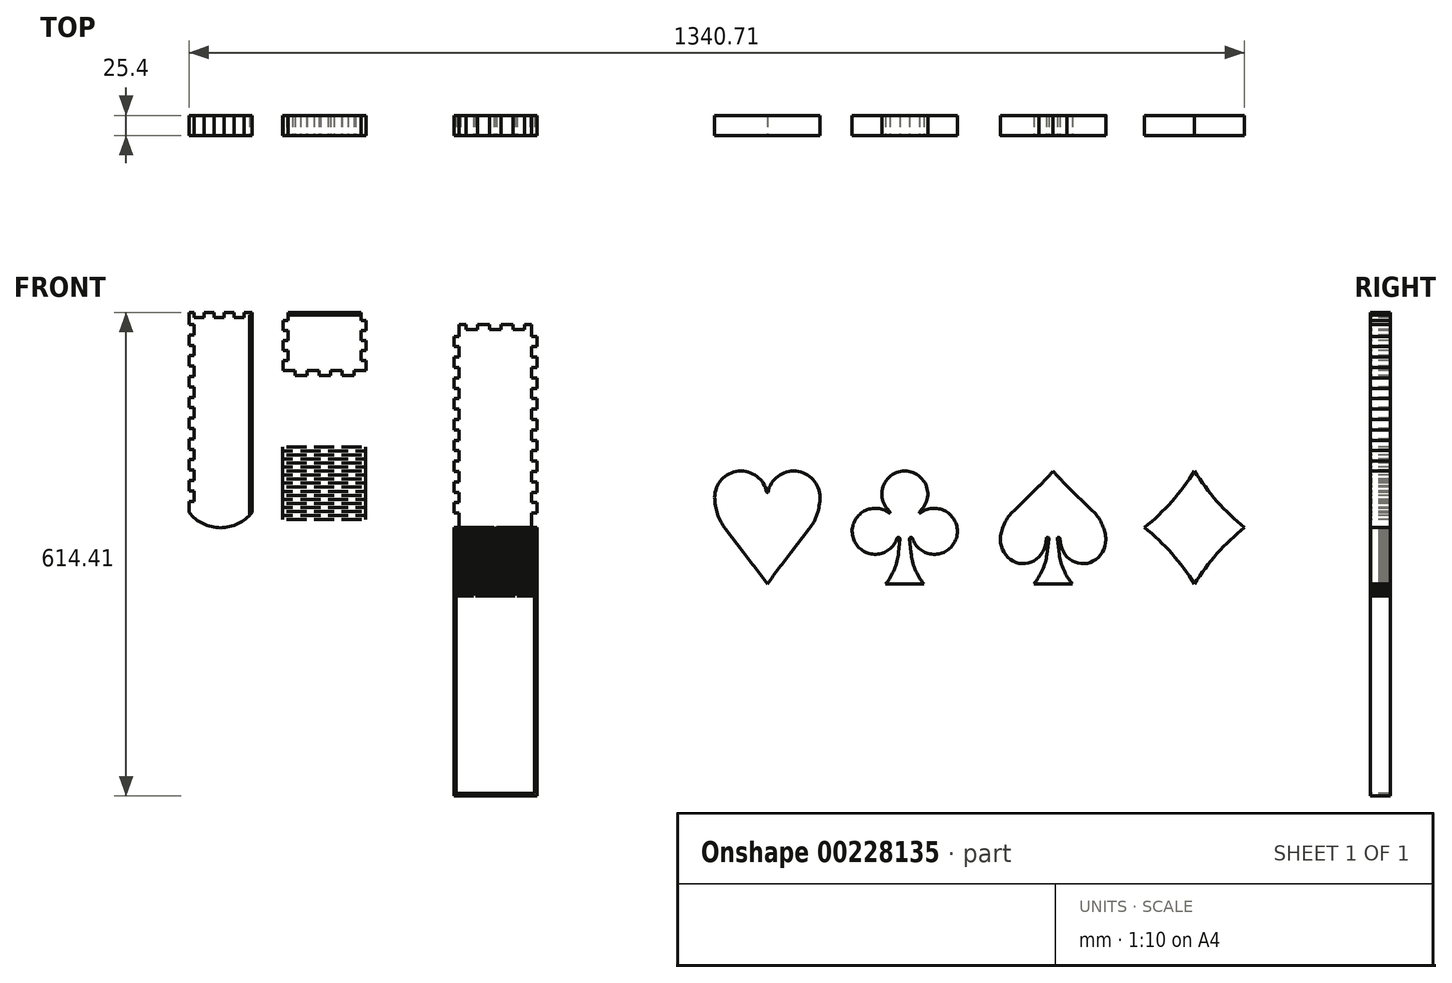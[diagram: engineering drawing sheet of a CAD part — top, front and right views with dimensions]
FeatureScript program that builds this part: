
annotation { "Feature Type Name" : "Feature", "Feature Type Description" : "" }
export const myFeature = defineFeature(function(context is Context, id is Id, definition is map)
    precondition{}
    {
        {
            var Q0;
            Q0=qCreatedBy(makeId("Front.planeOp"),FACE);
            var sketch = newSketch(context, id + "F0", { "sketchPlane" : qUnion([Q0])});
            skLineSegment(sketch, "E0.bottom", {"start": v(-104.23, 196.53) * mm, "end": v(-97.88, 196.53) * mm});
            skLineSegment(sketch, "E0.top", {"start": v(-104.23, -57.47) * mm, "end": v(-24.22, -57.47) * mm, "construction": true});
            skLineSegment(sketch, "E0.left", {"start": v(-104.23, 196.53) * mm, "end": v(-104.23, 181.29) * mm});
            skLineSegment(sketch, "E0.right", {"start": v(-24.22, 196.53) * mm, "end": v(-24.22, -57.47) * mm});
            skArc(sketch, "E1", {"start": v(-104.23, -57.47) * mm, "mid": v(-64.23, -76.96) * mm, "end": v(-24.22, -57.47) * mm});
            skLineSegment(sketch, "E2.0", {"start": v(-97.88, 181.29) * mm, "end": v(-97.88, 168.08) * mm});
            skLineSegment(sketch, "E2.1", {"start": v(-97.88, 190.18) * mm, "end": v(-85.18, 190.18) * mm});
            skLineSegment(sketch, "E3.0", {"start": v(-27.4, 193.35) * mm, "end": v(-27.4, -61.15) * mm});
            skLineSegment(sketch, "E4.bottom", {"start": v(21.69, 196.53) * mm, "end": v(114.4, 196.53) * mm});
            skLineSegment(sketch, "E4.top", {"start": v(30.76, 116.52) * mm, "end": v(45.74, 116.52) * mm});
            skLineSegment(sketch, "E4.left", {"start": v(15.34, 186.37) * mm, "end": v(15.34, 173.67) * mm});
            skLineSegment(sketch, "E5.0", {"start": v(21.69, 196.53) * mm, "end": v(21.69, 186.37) * mm});
            skLineSegment(sketch, "E5.3", {"start": v(15.34, 122.87) * mm, "end": v(30.76, 122.87) * mm});
            skLineSegment(sketch, "E6.left", {"start": v(14.8, 25.75) * mm, "end": v(14.8, -66.32) * mm});
            skLineSegment(sketch, "E6.right", {"start": v(120.2, 25.8) * mm, "end": v(120.2, -66.32) * mm});
            skLineSegment(sketch, "E7", {"start": v(21.69, 193.35) * mm, "end": v(114.4, 193.35) * mm});
            skLineSegment(sketch, "E8", {"start": v(19.75, 25.75) * mm, "end": v(45.15, 25.75) * mm});
            skLineSegment(sketch, "E9", {"start": v(-97.88, 190.18) * mm, "end": v(-97.88, 190.18) * mm});
            skLineSegment(sketch, "E10", {"start": v(-97.88, 190.18) * mm, "end": v(-97.88, 196.53) * mm});
            skLineSegment(sketch, "E11", {"start": v(-85.18, 190.18) * mm, "end": v(-85.18, 196.53) * mm});
            skLineSegment(sketch, "E12", {"start": v(-59.78, 190.18) * mm, "end": v(-59.78, 196.53) * mm});
            skLineSegment(sketch, "E13", {"start": v(-47.08, 190.18) * mm, "end": v(-47.08, 196.53) * mm});
            skLineSegment(sketch, "E14", {"start": v(-34.38, 190.18) * mm, "end": v(-34.38, 196.53) * mm});
            skLineSegment(sketch, "E15", {"start": v(-72.48, 190.18) * mm, "end": v(-72.48, 196.53) * mm});
            skLineSegment(sketch, "E16.trimOffspring", {"start": v(-34.38, 196.53) * mm, "end": v(-24.22, 196.53) * mm});
            skLineSegment(sketch, "E17.trimOffspring", {"start": v(-47.08, 190.18) * mm, "end": v(-34.38, 190.18) * mm});
            skLineSegment(sketch, "E18.trimOffspring", {"start": v(-59.78, 196.53) * mm, "end": v(-47.08, 196.53) * mm});
            skLineSegment(sketch, "E19.trimOffspring", {"start": v(-85.18, 196.53) * mm, "end": v(-72.48, 196.53) * mm});
            skLineSegment(sketch, "E20.trimOffspring", {"start": v(-72.48, 190.18) * mm, "end": v(-59.78, 190.18) * mm});
            skLineSegment(sketch, "E21", {"start": v(-27.4, 193.35) * mm, "end": v(-24.22, 193.35) * mm});
            skLineSegment(sketch, "E22", {"start": v(15.34, 186.37) * mm, "end": v(21.69, 186.37) * mm});
            skLineSegment(sketch, "E23", {"start": v(21.69, 173.67) * mm, "end": v(15.34, 173.67) * mm});
            skLineSegment(sketch, "E24", {"start": v(15.34, 160.97) * mm, "end": v(21.69, 160.97) * mm});
            skLineSegment(sketch, "E25", {"start": v(21.69, 148.27) * mm, "end": v(15.34, 148.27) * mm});
            skLineSegment(sketch, "E26", {"start": v(15.34, 135.57) * mm, "end": v(21.69, 135.57) * mm});
            skPoint(sketch, "E27.orphan", {"position": v(15.34, 196.53) * mm});
            skLineSegment(sketch, "E28.trimOffspring", {"start": v(21.69, 173.67) * mm, "end": v(21.69, 160.97) * mm});
            skLineSegment(sketch, "E29.trimOffspring", {"start": v(15.34, 160.97) * mm, "end": v(15.34, 148.27) * mm});
            skLineSegment(sketch, "E30.trimOffspring", {"start": v(21.69, 148.27) * mm, "end": v(21.69, 135.57) * mm});
            skLineSegment(sketch, "E31.trimOffspring", {"start": v(15.34, 135.57) * mm, "end": v(15.34, 122.87) * mm});
            skLineSegment(sketch, "E32", {"start": v(68.04, 193.35) * mm, "end": v(68.04, 116.52) * mm, "construction": true});
            skPoint(sketch, "E32.endSnap0", {"position": v(64.87, 122.87) * mm});
            skLineSegment(sketch, "E33", {"start": v(30.76, 122.87) * mm, "end": v(30.76, 116.52) * mm});
            skLineSegment(sketch, "E34", {"start": v(45.74, 116.52) * mm, "end": v(45.74, 122.87) * mm});
            skLineSegment(sketch, "E35", {"start": v(60.73, 122.87) * mm, "end": v(60.73, 116.52) * mm});
            skLineSegment(sketch, "E36.trimOffspring", {"start": v(45.74, 122.87) * mm, "end": v(60.73, 122.87) * mm});
            skLineSegment(sketch, "E37.trimOffspring", {"start": v(60.73, 116.52) * mm, "end": v(68.04, 116.52) * mm});
            skPoint(sketch, "E38.orphan", {"position": v(68.04, 122.87) * mm});
            skPoint(sketch, "E39.orphan", {"position": v(114.4, 122.87) * mm});
            skLineSegment(sketch, "E40.MirrorCS", {"start": v(120.75, 186.37) * mm, "end": v(114.4, 186.37) * mm});
            skLineSegment(sketch, "E41.MirrorCS", {"start": v(105.32, 122.87) * mm, "end": v(105.32, 116.52) * mm});
            skLineSegment(sketch, "E42.MirrorCS", {"start": v(120.75, 135.57) * mm, "end": v(114.4, 135.57) * mm});
            skLineSegment(sketch, "E43.MirrorCS", {"start": v(120.75, 160.97) * mm, "end": v(114.4, 160.97) * mm});
            skLineSegment(sketch, "E44.MirrorCS", {"start": v(114.4, 148.27) * mm, "end": v(114.4, 135.57) * mm});
            skLineSegment(sketch, "E45.MirrorCS", {"start": v(120.75, 135.57) * mm, "end": v(120.75, 122.87) * mm});
            skLineSegment(sketch, "E46.MirrorCS", {"start": v(114.4, 196.53) * mm, "end": v(114.4, 186.37) * mm});
            skLineSegment(sketch, "E47.MirrorCS", {"start": v(114.4, 173.67) * mm, "end": v(114.4, 160.97) * mm});
            skLineSegment(sketch, "E48.MirrorCS", {"start": v(114.4, 173.67) * mm, "end": v(120.75, 173.67) * mm});
            skLineSegment(sketch, "E49.MirrorCS", {"start": v(114.4, 148.27) * mm, "end": v(120.75, 148.27) * mm});
            skPoint(sketch, "E50.MirrorP", {"position": v(120.75, 196.53) * mm});
            skLineSegment(sketch, "E51.MirrorCS", {"start": v(120.75, 122.87) * mm, "end": v(105.32, 122.87) * mm});
            skLineSegment(sketch, "E52.MirrorCS", {"start": v(120.75, 186.37) * mm, "end": v(120.75, 173.67) * mm});
            skLineSegment(sketch, "E53.MirrorCS", {"start": v(120.75, 160.97) * mm, "end": v(120.75, 148.27) * mm});
            skLineSegment(sketch, "E54.MirrorCS", {"start": v(90.34, 122.87) * mm, "end": v(75.35, 122.87) * mm});
            skPoint(sketch, "E55.MirrorP", {"position": v(71.22, 122.87) * mm});
            skLineSegment(sketch, "E56.MirrorCS", {"start": v(90.34, 116.52) * mm, "end": v(90.34, 122.87) * mm});
            skLineSegment(sketch, "E57.MirrorCS", {"start": v(75.35, 122.87) * mm, "end": v(75.35, 116.52) * mm});
            skLineSegment(sketch, "E58.MirrorCS", {"start": v(75.35, 116.52) * mm, "end": v(68.04, 116.52) * mm});
            skLineSegment(sketch, "E59.MirrorCS", {"start": v(105.32, 116.52) * mm, "end": v(90.34, 116.52) * mm});
            skLineSegment(sketch, "E60", {"start": v(-104.23, 181.29) * mm, "end": v(-97.88, 181.29) * mm});
            skLineSegment(sketch, "E61.0.1.0", {"start": v(-104.23, 168.08) * mm, "end": v(-97.88, 168.08) * mm});
            skLineSegment(sketch, "E61.0.2.0", {"start": v(-104.23, 154.87) * mm, "end": v(-97.88, 154.87) * mm});
            skLineSegment(sketch, "E61.0.3.0", {"start": v(-104.23, 141.66) * mm, "end": v(-97.88, 141.66) * mm});
            skLineSegment(sketch, "E61.0.4.0", {"start": v(-104.23, 128.46) * mm, "end": v(-97.88, 128.46) * mm});
            skLineSegment(sketch, "E61.0.5.0", {"start": v(-104.23, 115.25) * mm, "end": v(-97.88, 115.25) * mm});
            skLineSegment(sketch, "E61.0.6.0", {"start": v(-104.23, 102.04) * mm, "end": v(-97.88, 102.04) * mm});
            skLineSegment(sketch, "E61.0.7.0", {"start": v(-104.23, 88.83) * mm, "end": v(-97.88, 88.83) * mm});
            skLineSegment(sketch, "E61.0.8.0", {"start": v(-104.23, 75.62) * mm, "end": v(-97.88, 75.62) * mm});
            skLineSegment(sketch, "E61.0.9.0", {"start": v(-104.23, 62.42) * mm, "end": v(-97.88, 62.42) * mm});
            skLineSegment(sketch, "E61.0.10.0", {"start": v(-104.23, 49.2) * mm, "end": v(-97.88, 49.2) * mm});
            skLineSegment(sketch, "E61.0.11.0", {"start": v(-104.23, 36) * mm, "end": v(-97.88, 36) * mm});
            skLineSegment(sketch, "E61.0.12.0", {"start": v(-104.23, 22.8) * mm, "end": v(-97.88, 22.8) * mm});
            skLineSegment(sketch, "E61.0.13.0", {"start": v(-104.23, 9.58) * mm, "end": v(-97.88, 9.58) * mm});
            skLineSegment(sketch, "E61.0.14.0", {"start": v(-104.23, -3.62) * mm, "end": v(-97.88, -3.62) * mm});
            skLineSegment(sketch, "E61.0.15.0", {"start": v(-104.23, -16.83) * mm, "end": v(-97.88, -16.83) * mm});
            skLineSegment(sketch, "E61.0.16.0", {"start": v(-104.23, -30.04) * mm, "end": v(-97.88, -30.04) * mm});
            skLineSegment(sketch, "E61.0.17.0", {"start": v(-104.23, -43.25) * mm, "end": v(-97.88, -43.25) * mm});
            skLineSegment(sketch, "E61.direction1", {"start": v(-104.23, 181.29) * mm, "end": v(-78.83, 181.29) * mm, "construction": true});
            skLineSegment(sketch, "E62.trimOffspring", {"start": v(-104.23, 168.08) * mm, "end": v(-104.23, 154.87) * mm});
            skLineSegment(sketch, "E63.trimOffspring", {"start": v(-97.88, 154.87) * mm, "end": v(-97.88, 141.66) * mm});
            skLineSegment(sketch, "E64.trimOffspring", {"start": v(-104.23, 141.66) * mm, "end": v(-104.23, 128.46) * mm});
            skLineSegment(sketch, "E65.trimOffspring", {"start": v(-97.88, 128.46) * mm, "end": v(-97.88, 115.25) * mm});
            skLineSegment(sketch, "E66.trimOffspring", {"start": v(-104.23, 115.25) * mm, "end": v(-104.23, 102.04) * mm});
            skLineSegment(sketch, "E67.trimOffspring", {"start": v(-97.88, 102.04) * mm, "end": v(-97.88, 88.83) * mm});
            skLineSegment(sketch, "E68.trimOffspring", {"start": v(-104.23, 88.83) * mm, "end": v(-104.23, 75.62) * mm});
            skLineSegment(sketch, "E69.trimOffspring", {"start": v(-97.88, 75.62) * mm, "end": v(-97.88, 62.42) * mm});
            skLineSegment(sketch, "E70.trimOffspring", {"start": v(-104.23, 62.42) * mm, "end": v(-104.23, 49.2) * mm});
            skLineSegment(sketch, "E71.trimOffspring", {"start": v(-97.88, 49.2) * mm, "end": v(-97.88, 36) * mm});
            skLineSegment(sketch, "E72.trimOffspring", {"start": v(-104.23, 36) * mm, "end": v(-104.23, 22.8) * mm});
            skLineSegment(sketch, "E73.trimOffspring", {"start": v(-97.88, 22.8) * mm, "end": v(-97.88, 9.58) * mm});
            skLineSegment(sketch, "E74.trimOffspring", {"start": v(-104.23, 9.58) * mm, "end": v(-104.23, -3.62) * mm});
            skLineSegment(sketch, "E75.trimOffspring", {"start": v(-97.88, -3.62) * mm, "end": v(-97.88, -16.83) * mm});
            skLineSegment(sketch, "E76.trimOffspring", {"start": v(-104.23, -16.83) * mm, "end": v(-104.23, -30.04) * mm});
            skLineSegment(sketch, "E77.trimOffspring", {"start": v(-97.88, -30.04) * mm, "end": v(-97.88, -43.25) * mm});
            skLineSegment(sketch, "E78.trimOffspring", {"start": v(-104.23, -43.25) * mm, "end": v(-104.23, -57.47) * mm});
            skLineSegment(sketch, "E79", {"start": v(54.8, 25.75) * mm, "end": v(67.5, 25.75) * mm});
            skPoint(sketch, "E79.startSnap0", {"position": v(32.45, 25.75) * mm});
            skLineSegment(sketch, "E80", {"start": v(67.5, -66.32) * mm, "end": v(67.5, 48.28) * mm, "construction": true});
            skLineSegment(sketch, "E81", {"start": v(37.27, 20.63) * mm, "end": v(62.67, 20.63) * mm});
            skLineSegment(sketch, "E82", {"start": v(27.62, 20.63) * mm, "end": v(14.8, 20.63) * mm});
            skLineSegment(sketch, "E83.0.1.0", {"start": v(27.62, 10.4) * mm, "end": v(14.8, 10.4) * mm});
            skLineSegment(sketch, "E83.0.1.1", {"start": v(19.75, 15.51) * mm, "end": v(45.15, 15.51) * mm});
            skLineSegment(sketch, "E83.0.1.2", {"start": v(37.27, 10.4) * mm, "end": v(62.67, 10.4) * mm});
            skLineSegment(sketch, "E83.0.1.3", {"start": v(54.8, 15.51) * mm, "end": v(67.5, 15.51) * mm});
            skLineSegment(sketch, "E83.0.2.0", {"start": v(27.62, 0.16) * mm, "end": v(14.8, 0.16) * mm});
            skLineSegment(sketch, "E83.0.2.1", {"start": v(19.75, 5.28) * mm, "end": v(45.15, 5.28) * mm});
            skLineSegment(sketch, "E83.0.2.2", {"start": v(37.27, 0.16) * mm, "end": v(62.67, 0.16) * mm});
            skLineSegment(sketch, "E83.0.2.3", {"start": v(54.8, 5.28) * mm, "end": v(67.5, 5.28) * mm});
            skLineSegment(sketch, "E83.0.3.0", {"start": v(27.62, -10.08) * mm, "end": v(14.8, -10.08) * mm});
            skLineSegment(sketch, "E83.0.3.1", {"start": v(19.75, -4.96) * mm, "end": v(45.15, -4.96) * mm});
            skLineSegment(sketch, "E83.0.3.2", {"start": v(37.27, -10.08) * mm, "end": v(62.67, -10.08) * mm});
            skLineSegment(sketch, "E83.0.3.3", {"start": v(54.8, -4.96) * mm, "end": v(67.5, -4.96) * mm});
            skLineSegment(sketch, "E83.0.4.0", {"start": v(27.62, -20.31) * mm, "end": v(14.8, -20.31) * mm});
            skLineSegment(sketch, "E83.0.4.1", {"start": v(19.75, -15.2) * mm, "end": v(45.15, -15.2) * mm});
            skLineSegment(sketch, "E83.0.4.2", {"start": v(37.27, -20.31) * mm, "end": v(62.67, -20.31) * mm});
            skLineSegment(sketch, "E83.0.4.3", {"start": v(54.8, -15.2) * mm, "end": v(67.5, -15.2) * mm});
            skLineSegment(sketch, "E83.0.5.0", {"start": v(27.62, -30.55) * mm, "end": v(14.8, -30.55) * mm});
            skLineSegment(sketch, "E83.0.5.1", {"start": v(19.75, -25.43) * mm, "end": v(45.15, -25.43) * mm});
            skLineSegment(sketch, "E83.0.5.2", {"start": v(37.27, -30.55) * mm, "end": v(62.67, -30.55) * mm});
            skLineSegment(sketch, "E83.0.5.3", {"start": v(54.8, -25.43) * mm, "end": v(67.5, -25.43) * mm});
            skLineSegment(sketch, "E83.0.6.0", {"start": v(27.62, -40.78) * mm, "end": v(14.8, -40.78) * mm});
            skLineSegment(sketch, "E83.0.6.1", {"start": v(19.75, -35.67) * mm, "end": v(45.15, -35.67) * mm});
            skLineSegment(sketch, "E83.0.6.2", {"start": v(37.27, -40.78) * mm, "end": v(62.67, -40.78) * mm});
            skLineSegment(sketch, "E83.0.6.3", {"start": v(54.8, -35.67) * mm, "end": v(67.5, -35.67) * mm});
            skLineSegment(sketch, "E83.0.7.0", {"start": v(27.62, -51.02) * mm, "end": v(14.8, -51.02) * mm});
            skLineSegment(sketch, "E83.0.7.1", {"start": v(19.75, -45.9) * mm, "end": v(45.15, -45.9) * mm});
            skLineSegment(sketch, "E83.0.7.2", {"start": v(37.27, -51.02) * mm, "end": v(62.67, -51.02) * mm});
            skLineSegment(sketch, "E83.0.7.3", {"start": v(54.8, -45.9) * mm, "end": v(67.5, -45.9) * mm});
            skLineSegment(sketch, "E83.0.8.0", {"start": v(27.62, -61.26) * mm, "end": v(14.8, -61.26) * mm});
            skLineSegment(sketch, "E83.0.8.1", {"start": v(19.75, -56.14) * mm, "end": v(45.15, -56.14) * mm});
            skLineSegment(sketch, "E83.0.8.2", {"start": v(37.27, -61.26) * mm, "end": v(62.67, -61.26) * mm});
            skLineSegment(sketch, "E83.0.8.3", {"start": v(54.8, -56.14) * mm, "end": v(67.5, -56.14) * mm});
            skLineSegment(sketch, "E83.direction1", {"start": v(14.8, 20.63) * mm, "end": v(40.2, 20.63) * mm, "construction": true});
            skLineSegment(sketch, "E83.direction2", {"start": v(14.8, 20.63) * mm, "end": v(14.8, 10.4) * mm, "construction": true});
            skLineSegment(sketch, "E84.0.1.0", {"start": v(19.75, -66.37) * mm, "end": v(45.15, -66.37) * mm});
            skLineSegment(sketch, "E84.0.1.1", {"start": v(54.8, -66.37) * mm, "end": v(67.5, -66.37) * mm});
            skLineSegment(sketch, "E84.direction1", {"start": v(19.75, -56.14) * mm, "end": v(45.15, -56.14) * mm, "construction": true});
            skLineSegment(sketch, "E84.direction2", {"start": v(19.75, -56.14) * mm, "end": v(19.75, -66.37) * mm, "construction": true});
            skLineSegment(sketch, "E85.MirrorCS", {"start": v(107.38, 20.63) * mm, "end": v(120.2, 20.63) * mm});
            skLineSegment(sketch, "E86.MirrorCS", {"start": v(115.25, -56.14) * mm, "end": v(89.85, -56.14) * mm});
            skLineSegment(sketch, "E87.MirrorCS", {"start": v(97.72, -61.26) * mm, "end": v(72.32, -61.26) * mm});
            skLineSegment(sketch, "E88.MirrorCS", {"start": v(97.72, 20.63) * mm, "end": v(72.32, 20.63) * mm});
            skLineSegment(sketch, "E89.MirrorCS", {"start": v(115.25, 25.75) * mm, "end": v(89.85, 25.75) * mm});
            skLineSegment(sketch, "E90.MirrorCS", {"start": v(107.38, -30.55) * mm, "end": v(120.2, -30.55) * mm});
            skLineSegment(sketch, "E91.MirrorCS", {"start": v(107.38, 10.4) * mm, "end": v(120.2, 10.4) * mm});
            skLineSegment(sketch, "E92.MirrorCS", {"start": v(80.2, 25.75) * mm, "end": v(67.5, 25.75) * mm});
            skLineSegment(sketch, "E93.MirrorCS", {"start": v(115.25, 15.51) * mm, "end": v(89.85, 15.51) * mm});
            skLineSegment(sketch, "E94.MirrorCS", {"start": v(120.2, 20.63) * mm, "end": v(120.2, 10.4) * mm, "construction": true});
            skLineSegment(sketch, "E95.MirrorCS", {"start": v(97.72, -10.08) * mm, "end": v(72.32, -10.08) * mm});
            skLineSegment(sketch, "E96.MirrorCS", {"start": v(115.25, -45.9) * mm, "end": v(89.85, -45.9) * mm});
            skLineSegment(sketch, "E97.MirrorCS", {"start": v(115.25, -4.96) * mm, "end": v(89.85, -4.96) * mm});
            skLineSegment(sketch, "E98.MirrorCS", {"start": v(97.72, 10.4) * mm, "end": v(72.32, 10.4) * mm});
            skLineSegment(sketch, "E99.MirrorCS", {"start": v(120.2, 25.75) * mm, "end": v(120.2, -66.32) * mm});
            skLineSegment(sketch, "E100.MirrorCS", {"start": v(80.2, -45.9) * mm, "end": v(67.5, -45.9) * mm});
            skLineSegment(sketch, "E101.MirrorCS", {"start": v(97.72, -40.78) * mm, "end": v(72.32, -40.78) * mm});
            skLineSegment(sketch, "E102.MirrorCS", {"start": v(115.25, -66.37) * mm, "end": v(89.85, -66.37) * mm});
            skLineSegment(sketch, "E103.MirrorCS", {"start": v(115.25, -35.67) * mm, "end": v(89.85, -35.67) * mm});
            skLineSegment(sketch, "E104.MirrorCS", {"start": v(107.38, -20.31) * mm, "end": v(120.2, -20.31) * mm});
            skLineSegment(sketch, "E105.MirrorCS", {"start": v(107.38, -61.26) * mm, "end": v(120.2, -61.26) * mm});
            skLineSegment(sketch, "E106.MirrorCS", {"start": v(115.25, -56.14) * mm, "end": v(115.25, -66.37) * mm, "construction": true});
            skLineSegment(sketch, "E107.MirrorCS", {"start": v(80.2, -15.2) * mm, "end": v(67.5, -15.2) * mm});
            skLineSegment(sketch, "E108.MirrorCS", {"start": v(107.38, -10.08) * mm, "end": v(120.2, -10.08) * mm});
            skLineSegment(sketch, "E109.MirrorCS", {"start": v(97.72, -20.31) * mm, "end": v(72.32, -20.31) * mm});
            skLineSegment(sketch, "E110.MirrorCS", {"start": v(115.25, -56.14) * mm, "end": v(89.85, -56.14) * mm, "construction": true});
            skLineSegment(sketch, "E111.MirrorCS", {"start": v(80.2, -35.67) * mm, "end": v(67.5, -35.67) * mm});
            skLineSegment(sketch, "E112.MirrorCS", {"start": v(80.2, 5.28) * mm, "end": v(67.5, 5.28) * mm});
            skLineSegment(sketch, "E113.MirrorCS", {"start": v(97.72, -51.02) * mm, "end": v(72.32, -51.02) * mm});
            skLineSegment(sketch, "E114.MirrorCS", {"start": v(97.72, -30.55) * mm, "end": v(72.32, -30.55) * mm});
            skLineSegment(sketch, "E115.MirrorCS", {"start": v(107.38, -51.02) * mm, "end": v(120.2, -51.02) * mm});
            skLineSegment(sketch, "E116.MirrorCS", {"start": v(115.25, -15.2) * mm, "end": v(89.85, -15.2) * mm});
            skLineSegment(sketch, "E117.MirrorCS", {"start": v(80.2, -56.14) * mm, "end": v(67.5, -56.14) * mm});
            skLineSegment(sketch, "E118.MirrorCS", {"start": v(97.72, 0.16) * mm, "end": v(72.32, 0.16) * mm});
            skLineSegment(sketch, "E119.MirrorCS", {"start": v(115.25, 5.28) * mm, "end": v(89.85, 5.28) * mm});
            skLineSegment(sketch, "E120.MirrorCS", {"start": v(107.38, -40.78) * mm, "end": v(120.2, -40.78) * mm});
            skLineSegment(sketch, "E121.MirrorCS", {"start": v(80.2, -4.96) * mm, "end": v(67.5, -4.96) * mm});
            skLineSegment(sketch, "E122.MirrorCS", {"start": v(107.38, 0.16) * mm, "end": v(120.2, 0.16) * mm});
            skLineSegment(sketch, "E123.MirrorCS", {"start": v(115.25, -25.43) * mm, "end": v(89.85, -25.43) * mm});
            skPoint(sketch, "E124.MirrorP", {"position": v(102.55, 25.75) * mm});
            skLineSegment(sketch, "E125.MirrorCS", {"start": v(80.2, -25.43) * mm, "end": v(67.5, -25.43) * mm});
            skLineSegment(sketch, "E126.MirrorCS", {"start": v(80.2, 15.51) * mm, "end": v(67.5, 15.51) * mm});
            skLineSegment(sketch, "E127.MirrorCS", {"start": v(80.2, -66.37) * mm, "end": v(67.5, -66.37) * mm});
            skLineSegment(sketch, "E128.bottom", {"start": v(238.49, 181.5) * mm, "end": v(247.56, 181.5) * mm});
            skLineSegment(sketch, "E128.left", {"start": v(232.14, 166.25) * mm, "end": v(232.14, 153.04) * mm});
            skLineSegment(sketch, "E129.left", {"start": v(232.14, -76.56) * mm, "end": v(232.14, -163.88) * mm});
            skLineSegment(sketch, "E130", {"start": v(284.84, -164.58) * mm, "end": v(284.84, -49.98) * mm, "construction": true});
            skLineSegment(sketch, "E131.0", {"start": v(238.49, 175.14) * mm, "end": v(238.49, 166.25) * mm});
            skLineSegment(sketch, "E131.1", {"start": v(247.56, 175.14) * mm, "end": v(262.54, 175.14) * mm});
            skLineSegment(sketch, "E132", {"start": v(232.14, -163.88) * mm, "end": v(232.14, -417.88) * mm});
            skLineSegment(sketch, "E133", {"start": v(232.14, -417.88) * mm, "end": v(337.55, -417.88) * mm});
            skLineSegment(sketch, "E134", {"start": v(337.55, -417.88) * mm, "end": v(337.55, -163.88) * mm});
            skLineSegment(sketch, "E135", {"start": v(238.49, 175.14) * mm, "end": v(238.49, 181.5) * mm});
            skLineSegment(sketch, "E136", {"start": v(247.56, 181.5) * mm, "end": v(247.56, 175.14) * mm});
            skLineSegment(sketch, "E137", {"start": v(262.54, 175.14) * mm, "end": v(262.54, 181.5) * mm});
            skLineSegment(sketch, "E138", {"start": v(277.53, 181.5) * mm, "end": v(277.53, 175.14) * mm});
            skLineSegment(sketch, "E139", {"start": v(292.15, 181.5) * mm, "end": v(292.15, 175.14) * mm});
            skLineSegment(sketch, "E140", {"start": v(307.14, 175.14) * mm, "end": v(307.14, 181.5) * mm});
            skLineSegment(sketch, "E141", {"start": v(322.12, 175.14) * mm, "end": v(322.12, 181.5) * mm});
            skLineSegment(sketch, "E142.trimOffspring", {"start": v(262.54, 181.5) * mm, "end": v(277.53, 181.5) * mm});
            skLineSegment(sketch, "E143.trimOffspring", {"start": v(277.53, 175.14) * mm, "end": v(292.15, 175.14) * mm});
            skLineSegment(sketch, "E144.trimOffspring", {"start": v(292.15, 181.5) * mm, "end": v(307.14, 181.5) * mm});
            skLineSegment(sketch, "E145.trimOffspring", {"start": v(307.14, 175.14) * mm, "end": v(322.12, 175.14) * mm});
            skLineSegment(sketch, "E146.trimOffspring", {"start": v(322.12, 181.5) * mm, "end": v(331.2, 181.5) * mm});
            skLineSegment(sketch, "E147", {"start": v(232.14, 166.25) * mm, "end": v(238.49, 166.25) * mm});
            skLineSegment(sketch, "E148", {"start": v(232.14, 153.04) * mm, "end": v(238.49, 153.04) * mm});
            skLineSegment(sketch, "E149", {"start": v(238.49, 139.83) * mm, "end": v(232.14, 139.83) * mm});
            skLineSegment(sketch, "E150.trimOffspring", {"start": v(238.49, 153.04) * mm, "end": v(238.49, 139.83) * mm});
            skLineSegment(sketch, "E151.0.1.1", {"start": v(232.14, 139.83) * mm, "end": v(232.14, 126.63) * mm});
            skLineSegment(sketch, "E151.0.1.2", {"start": v(232.14, 126.63) * mm, "end": v(238.49, 126.63) * mm});
            skLineSegment(sketch, "E151.0.1.3", {"start": v(238.49, 126.63) * mm, "end": v(238.49, 113.42) * mm});
            skLineSegment(sketch, "E151.0.1.4", {"start": v(238.49, 113.42) * mm, "end": v(232.14, 113.42) * mm});
            skLineSegment(sketch, "E151.0.2.1", {"start": v(232.14, 113.42) * mm, "end": v(232.14, 100.21) * mm});
            skLineSegment(sketch, "E151.0.2.2", {"start": v(232.14, 100.21) * mm, "end": v(238.49, 100.21) * mm});
            skLineSegment(sketch, "E151.0.2.3", {"start": v(238.49, 100.21) * mm, "end": v(238.49, 87) * mm});
            skLineSegment(sketch, "E151.0.3.1", {"start": v(232.14, 87) * mm, "end": v(232.14, 73.8) * mm});
            skLineSegment(sketch, "E151.0.3.2", {"start": v(232.14, 73.8) * mm, "end": v(238.49, 73.8) * mm});
            skLineSegment(sketch, "E151.0.3.3", {"start": v(238.49, 73.8) * mm, "end": v(238.49, 60.59) * mm});
            skLineSegment(sketch, "E151.0.3.4", {"start": v(238.49, 60.59) * mm, "end": v(232.14, 60.59) * mm});
            skLineSegment(sketch, "E151.0.4.1", {"start": v(232.14, 60.59) * mm, "end": v(232.14, 47.38) * mm});
            skLineSegment(sketch, "E151.0.4.2", {"start": v(232.14, 47.38) * mm, "end": v(238.49, 47.38) * mm});
            skLineSegment(sketch, "E151.0.4.3", {"start": v(238.49, 47.38) * mm, "end": v(238.49, 34.17) * mm});
            skLineSegment(sketch, "E151.0.4.4", {"start": v(238.49, 34.17) * mm, "end": v(232.14, 34.17) * mm});
            skLineSegment(sketch, "E151.0.5.1", {"start": v(232.14, 34.17) * mm, "end": v(232.14, 20.96) * mm});
            skLineSegment(sketch, "E151.0.5.2", {"start": v(232.14, 20.96) * mm, "end": v(238.49, 20.96) * mm});
            skLineSegment(sketch, "E151.0.5.3", {"start": v(238.49, 20.96) * mm, "end": v(238.49, 7.75) * mm});
            skLineSegment(sketch, "E151.0.5.4", {"start": v(238.49, 7.75) * mm, "end": v(232.14, 7.75) * mm});
            skLineSegment(sketch, "E151.0.6.1", {"start": v(232.14, 7.75) * mm, "end": v(232.14, -5.45) * mm});
            skLineSegment(sketch, "E151.0.6.2", {"start": v(232.14, -5.45) * mm, "end": v(238.49, -5.45) * mm});
            skLineSegment(sketch, "E151.0.6.3", {"start": v(238.49, -5.45) * mm, "end": v(238.49, -18.66) * mm});
            skLineSegment(sketch, "E151.0.7.1", {"start": v(232.14, -18.66) * mm, "end": v(232.14, -31.87) * mm});
            skLineSegment(sketch, "E151.0.7.3", {"start": v(238.49, -31.87) * mm, "end": v(238.49, -45.08) * mm});
            skLineSegment(sketch, "E151.0.7.4", {"start": v(238.49, -45.08) * mm, "end": v(232.14, -45.08) * mm});
            skLineSegment(sketch, "E151.0.8.1", {"start": v(232.14, -45.08) * mm, "end": v(232.14, -58.29) * mm});
            skLineSegment(sketch, "E151.0.8.2", {"start": v(232.14, -58.29) * mm, "end": v(238.49, -58.29) * mm});
            skLineSegment(sketch, "E151.0.8.3", {"start": v(238.49, -58.29) * mm, "end": v(238.49, -76.56) * mm});
            skLineSegment(sketch, "E151.direction1", {"start": v(232.14, 166.25) * mm, "end": v(255.01, 166.25) * mm, "construction": true});
            skLineSegment(sketch, "E151.direction2", {"start": v(232.14, 166.25) * mm, "end": v(232.14, 139.83) * mm, "construction": true});
            skLineSegment(sketch, "E152.MirrorCS", {"start": v(331.2, 7.75) * mm, "end": v(337.55, 7.75) * mm});
            skLineSegment(sketch, "E153.MirrorCS", {"start": v(331.2, -45.08) * mm, "end": v(337.55, -45.08) * mm});
            skLineSegment(sketch, "E154.MirrorCS", {"start": v(337.55, -45.08) * mm, "end": v(337.55, -58.29) * mm});
            skLineSegment(sketch, "E155.MirrorCS", {"start": v(337.55, -18.66) * mm, "end": v(337.55, -31.87) * mm});
            skLineSegment(sketch, "E156.MirrorCS", {"start": v(337.55, 7.75) * mm, "end": v(337.55, -5.45) * mm});
            skLineSegment(sketch, "E157.MirrorCS", {"start": v(337.55, -58.29) * mm, "end": v(331.2, -58.29) * mm});
            skLineSegment(sketch, "E158.MirrorCS", {"start": v(331.2, -31.87) * mm, "end": v(331.2, -45.08) * mm});
            skLineSegment(sketch, "E159.MirrorCS", {"start": v(331.2, -5.45) * mm, "end": v(331.2, -18.66) * mm});
            skLineSegment(sketch, "E160.MirrorCS", {"start": v(331.2, 113.42) * mm, "end": v(337.55, 113.42) * mm});
            skLineSegment(sketch, "E161.MirrorCS", {"start": v(331.2, 60.59) * mm, "end": v(337.55, 60.59) * mm});
            skLineSegment(sketch, "E162.MirrorCS", {"start": v(337.55, 126.63) * mm, "end": v(331.2, 126.63) * mm});
            skLineSegment(sketch, "E163.MirrorCS", {"start": v(337.55, 166.25) * mm, "end": v(331.2, 166.25) * mm});
            skLineSegment(sketch, "E164.MirrorCS", {"start": v(337.55, 153.04) * mm, "end": v(331.2, 153.04) * mm});
            skLineSegment(sketch, "E165.MirrorCS", {"start": v(337.55, 166.25) * mm, "end": v(337.55, 153.04) * mm});
            skLineSegment(sketch, "E166.MirrorCS", {"start": v(337.55, 60.59) * mm, "end": v(337.55, 47.38) * mm});
            skLineSegment(sketch, "E167.MirrorCS", {"start": v(337.55, 166.25) * mm, "end": v(314.67, 166.25) * mm, "construction": true});
            skLineSegment(sketch, "E168.MirrorCS", {"start": v(331.2, 100.21) * mm, "end": v(331.2, 87) * mm});
            skLineSegment(sketch, "E169.MirrorCS", {"start": v(337.55, 166.25) * mm, "end": v(337.55, 139.83) * mm, "construction": true});
            skLineSegment(sketch, "E170.MirrorCS", {"start": v(337.55, 87) * mm, "end": v(337.55, 73.8) * mm});
            skLineSegment(sketch, "E171.MirrorCS", {"start": v(331.2, 126.63) * mm, "end": v(331.2, 113.42) * mm});
            skLineSegment(sketch, "E172.MirrorCS", {"start": v(331.2, 47.38) * mm, "end": v(331.2, 34.17) * mm});
            skLineSegment(sketch, "E173.MirrorCS", {"start": v(331.2, 153.04) * mm, "end": v(331.2, 139.83) * mm});
            skLineSegment(sketch, "E174.MirrorCS", {"start": v(337.55, 139.83) * mm, "end": v(337.55, 126.63) * mm});
            skLineSegment(sketch, "E175.MirrorCS", {"start": v(331.2, 73.8) * mm, "end": v(331.2, 60.59) * mm});
            skLineSegment(sketch, "E176.MirrorCS", {"start": v(337.55, 113.42) * mm, "end": v(337.55, 100.21) * mm});
            skLineSegment(sketch, "E177.MirrorCS", {"start": v(337.55, 34.17) * mm, "end": v(337.55, 20.96) * mm});
            skLineSegment(sketch, "E178.MirrorCS", {"start": v(331.2, 20.96) * mm, "end": v(331.2, 7.75) * mm});
            skLineSegment(sketch, "E179", {"start": v(232.14, -76.56) * mm, "end": v(238.49, -76.56) * mm});
            skLineSegment(sketch, "E180.0", {"start": v(334.37, -414.7) * mm, "end": v(334.37, -163.88) * mm});
            skLineSegment(sketch, "E180.1", {"start": v(235.31, -414.7) * mm, "end": v(334.37, -414.7) * mm});
            skLineSegment(sketch, "E180.2", {"start": v(235.31, -163.88) * mm, "end": v(235.31, -414.7) * mm});
            skArc(sketch, "E181", {"start": v(629.76, -31.89) * mm, "mid": v(593.75, -5.06) * mm, "end": v(563.57, -38.3) * mm});
            skArc(sketch, "E182", {"start": v(563.57, -38.3) * mm, "mid": v(567.07, -59.49) * mm, "end": v(577.2, -78.42) * mm});
            skLineSegment(sketch, "E183", {"start": v(630.38, -38.3) * mm, "end": v(563.57, -38.3) * mm, "construction": true});
            skLineSegment(sketch, "E184", {"start": v(630.38, -38.3) * mm, "end": v(630.38, -148.44) * mm, "construction": true});
            skLineSegment(sketch, "E185", {"start": v(577.2, -78.42) * mm, "end": v(600.15, -108.33) * mm});
            skArc(sketch, "E186", {"start": v(600.15, -108.33) * mm, "mid": v(615.36, -128.32) * mm, "end": v(630.38, -148.44) * mm});
            skArc(sketch, "E187.MirrorCS", {"start": v(631, -31.89) * mm, "mid": v(667.02, -5.06) * mm, "end": v(697.2, -38.3) * mm});
            skArc(sketch, "E188.MirrorCS", {"start": v(697.2, -38.3) * mm, "mid": v(693.7, -59.49) * mm, "end": v(683.58, -78.42) * mm});
            skLineSegment(sketch, "E189.MirrorCS", {"start": v(683.58, -78.42) * mm, "end": v(660.61, -108.33) * mm});
            skArc(sketch, "E190.MirrorCS", {"start": v(660.61, -108.33) * mm, "mid": v(645.41, -128.32) * mm, "end": v(630.38, -148.44) * mm});
            skArc(sketch, "E191", {"start": v(804.94, -4.9) * mm, "mid": v(778.34, -22.04) * mm, "end": v(782.95, -53.34) * mm});
            skLineSegment(sketch, "E192", {"start": v(663.79, -4.9) * mm, "end": v(697.2, -4.9) * mm, "construction": true});
            skLineSegment(sketch, "E193", {"start": v(563.57, -38.3) * mm, "end": v(563.57, 52.05) * mm});
            skLineSegment(sketch, "E194", {"start": v(697.2, -38.3) * mm, "end": v(697.2, 56.02) * mm});
            skLineSegment(sketch, "E195", {"start": v(738.14, -41.6) * mm, "end": v(738.14, 59.37) * mm});
            skLineSegment(sketch, "E196", {"start": v(871.74, -41.6) * mm, "end": v(871.74, 94.7) * mm});
            skLineSegment(sketch, "E197", {"start": v(926.31, -35.91) * mm, "end": v(926.31, 69.37) * mm});
            skLineSegment(sketch, "E198", {"start": v(1059.92, 72.98) * mm, "end": v(1059.92, -47.45) * mm});
            skLineSegment(sketch, "E199", {"start": v(1109.48, 67.2) * mm, "end": v(1109.48, -46.73) * mm});
            skLineSegment(sketch, "E200", {"start": v(1236.48, -4.9) * mm, "end": v(1236.48, -148.44) * mm, "construction": true});
            skLineSegment(sketch, "E201.trimOffspring", {"start": v(926.31, -4.9) * mm, "end": v(1059.92, -4.9) * mm, "construction": true});
            skLineSegment(sketch, "E202.trimOffspring", {"start": v(738.14, -4.9) * mm, "end": v(871.74, -4.9) * mm, "construction": true});
            skPoint(sketch, "E203", {"position": v(804.94, -4.9) * mm});
            skLineSegment(sketch, "E204", {"start": v(630.38, -148.44) * mm, "end": v(968.78, -148.44) * mm, "construction": true});
            skLineSegment(sketch, "E205", {"start": v(804.94, -4.9) * mm, "end": v(804.94, -187.35) * mm, "construction": true});
            skLineSegment(sketch, "E206", {"start": v(1109.48, -4.9) * mm, "end": v(1236.48, -4.9) * mm, "construction": true});
            skLineSegment(sketch, "E207", {"start": v(1172.98, -4.9) * mm, "end": v(1172.98, -181.5) * mm, "construction": true});
            skLineSegment(sketch, "E208", {"start": v(804.94, -148.44) * mm, "end": v(780.65, -148.44) * mm});
            skArc(sketch, "E209", {"start": v(780.65, -148.44) * mm, "mid": v(791.73, -129.72) * mm, "end": v(796.95, -108.6) * mm});
            skArc(sketch, "E210", {"start": v(781.09, -55.68) * mm, "mid": v(740.3, -92.48) * mm, "end": v(795.19, -90.3) * mm});
            skLineSegment(sketch, "E211", {"start": v(796.95, -108.6) * mm, "end": v(798.65, -91) * mm});
            skArc(sketch, "E212", {"start": v(798.65, -91) * mm, "mid": v(797.24, -89.09) * mm, "end": v(795.19, -90.3) * mm});
            skArc(sketch, "E213", {"start": v(785.35, -57.95) * mm, "mid": v(786.14, -57.78) * mm, "end": v(786.12, -56.97) * mm});
            skPoint(sketch, "E214", {"position": v(786.14, -57.78) * mm});
            skLineSegment(sketch, "E215", {"start": v(785.35, -57.95) * mm, "end": v(781.09, -55.68) * mm});
            skLineSegment(sketch, "E216", {"start": v(782.95, -53.34) * mm, "end": v(786.12, -56.97) * mm});
            skArc(sketch, "E217.MirrorCS", {"start": v(824.53, -57.95) * mm, "mid": v(823.74, -57.78) * mm, "end": v(823.76, -56.97) * mm});
            skArc(sketch, "E218.MirrorCS", {"start": v(811.23, -91) * mm, "mid": v(812.64, -89.09) * mm, "end": v(814.7, -90.3) * mm});
            skLineSegment(sketch, "E219.MirrorCS", {"start": v(826.93, -53.34) * mm, "end": v(823.76, -56.97) * mm});
            skLineSegment(sketch, "E220.MirrorCS", {"start": v(824.53, -57.95) * mm, "end": v(828.8, -55.68) * mm});
            skLineSegment(sketch, "E221.MirrorCS", {"start": v(804.94, -148.44) * mm, "end": v(829.23, -148.44) * mm});
            skArc(sketch, "E222.MirrorCS", {"start": v(804.94, -4.9) * mm, "mid": v(831.54, -22.04) * mm, "end": v(826.93, -53.34) * mm});
            skLineSegment(sketch, "E223.MirrorCS", {"start": v(812.93, -108.6) * mm, "end": v(811.23, -91) * mm});
            skPoint(sketch, "E224.MirrorP", {"position": v(823.74, -57.78) * mm});
            skArc(sketch, "E225.MirrorCS", {"start": v(828.8, -55.68) * mm, "mid": v(869.58, -92.48) * mm, "end": v(814.7, -90.3) * mm});
            skArc(sketch, "E226.MirrorCS", {"start": v(829.23, -148.44) * mm, "mid": v(818.15, -129.72) * mm, "end": v(812.93, -108.6) * mm});
            skLineSegment(sketch, "E227", {"start": v(993.42, -125.25) * mm, "end": v(993.42, -4.9) * mm, "construction": true});
            skLineSegment(sketch, "E228", {"start": v(1018.06, -148.44) * mm, "end": v(968.78, -148.44) * mm});
            skArc(sketch, "E229", {"start": v(968.78, -148.44) * mm, "mid": v(979.82, -130.69) * mm, "end": v(985.52, -110.58) * mm});
            skPoint(sketch, "E230", {"position": v(956.65, -103.53) * mm});
            skLineSegment(sketch, "E231", {"start": v(985.52, -110.58) * mm, "end": v(988.2, -91.07) * mm});
            skArc(sketch, "E232", {"start": v(988.2, -91.07) * mm, "mid": v(986.55, -89.06) * mm, "end": v(984.66, -90.83) * mm});
            skLineSegment(sketch, "E233", {"start": v(984.66, -90.83) * mm, "end": v(926.31, -90.83) * mm, "construction": true});
            skEllipticalArc(sketch, "E234", {});
            skArc(sketch, "E235", {"start": v(943.39, -55.37) * mm, "mid": v(931.88, -71.2) * mm, "end": v(926.4, -90) * mm});
            skLineSegment(sketch, "E236", {"start": v(943.39, -55.37) * mm, "end": v(975.57, -24.15) * mm});
            skPoint(sketch, "E237.visualSharp", {"position": v(926.31, -90.83) * mm});
            skArc(sketch, "E237.filletArc", {"start": v(926.4, -90) * mm, "mid": v(926.33, -90.88) * mm, "end": v(926.32, -91.75) * mm});
            skArc(sketch, "E238", {"start": v(975.57, -24.15) * mm, "mid": v(984.66, -14.69) * mm, "end": v(993.42, -4.9) * mm});
            skArc(sketch, "E239.MirrorCS", {"start": v(1011.26, -24.15) * mm, "mid": v(1002.17, -14.69) * mm, "end": v(993.42, -4.9) * mm});
            skLineSegment(sketch, "E240.MirrorCS", {"start": v(1043.44, -55.37) * mm, "end": v(1011.26, -24.15) * mm});
            skArc(sketch, "E241.MirrorCS", {"start": v(1043.44, -55.37) * mm, "mid": v(1054.95, -71.2) * mm, "end": v(1060.43, -90) * mm});
            skEllipticalArc(sketch, "E242.MirrorCS", {});
            skArc(sketch, "E243.MirrorCS", {"start": v(998.64, -91.07) * mm, "mid": v(1000.28, -89.06) * mm, "end": v(1002.18, -90.83) * mm});
            skLineSegment(sketch, "E244.MirrorCS", {"start": v(1001.3, -110.58) * mm, "end": v(998.64, -91.07) * mm});
            skArc(sketch, "E245.MirrorCS", {"start": v(1018.06, -148.44) * mm, "mid": v(1007.01, -130.69) * mm, "end": v(1001.3, -110.58) * mm});
            skLineSegment(sketch, "E246.trimOffspring", {"start": v(1018.06, -148.44) * mm, "end": v(1330.15, -148.44) * mm, "construction": true});
            skPoint(sketch, "E247.MirrorCS.start.orphan", {"position": v(993.42, -148.44) * mm});
            skPoint(sketch, "E248.orphan", {"position": v(979.5, -148.44) * mm});
            skPoint(sketch, "E249.orphan", {"position": v(988.23, -90.83) * mm});
            skPoint(sketch, "E250.orphan", {"position": v(998.6, -90.83) * mm});
            skArc(sketch, "E251.MirrorCS", {"start": v(1060.43, -90) * mm, "mid": v(1060.5, -90.88) * mm, "end": v(1060.5, -91.75) * mm});
            skPoint(sketch, "E252", {"position": v(1236.48, -76.67) * mm});
            skArc(sketch, "E253", {"start": v(1172.98, -4.9) * mm, "mid": v(1201.71, -43.46) * mm, "end": v(1236.48, -76.67) * mm});
            skLineSegment(sketch, "E254", {"start": v(1236.48, -76.67) * mm, "end": v(1197.48, -76.67) * mm, "construction": true});
            skArc(sketch, "E255.MirrorCS", {"start": v(1172.98, -148.44) * mm, "mid": v(1201.71, -109.88) * mm, "end": v(1236.48, -76.67) * mm});
            skArc(sketch, "E256.MirrorCS", {"start": v(1172.98, -4.9) * mm, "mid": v(1144.25, -43.46) * mm, "end": v(1109.48, -76.67) * mm});
            skArc(sketch, "E257.MirrorCS", {"start": v(1172.98, -148.44) * mm, "mid": v(1144.25, -109.88) * mm, "end": v(1109.48, -76.67) * mm});
            skLineSegment(sketch, "E258", {"start": v(238.49, -18.66) * mm, "end": v(232.14, -18.66) * mm});
            skLineSegment(sketch, "E259", {"start": v(232.14, -31.87) * mm, "end": v(238.49, -31.87) * mm});
            skLineSegment(sketch, "E260", {"start": v(337.55, 47.38) * mm, "end": v(331.2, 47.38) * mm});
            skLineSegment(sketch, "E261", {"start": v(331.2, 73.8) * mm, "end": v(337.55, 73.8) * mm});
            skLineSegment(sketch, "E262", {"start": v(337.55, 100.21) * mm, "end": v(331.2, 100.21) * mm});
            skLineSegment(sketch, "E263", {"start": v(331.2, 34.17) * mm, "end": v(337.55, 34.17) * mm});
            skLineSegment(sketch, "E264", {"start": v(337.55, 20.96) * mm, "end": v(331.2, 20.96) * mm});
            skLineSegment(sketch, "E265", {"start": v(337.55, -5.45) * mm, "end": v(331.2, -5.45) * mm});
            skLineSegment(sketch, "E266", {"start": v(337.55, -31.87) * mm, "end": v(331.2, -31.87) * mm});
            skArc(sketch, "E267", {"start": v(629.76, -31.89) * mm, "mid": v(630.38, -32.4) * mm, "end": v(631, -31.89) * mm});
            skPoint(sketch, "E268.orphan", {"position": v(630.38, -38.3) * mm});
            skLineSegment(sketch, "E269", {"start": v(337.55, -18.66) * mm, "end": v(331.2, -18.66) * mm});
            skLineSegment(sketch, "E270", {"start": v(232.14, 87) * mm, "end": v(238.49, 87) * mm});
            skLineSegment(sketch, "E271", {"start": v(331.2, 87) * mm, "end": v(337.55, 87) * mm});
            skLineSegment(sketch, "E272", {"start": v(331.2, 181.5) * mm, "end": v(331.2, 166.25) * mm});
            skLineSegment(sketch, "E273", {"start": v(331.2, 139.83) * mm, "end": v(337.55, 139.83) * mm});
            skLineSegment(sketch, "E274", {"start": v(241.03, -76.56) * mm, "end": v(283.57, -76.56) * mm});
            skLineSegment(sketch, "E275.direction1", {"start": v(241.03, -76.56) * mm, "end": v(279.74, -76.56) * mm, "construction": true});
            skLineSegment(sketch, "E276", {"start": v(334.37, -163.88) * mm, "end": v(337.55, -163.88) * mm});
            skLineSegment(sketch, "E277", {"start": v(235.31, -163.88) * mm, "end": v(232.14, -163.88) * mm});
            skPoint(sketch, "E278.orphan", {"position": v(234.71, -163.88) * mm});
            skLineSegment(sketch, "E279.MirrorCS", {"start": v(337.55, -76.56) * mm, "end": v(331.2, -76.56) * mm});
            skPoint(sketch, "E280.MirrorP", {"position": v(334.97, -163.88) * mm});
            skLineSegment(sketch, "E281.MirrorCS", {"start": v(337.55, -76.56) * mm, "end": v(337.55, -163.88) * mm});
            skLineSegment(sketch, "E282.MirrorCS", {"start": v(331.2, -58.29) * mm, "end": v(331.2, -76.56) * mm});
            skLineSegment(sketch, "E283", {"start": v(232.14, -77.52) * mm, "end": v(257.22, -78.4) * mm});
            skPoint(sketch, "E283.endSnap0", {"position": v(260.4, -76.56) * mm});
            skLineSegment(sketch, "E284", {"start": v(257.22, -79.15) * mm, "end": v(232.14, -80.03) * mm});
            skLineSegment(sketch, "E285", {"start": v(259.76, -78.4) * mm, "end": v(284.84, -77.52) * mm});
            skLineSegment(sketch, "E286", {"start": v(284.84, -80.03) * mm, "end": v(259.76, -79.15) * mm});
            skLineSegment(sketch, "E287", {"start": v(262.3, -77.3) * mm, "end": v(283.57, -76.56) * mm});
            skLineSegment(sketch, "E288", {"start": v(241.03, -76.56) * mm, "end": v(262.3, -77.3) * mm});
            skPoint(sketch, "E289.orphan", {"position": v(241.04, -76.56) * mm});
            skLineSegment(sketch, "E290", {"start": v(257.22, -78.4) * mm, "end": v(257.22, -79.15) * mm});
            skLineSegment(sketch, "E291", {"start": v(259.76, -78.4) * mm, "end": v(259.76, -79.15) * mm});
            skLineSegment(sketch, "E292", {"start": v(232.14, -77.52) * mm, "end": v(284.84, -77.52) * mm, "construction": true});
            skLineSegment(sketch, "E293", {"start": v(234.68, -81.21) * mm, "end": v(258.49, -80.38) * mm});
            skLineSegment(sketch, "E294", {"start": v(258.49, -80.38) * mm, "end": v(283.57, -81.26) * mm});
            skLineSegment(sketch, "E295", {"start": v(283.57, -81.26) * mm, "end": v(283.57, -81.93) * mm});
            skLineSegment(sketch, "E296", {"start": v(283.57, -81.93) * mm, "end": v(258.49, -82.8) * mm});
            skLineSegment(sketch, "E297", {"start": v(258.49, -82.8) * mm, "end": v(234.68, -81.97) * mm});
            skLineSegment(sketch, "E298", {"start": v(234.68, -81.97) * mm, "end": v(234.68, -81.21) * mm});
            skPoint(sketch, "E299", {"position": v(259.76, -78.77) * mm});
            skPoint(sketch, "E300", {"position": v(283.57, -81.6) * mm});
            skPoint(sketch, "E301.0.1.0", {"position": v(241.04, -88.5) * mm});
            skPoint(sketch, "E301.0.1.6", {"position": v(261.03, -90.66) * mm});
            skPoint(sketch, "E301.0.1.8", {"position": v(260.4, -88.5) * mm});
            skPoint(sketch, "E301.0.2.0", {"position": v(241.04, -100.43) * mm});
            skPoint(sketch, "E301.0.2.8", {"position": v(260.4, -100.43) * mm});
            skLineSegment(sketch, "E301.direction2", {"start": v(232.14, -80.03) * mm, "end": v(232.14, -91.97) * mm, "construction": true});
            skPoint(sketch, "E302.orphan", {"position": v(237.85, -163.88) * mm});
            skLineSegment(sketch, "E303", {"start": v(259.76, -78.4) * mm, "end": v(257.22, -78.4) * mm, "construction": true});
            skLineSegment(sketch, "E304.0.1.0", {"start": v(232.14, -83.15) * mm, "end": v(257.22, -84.03) * mm});
            skLineSegment(sketch, "E304.0.1.1", {"start": v(257.22, -84.8) * mm, "end": v(232.14, -85.67) * mm});
            skLineSegment(sketch, "E304.0.1.2", {"start": v(257.22, -84.03) * mm, "end": v(257.22, -84.8) * mm});
            skLineSegment(sketch, "E304.0.1.3", {"start": v(259.76, -84.03) * mm, "end": v(259.76, -84.8) * mm});
            skLineSegment(sketch, "E304.0.1.4", {"start": v(259.76, -84.03) * mm, "end": v(284.84, -83.15) * mm});
            skLineSegment(sketch, "E304.0.1.5", {"start": v(284.84, -85.67) * mm, "end": v(259.76, -84.8) * mm});
            skLineSegment(sketch, "E304.0.1.6", {"start": v(258.49, -86.02) * mm, "end": v(283.57, -86.9) * mm});
            skLineSegment(sketch, "E304.0.1.7", {"start": v(234.68, -86.85) * mm, "end": v(258.49, -86.02) * mm});
            skLineSegment(sketch, "E304.0.1.8", {"start": v(258.49, -88.44) * mm, "end": v(234.68, -87.61) * mm});
            skLineSegment(sketch, "E304.0.1.9", {"start": v(283.57, -87.57) * mm, "end": v(258.49, -88.44) * mm});
            skLineSegment(sketch, "E304.0.1.10", {"start": v(234.68, -87.61) * mm, "end": v(234.68, -86.85) * mm});
            skLineSegment(sketch, "E304.0.1.11", {"start": v(283.57, -86.9) * mm, "end": v(283.57, -87.57) * mm});
            skLineSegment(sketch, "E304.0.2.0", {"start": v(232.14, -88.8) * mm, "end": v(257.22, -89.67) * mm});
            skLineSegment(sketch, "E304.0.2.1", {"start": v(257.22, -90.43) * mm, "end": v(232.14, -91.3) * mm});
            skLineSegment(sketch, "E304.0.2.2", {"start": v(257.22, -89.67) * mm, "end": v(257.22, -90.43) * mm});
            skLineSegment(sketch, "E304.0.2.3", {"start": v(259.76, -89.67) * mm, "end": v(259.76, -90.43) * mm});
            skLineSegment(sketch, "E304.0.2.4", {"start": v(259.76, -89.67) * mm, "end": v(284.84, -88.8) * mm});
            skLineSegment(sketch, "E304.0.2.5", {"start": v(284.84, -91.3) * mm, "end": v(259.76, -90.43) * mm});
            skLineSegment(sketch, "E304.0.2.6", {"start": v(258.49, -91.66) * mm, "end": v(283.57, -92.53) * mm});
            skLineSegment(sketch, "E304.0.2.7", {"start": v(234.68, -92.49) * mm, "end": v(258.49, -91.66) * mm});
            skLineSegment(sketch, "E304.0.2.8", {"start": v(258.49, -94.08) * mm, "end": v(234.68, -93.25) * mm});
            skLineSegment(sketch, "E304.0.2.9", {"start": v(283.57, -93.2) * mm, "end": v(258.49, -94.08) * mm});
            skLineSegment(sketch, "E304.0.2.10", {"start": v(234.68, -93.25) * mm, "end": v(234.68, -92.49) * mm});
            skLineSegment(sketch, "E304.0.2.11", {"start": v(283.57, -92.53) * mm, "end": v(283.57, -93.2) * mm});
            skLineSegment(sketch, "E304.0.3.0", {"start": v(232.14, -94.43) * mm, "end": v(257.22, -95.3) * mm});
            skLineSegment(sketch, "E304.0.3.1", {"start": v(257.22, -96.07) * mm, "end": v(232.14, -96.95) * mm});
            skLineSegment(sketch, "E304.0.3.2", {"start": v(257.22, -95.3) * mm, "end": v(257.22, -96.07) * mm});
            skLineSegment(sketch, "E304.0.3.3", {"start": v(259.76, -95.3) * mm, "end": v(259.76, -96.07) * mm});
            skLineSegment(sketch, "E304.0.3.4", {"start": v(259.76, -95.3) * mm, "end": v(284.84, -94.43) * mm});
            skLineSegment(sketch, "E304.0.3.5", {"start": v(284.84, -96.95) * mm, "end": v(259.76, -96.07) * mm});
            skLineSegment(sketch, "E304.0.3.6", {"start": v(258.49, -97.3) * mm, "end": v(283.57, -98.17) * mm});
            skLineSegment(sketch, "E304.0.3.7", {"start": v(234.68, -98.13) * mm, "end": v(258.49, -97.3) * mm});
            skLineSegment(sketch, "E304.0.3.8", {"start": v(258.49, -99.72) * mm, "end": v(234.68, -98.89) * mm});
            skLineSegment(sketch, "E304.0.3.9", {"start": v(283.57, -98.85) * mm, "end": v(258.49, -99.72) * mm});
            skLineSegment(sketch, "E304.0.3.10", {"start": v(234.68, -98.89) * mm, "end": v(234.68, -98.13) * mm});
            skLineSegment(sketch, "E304.0.3.11", {"start": v(283.57, -98.17) * mm, "end": v(283.57, -98.85) * mm});
            skLineSegment(sketch, "E304.0.4.0", {"start": v(232.14, -100.07) * mm, "end": v(257.22, -100.95) * mm});
            skLineSegment(sketch, "E304.0.4.1", {"start": v(257.22, -101.7) * mm, "end": v(232.14, -102.58) * mm});
            skLineSegment(sketch, "E304.0.4.2", {"start": v(257.22, -100.95) * mm, "end": v(257.22, -101.7) * mm});
            skLineSegment(sketch, "E304.0.4.3", {"start": v(259.76, -100.95) * mm, "end": v(259.76, -101.7) * mm});
            skLineSegment(sketch, "E304.0.4.4", {"start": v(259.76, -100.95) * mm, "end": v(284.84, -100.07) * mm});
            skLineSegment(sketch, "E304.0.4.5", {"start": v(284.84, -102.58) * mm, "end": v(259.76, -101.7) * mm});
            skLineSegment(sketch, "E304.0.4.6", {"start": v(258.49, -102.93) * mm, "end": v(283.57, -103.81) * mm});
            skLineSegment(sketch, "E304.0.4.7", {"start": v(234.68, -103.77) * mm, "end": v(258.49, -102.93) * mm});
            skLineSegment(sketch, "E304.0.4.8", {"start": v(258.49, -105.36) * mm, "end": v(234.68, -104.53) * mm});
            skLineSegment(sketch, "E304.0.4.9", {"start": v(283.57, -104.48) * mm, "end": v(258.49, -105.36) * mm});
            skLineSegment(sketch, "E304.0.4.10", {"start": v(234.68, -104.53) * mm, "end": v(234.68, -103.77) * mm});
            skLineSegment(sketch, "E304.0.4.11", {"start": v(283.57, -103.81) * mm, "end": v(283.57, -104.48) * mm});
            skLineSegment(sketch, "E304.0.5.0", {"start": v(232.14, -105.7) * mm, "end": v(257.22, -106.59) * mm});
            skLineSegment(sketch, "E304.0.5.1", {"start": v(257.22, -107.35) * mm, "end": v(232.14, -108.22) * mm});
            skLineSegment(sketch, "E304.0.5.2", {"start": v(257.22, -106.59) * mm, "end": v(257.22, -107.35) * mm});
            skLineSegment(sketch, "E304.0.5.3", {"start": v(259.76, -106.59) * mm, "end": v(259.76, -107.35) * mm});
            skLineSegment(sketch, "E304.0.5.4", {"start": v(259.76, -106.59) * mm, "end": v(284.84, -105.7) * mm});
            skLineSegment(sketch, "E304.0.5.5", {"start": v(284.84, -108.22) * mm, "end": v(259.76, -107.35) * mm});
            skLineSegment(sketch, "E304.0.5.6", {"start": v(258.49, -108.57) * mm, "end": v(283.57, -109.45) * mm});
            skLineSegment(sketch, "E304.0.5.7", {"start": v(234.68, -109.4) * mm, "end": v(258.49, -108.57) * mm});
            skLineSegment(sketch, "E304.0.5.8", {"start": v(258.49, -111) * mm, "end": v(234.68, -110.17) * mm});
            skLineSegment(sketch, "E304.0.5.9", {"start": v(283.57, -110.12) * mm, "end": v(258.49, -111) * mm});
            skLineSegment(sketch, "E304.0.5.10", {"start": v(234.68, -110.17) * mm, "end": v(234.68, -109.4) * mm});
            skLineSegment(sketch, "E304.0.5.11", {"start": v(283.57, -109.45) * mm, "end": v(283.57, -110.12) * mm});
            skLineSegment(sketch, "E304.0.6.0", {"start": v(232.14, -111.35) * mm, "end": v(257.22, -112.22) * mm});
            skLineSegment(sketch, "E304.0.6.1", {"start": v(257.22, -112.99) * mm, "end": v(232.14, -113.86) * mm});
            skLineSegment(sketch, "E304.0.6.2", {"start": v(257.22, -112.22) * mm, "end": v(257.22, -112.99) * mm});
            skLineSegment(sketch, "E304.0.6.3", {"start": v(259.76, -112.22) * mm, "end": v(259.76, -112.99) * mm});
            skLineSegment(sketch, "E304.0.6.4", {"start": v(259.76, -112.22) * mm, "end": v(284.84, -111.35) * mm});
            skLineSegment(sketch, "E304.0.6.5", {"start": v(284.84, -113.86) * mm, "end": v(259.76, -112.99) * mm});
            skLineSegment(sketch, "E304.0.6.6", {"start": v(258.49, -114.21) * mm, "end": v(283.57, -115.09) * mm});
            skLineSegment(sketch, "E304.0.6.7", {"start": v(234.68, -115.04) * mm, "end": v(258.49, -114.21) * mm});
            skLineSegment(sketch, "E304.0.6.8", {"start": v(258.49, -116.64) * mm, "end": v(234.68, -115.8) * mm});
            skLineSegment(sketch, "E304.0.6.9", {"start": v(283.57, -115.76) * mm, "end": v(258.49, -116.64) * mm});
            skLineSegment(sketch, "E304.0.6.10", {"start": v(234.68, -115.8) * mm, "end": v(234.68, -115.04) * mm});
            skLineSegment(sketch, "E304.0.6.11", {"start": v(283.57, -115.09) * mm, "end": v(283.57, -115.76) * mm});
            skLineSegment(sketch, "E304.0.7.0", {"start": v(232.14, -116.99) * mm, "end": v(257.22, -117.86) * mm});
            skLineSegment(sketch, "E304.0.7.1", {"start": v(257.22, -118.62) * mm, "end": v(232.14, -119.5) * mm});
            skLineSegment(sketch, "E304.0.7.2", {"start": v(257.22, -117.86) * mm, "end": v(257.22, -118.62) * mm});
            skLineSegment(sketch, "E304.0.7.3", {"start": v(259.76, -117.86) * mm, "end": v(259.76, -118.62) * mm});
            skLineSegment(sketch, "E304.0.7.4", {"start": v(259.76, -117.86) * mm, "end": v(284.84, -116.99) * mm});
            skLineSegment(sketch, "E304.0.7.5", {"start": v(284.84, -119.5) * mm, "end": v(259.76, -118.62) * mm});
            skLineSegment(sketch, "E304.0.7.6", {"start": v(258.49, -119.85) * mm, "end": v(283.57, -120.73) * mm});
            skLineSegment(sketch, "E304.0.7.7", {"start": v(234.68, -120.68) * mm, "end": v(258.49, -119.85) * mm});
            skLineSegment(sketch, "E304.0.7.8", {"start": v(258.49, -122.28) * mm, "end": v(234.68, -121.44) * mm});
            skLineSegment(sketch, "E304.0.7.9", {"start": v(283.57, -121.4) * mm, "end": v(258.49, -122.28) * mm});
            skLineSegment(sketch, "E304.0.7.10", {"start": v(234.68, -121.44) * mm, "end": v(234.68, -120.68) * mm});
            skLineSegment(sketch, "E304.0.7.11", {"start": v(283.57, -120.73) * mm, "end": v(283.57, -121.4) * mm});
            skLineSegment(sketch, "E304.0.8.0", {"start": v(232.14, -122.63) * mm, "end": v(257.22, -123.5) * mm});
            skLineSegment(sketch, "E304.0.8.1", {"start": v(257.22, -124.26) * mm, "end": v(232.14, -125.14) * mm});
            skLineSegment(sketch, "E304.0.8.2", {"start": v(257.22, -123.5) * mm, "end": v(257.22, -124.26) * mm});
            skLineSegment(sketch, "E304.0.8.3", {"start": v(259.76, -123.5) * mm, "end": v(259.76, -124.26) * mm});
            skLineSegment(sketch, "E304.0.8.4", {"start": v(259.76, -123.5) * mm, "end": v(284.84, -122.63) * mm});
            skLineSegment(sketch, "E304.0.8.5", {"start": v(284.84, -125.14) * mm, "end": v(259.76, -124.26) * mm});
            skLineSegment(sketch, "E304.0.8.6", {"start": v(258.49, -125.5) * mm, "end": v(283.57, -126.37) * mm});
            skLineSegment(sketch, "E304.0.8.7", {"start": v(234.68, -126.32) * mm, "end": v(258.49, -125.5) * mm});
            skLineSegment(sketch, "E304.0.8.8", {"start": v(258.49, -127.92) * mm, "end": v(234.68, -127.08) * mm});
            skLineSegment(sketch, "E304.0.8.9", {"start": v(283.57, -127.04) * mm, "end": v(258.49, -127.92) * mm});
            skLineSegment(sketch, "E304.0.8.10", {"start": v(234.68, -127.08) * mm, "end": v(234.68, -126.32) * mm});
            skLineSegment(sketch, "E304.0.8.11", {"start": v(283.57, -126.37) * mm, "end": v(283.57, -127.04) * mm});
            skLineSegment(sketch, "E304.0.9.0", {"start": v(232.14, -128.26) * mm, "end": v(257.22, -129.14) * mm});
            skLineSegment(sketch, "E304.0.9.1", {"start": v(257.22, -129.9) * mm, "end": v(232.14, -130.78) * mm});
            skLineSegment(sketch, "E304.0.9.2", {"start": v(257.22, -129.14) * mm, "end": v(257.22, -129.9) * mm});
            skLineSegment(sketch, "E304.0.9.3", {"start": v(259.76, -129.14) * mm, "end": v(259.76, -129.9) * mm});
            skLineSegment(sketch, "E304.0.9.4", {"start": v(259.76, -129.14) * mm, "end": v(284.84, -128.26) * mm});
            skLineSegment(sketch, "E304.0.9.5", {"start": v(284.84, -130.78) * mm, "end": v(259.76, -129.9) * mm});
            skLineSegment(sketch, "E304.0.9.6", {"start": v(258.49, -131.13) * mm, "end": v(283.57, -132) * mm});
            skLineSegment(sketch, "E304.0.9.7", {"start": v(234.68, -131.96) * mm, "end": v(258.49, -131.13) * mm});
            skLineSegment(sketch, "E304.0.9.8", {"start": v(258.49, -133.55) * mm, "end": v(234.68, -132.72) * mm});
            skLineSegment(sketch, "E304.0.9.9", {"start": v(283.57, -132.68) * mm, "end": v(258.49, -133.55) * mm});
            skLineSegment(sketch, "E304.0.9.10", {"start": v(234.68, -132.72) * mm, "end": v(234.68, -131.96) * mm});
            skLineSegment(sketch, "E304.0.9.11", {"start": v(283.57, -132) * mm, "end": v(283.57, -132.68) * mm});
            skLineSegment(sketch, "E304.0.10.0", {"start": v(232.14, -133.9) * mm, "end": v(257.22, -134.78) * mm});
            skLineSegment(sketch, "E304.0.10.1", {"start": v(257.22, -135.54) * mm, "end": v(232.14, -136.42) * mm});
            skLineSegment(sketch, "E304.0.10.2", {"start": v(257.22, -134.78) * mm, "end": v(257.22, -135.54) * mm});
            skLineSegment(sketch, "E304.0.10.3", {"start": v(259.76, -134.78) * mm, "end": v(259.76, -135.54) * mm});
            skLineSegment(sketch, "E304.0.10.4", {"start": v(259.76, -134.78) * mm, "end": v(284.84, -133.9) * mm});
            skLineSegment(sketch, "E304.0.10.5", {"start": v(284.84, -136.42) * mm, "end": v(259.76, -135.54) * mm});
            skLineSegment(sketch, "E304.0.10.6", {"start": v(258.49, -136.77) * mm, "end": v(283.57, -137.64) * mm});
            skLineSegment(sketch, "E304.0.10.7", {"start": v(234.68, -137.6) * mm, "end": v(258.49, -136.77) * mm});
            skLineSegment(sketch, "E304.0.10.8", {"start": v(258.49, -139.2) * mm, "end": v(234.68, -138.36) * mm});
            skLineSegment(sketch, "E304.0.10.9", {"start": v(283.57, -138.32) * mm, "end": v(258.49, -139.2) * mm});
            skLineSegment(sketch, "E304.0.10.10", {"start": v(234.68, -138.36) * mm, "end": v(234.68, -137.6) * mm});
            skLineSegment(sketch, "E304.0.10.11", {"start": v(283.57, -137.64) * mm, "end": v(283.57, -138.32) * mm});
            skLineSegment(sketch, "E304.0.11.0", {"start": v(232.14, -139.54) * mm, "end": v(257.22, -140.42) * mm});
            skLineSegment(sketch, "E304.0.11.1", {"start": v(257.22, -141.18) * mm, "end": v(232.14, -142.06) * mm});
            skLineSegment(sketch, "E304.0.11.2", {"start": v(257.22, -140.42) * mm, "end": v(257.22, -141.18) * mm});
            skLineSegment(sketch, "E304.0.11.3", {"start": v(259.76, -140.42) * mm, "end": v(259.76, -141.18) * mm});
            skLineSegment(sketch, "E304.0.11.4", {"start": v(259.76, -140.42) * mm, "end": v(284.84, -139.54) * mm});
            skLineSegment(sketch, "E304.0.11.5", {"start": v(284.84, -142.06) * mm, "end": v(259.76, -141.18) * mm});
            skLineSegment(sketch, "E304.0.11.6", {"start": v(258.49, -142.4) * mm, "end": v(283.57, -143.28) * mm});
            skLineSegment(sketch, "E304.0.11.7", {"start": v(234.68, -143.24) * mm, "end": v(258.49, -142.4) * mm});
            skLineSegment(sketch, "E304.0.11.8", {"start": v(258.49, -144.83) * mm, "end": v(234.68, -144) * mm});
            skLineSegment(sketch, "E304.0.11.9", {"start": v(283.57, -143.96) * mm, "end": v(258.49, -144.83) * mm});
            skLineSegment(sketch, "E304.0.11.10", {"start": v(234.68, -144) * mm, "end": v(234.68, -143.24) * mm});
            skLineSegment(sketch, "E304.0.11.11", {"start": v(283.57, -143.28) * mm, "end": v(283.57, -143.96) * mm});
            skLineSegment(sketch, "E304.0.12.0", {"start": v(232.14, -145.18) * mm, "end": v(257.22, -146.06) * mm});
            skLineSegment(sketch, "E304.0.12.1", {"start": v(257.22, -146.82) * mm, "end": v(232.14, -147.7) * mm});
            skLineSegment(sketch, "E304.0.12.2", {"start": v(257.22, -146.06) * mm, "end": v(257.22, -146.82) * mm});
            skLineSegment(sketch, "E304.0.12.3", {"start": v(259.76, -146.06) * mm, "end": v(259.76, -146.82) * mm});
            skLineSegment(sketch, "E304.0.12.4", {"start": v(259.76, -146.06) * mm, "end": v(284.84, -145.18) * mm});
            skLineSegment(sketch, "E304.0.12.5", {"start": v(284.84, -147.7) * mm, "end": v(259.76, -146.82) * mm});
            skLineSegment(sketch, "E304.0.12.6", {"start": v(258.49, -148.05) * mm, "end": v(283.57, -148.92) * mm});
            skLineSegment(sketch, "E304.0.12.7", {"start": v(234.68, -148.88) * mm, "end": v(258.49, -148.05) * mm});
            skLineSegment(sketch, "E304.0.12.8", {"start": v(258.49, -150.47) * mm, "end": v(234.68, -149.64) * mm});
            skLineSegment(sketch, "E304.0.12.9", {"start": v(283.57, -149.6) * mm, "end": v(258.49, -150.47) * mm});
            skLineSegment(sketch, "E304.0.12.10", {"start": v(234.68, -149.64) * mm, "end": v(234.68, -148.88) * mm});
            skLineSegment(sketch, "E304.0.12.11", {"start": v(283.57, -148.92) * mm, "end": v(283.57, -149.6) * mm});
            skLineSegment(sketch, "E304.0.13.0", {"start": v(232.14, -150.82) * mm, "end": v(257.22, -151.7) * mm});
            skLineSegment(sketch, "E304.0.13.1", {"start": v(257.22, -152.46) * mm, "end": v(232.14, -153.33) * mm});
            skLineSegment(sketch, "E304.0.13.2", {"start": v(257.22, -151.7) * mm, "end": v(257.22, -152.46) * mm});
            skLineSegment(sketch, "E304.0.13.3", {"start": v(259.76, -151.7) * mm, "end": v(259.76, -152.46) * mm});
            skLineSegment(sketch, "E304.0.13.4", {"start": v(259.76, -151.7) * mm, "end": v(284.84, -150.82) * mm});
            skLineSegment(sketch, "E304.0.13.5", {"start": v(284.84, -153.33) * mm, "end": v(259.76, -152.46) * mm});
            skLineSegment(sketch, "E304.0.13.6", {"start": v(258.49, -153.68) * mm, "end": v(283.57, -154.56) * mm});
            skLineSegment(sketch, "E304.0.13.7", {"start": v(234.68, -154.52) * mm, "end": v(258.49, -153.68) * mm});
            skLineSegment(sketch, "E304.0.13.8", {"start": v(258.49, -156.1) * mm, "end": v(234.68, -155.28) * mm});
            skLineSegment(sketch, "E304.0.13.9", {"start": v(283.57, -155.23) * mm, "end": v(258.49, -156.1) * mm});
            skLineSegment(sketch, "E304.0.13.10", {"start": v(234.68, -155.28) * mm, "end": v(234.68, -154.52) * mm});
            skLineSegment(sketch, "E304.0.13.11", {"start": v(283.57, -154.56) * mm, "end": v(283.57, -155.23) * mm});
            skLineSegment(sketch, "E304.0.14.0", {"start": v(232.14, -156.46) * mm, "end": v(257.22, -157.33) * mm});
            skLineSegment(sketch, "E304.0.14.1", {"start": v(257.22, -158.1) * mm, "end": v(232.14, -158.97) * mm});
            skLineSegment(sketch, "E304.0.14.2", {"start": v(257.22, -157.33) * mm, "end": v(257.22, -158.1) * mm});
            skLineSegment(sketch, "E304.0.14.3", {"start": v(259.76, -157.33) * mm, "end": v(259.76, -158.1) * mm});
            skLineSegment(sketch, "E304.0.14.4", {"start": v(259.76, -157.33) * mm, "end": v(284.84, -156.46) * mm});
            skLineSegment(sketch, "E304.0.14.5", {"start": v(284.84, -158.97) * mm, "end": v(259.76, -158.1) * mm});
            skLineSegment(sketch, "E304.0.14.6", {"start": v(258.49, -159.32) * mm, "end": v(283.57, -160.2) * mm});
            skLineSegment(sketch, "E304.0.14.7", {"start": v(234.68, -160.15) * mm, "end": v(258.49, -159.32) * mm});
            skLineSegment(sketch, "E304.0.14.8", {"start": v(258.49, -161.75) * mm, "end": v(234.68, -160.92) * mm});
            skLineSegment(sketch, "E304.0.14.9", {"start": v(283.57, -160.87) * mm, "end": v(258.49, -161.75) * mm});
            skLineSegment(sketch, "E304.0.14.10", {"start": v(234.68, -160.92) * mm, "end": v(234.68, -160.15) * mm});
            skLineSegment(sketch, "E304.0.14.11", {"start": v(283.57, -160.2) * mm, "end": v(283.57, -160.87) * mm});
            skLineSegment(sketch, "E304.direction1", {"start": v(232.14, -77.52) * mm, "end": v(257.54, -77.52) * mm, "construction": true});
            skLineSegment(sketch, "E304.direction2", {"start": v(232.14, -77.52) * mm, "end": v(232.14, -83.15) * mm, "construction": true});
            skLineSegment(sketch, "E305", {"start": v(232.14, -162.6) * mm, "end": v(257.22, -163.48) * mm});
            skLineSegment(sketch, "E306", {"start": v(257.22, -163.48) * mm, "end": v(232.14, -163.48) * mm});
            skLineSegment(sketch, "E307", {"start": v(284.84, -162.6) * mm, "end": v(259.76, -163.48) * mm});
            skLineSegment(sketch, "E308", {"start": v(259.76, -163.48) * mm, "end": v(284.84, -163.48) * mm});
            skLineSegment(sketch, "E309.MirrorCS", {"start": v(309.92, -89.67) * mm, "end": v(309.92, -90.43) * mm});
            skLineSegment(sketch, "E310.MirrorCS", {"start": v(309.92, -157.33) * mm, "end": v(309.92, -158.1) * mm});
            skLineSegment(sketch, "E311.MirrorCS", {"start": v(312.46, -106.59) * mm, "end": v(312.46, -107.35) * mm});
            skLineSegment(sketch, "E312.MirrorCS", {"start": v(312.46, -84.03) * mm, "end": v(312.46, -84.8) * mm});
            skLineSegment(sketch, "E313.MirrorCS", {"start": v(309.92, -106.59) * mm, "end": v(309.92, -107.35) * mm});
            skLineSegment(sketch, "E314.MirrorCS", {"start": v(309.92, -84.03) * mm, "end": v(309.92, -84.8) * mm});
            skLineSegment(sketch, "E315.MirrorCS", {"start": v(286.11, -92.53) * mm, "end": v(286.11, -93.2) * mm});
            skLineSegment(sketch, "E316.MirrorCS", {"start": v(309.92, -123.5) * mm, "end": v(309.92, -124.26) * mm});
            skLineSegment(sketch, "E317.MirrorCS", {"start": v(286.11, -81.26) * mm, "end": v(286.11, -81.93) * mm});
            skLineSegment(sketch, "E318.MirrorCS", {"start": v(312.46, -89.67) * mm, "end": v(312.46, -90.43) * mm});
            skLineSegment(sketch, "E319.MirrorCS", {"start": v(312.46, -157.33) * mm, "end": v(312.46, -158.1) * mm});
            skLineSegment(sketch, "E320.MirrorCS", {"start": v(312.46, -123.5) * mm, "end": v(312.46, -124.26) * mm});
            skLineSegment(sketch, "E321.MirrorCS", {"start": v(335, -160.92) * mm, "end": v(335, -160.15) * mm});
            skLineSegment(sketch, "E322.MirrorCS", {"start": v(286.11, -126.37) * mm, "end": v(286.11, -127.04) * mm});
            skLineSegment(sketch, "E323.MirrorCS", {"start": v(286.11, -103.81) * mm, "end": v(286.11, -104.48) * mm});
            skLineSegment(sketch, "E324.MirrorCS", {"start": v(286.11, -148.92) * mm, "end": v(286.11, -149.6) * mm});
            skLineSegment(sketch, "E325.MirrorCS", {"start": v(309.92, -78.4) * mm, "end": v(309.92, -79.15) * mm});
            skLineSegment(sketch, "E326.MirrorCS", {"start": v(335, -98.89) * mm, "end": v(335, -98.13) * mm});
            skLineSegment(sketch, "E327.MirrorCS", {"start": v(312.46, -129.14) * mm, "end": v(312.46, -129.9) * mm});
            skLineSegment(sketch, "E328.MirrorCS", {"start": v(312.46, -151.7) * mm, "end": v(312.46, -152.46) * mm});
            skLineSegment(sketch, "E329.MirrorCS", {"start": v(309.92, -129.14) * mm, "end": v(309.92, -129.9) * mm});
            skLineSegment(sketch, "E330.MirrorCS", {"start": v(286.11, -120.73) * mm, "end": v(286.11, -121.4) * mm});
            skLineSegment(sketch, "E331.MirrorCS", {"start": v(309.92, -151.7) * mm, "end": v(309.92, -152.46) * mm});
            skLineSegment(sketch, "E332.MirrorCS", {"start": v(286.11, -143.28) * mm, "end": v(286.11, -143.96) * mm});
            skLineSegment(sketch, "E333.MirrorCS", {"start": v(312.46, -78.4) * mm, "end": v(312.46, -79.15) * mm});
            skLineSegment(sketch, "E334.MirrorCS", {"start": v(286.11, -98.17) * mm, "end": v(286.11, -98.85) * mm});
            skLineSegment(sketch, "E335.MirrorCS", {"start": v(309.92, -100.95) * mm, "end": v(309.92, -101.7) * mm});
            skLineSegment(sketch, "E336.MirrorCS", {"start": v(286.11, -137.64) * mm, "end": v(286.11, -138.32) * mm});
            skLineSegment(sketch, "E337.MirrorCS", {"start": v(286.11, -115.09) * mm, "end": v(286.11, -115.76) * mm});
            skLineSegment(sketch, "E338.MirrorCS", {"start": v(335, -81.97) * mm, "end": v(335, -81.21) * mm});
            skLineSegment(sketch, "E339.MirrorCS", {"start": v(337.55, -77.52) * mm, "end": v(337.55, -83.15) * mm, "construction": true});
            skLineSegment(sketch, "E340.MirrorCS", {"start": v(312.46, -140.42) * mm, "end": v(312.46, -141.18) * mm});
            skLineSegment(sketch, "E341.MirrorCS", {"start": v(312.46, -117.86) * mm, "end": v(312.46, -118.62) * mm});
            skLineSegment(sketch, "E342.MirrorCS", {"start": v(335, -132.72) * mm, "end": v(335, -131.96) * mm});
            skLineSegment(sketch, "E343.MirrorCS", {"start": v(312.46, -95.3) * mm, "end": v(312.46, -96.07) * mm});
            skLineSegment(sketch, "E344.MirrorCS", {"start": v(335, -87.61) * mm, "end": v(335, -86.85) * mm});
            skLineSegment(sketch, "E345.MirrorCS", {"start": v(286.11, -86.9) * mm, "end": v(286.11, -87.57) * mm});
            skLineSegment(sketch, "E346.MirrorCS", {"start": v(309.92, -117.86) * mm, "end": v(309.92, -118.62) * mm});
            skLineSegment(sketch, "E347.MirrorCS", {"start": v(286.11, -109.45) * mm, "end": v(286.11, -110.12) * mm});
            skLineSegment(sketch, "E348.MirrorCS", {"start": v(309.92, -140.42) * mm, "end": v(309.92, -141.18) * mm});
            skLineSegment(sketch, "E349.MirrorCS", {"start": v(286.11, -132) * mm, "end": v(286.11, -132.68) * mm});
            skLineSegment(sketch, "E350.MirrorCS", {"start": v(335, -93.25) * mm, "end": v(335, -92.49) * mm});
            skLineSegment(sketch, "E351.MirrorCS", {"start": v(312.46, -100.95) * mm, "end": v(312.46, -101.7) * mm});
            skLineSegment(sketch, "E352.MirrorCS", {"start": v(335, -138.36) * mm, "end": v(335, -137.6) * mm});
            skLineSegment(sketch, "E353.MirrorCS", {"start": v(312.46, -112.22) * mm, "end": v(312.46, -112.99) * mm});
            skLineSegment(sketch, "E354.MirrorCS", {"start": v(335, -104.53) * mm, "end": v(335, -103.77) * mm});
            skLineSegment(sketch, "E355.MirrorCS", {"start": v(335, -149.64) * mm, "end": v(335, -148.88) * mm});
            skLineSegment(sketch, "E356.MirrorCS", {"start": v(309.92, -78.4) * mm, "end": v(312.46, -78.4) * mm, "construction": true});
            skLineSegment(sketch, "E357.MirrorCS", {"start": v(335, -115.8) * mm, "end": v(335, -115.04) * mm});
            skLineSegment(sketch, "E358.MirrorCS", {"start": v(309.92, -112.22) * mm, "end": v(309.92, -112.99) * mm});
            skLineSegment(sketch, "E359.MirrorCS", {"start": v(309.92, -134.78) * mm, "end": v(309.92, -135.54) * mm});
            skLineSegment(sketch, "E360.MirrorCS", {"start": v(335, -121.44) * mm, "end": v(335, -120.68) * mm});
            skLineSegment(sketch, "E361.MirrorCS", {"start": v(335, -144) * mm, "end": v(335, -143.24) * mm});
            skLineSegment(sketch, "E362.MirrorCS", {"start": v(328.66, -76.56) * mm, "end": v(286.11, -76.56) * mm});
            skLineSegment(sketch, "E363.MirrorCS", {"start": v(286.11, -160.2) * mm, "end": v(286.11, -160.87) * mm});
            skLineSegment(sketch, "E364.MirrorCS", {"start": v(309.92, -146.06) * mm, "end": v(309.92, -146.82) * mm});
            skLineSegment(sketch, "E365.MirrorCS", {"start": v(335, -110.17) * mm, "end": v(335, -109.4) * mm});
            skLineSegment(sketch, "E366.MirrorCS", {"start": v(335, -155.28) * mm, "end": v(335, -154.52) * mm});
            skLineSegment(sketch, "E367.MirrorCS", {"start": v(286.11, -154.56) * mm, "end": v(286.11, -155.23) * mm});
            skLineSegment(sketch, "E368.MirrorCS", {"start": v(335, -127.08) * mm, "end": v(335, -126.32) * mm});
            skLineSegment(sketch, "E369.MirrorCS", {"start": v(312.46, -134.78) * mm, "end": v(312.46, -135.54) * mm});
            skLineSegment(sketch, "E370.MirrorCS", {"start": v(312.46, -146.06) * mm, "end": v(312.46, -146.82) * mm});
            skLineSegment(sketch, "E371.MirrorCS", {"start": v(337.55, -77.52) * mm, "end": v(312.46, -78.4) * mm});
            skLineSegment(sketch, "E372.MirrorCS", {"start": v(307.38, -77.3) * mm, "end": v(286.11, -76.56) * mm});
            skLineSegment(sketch, "E373.MirrorCS", {"start": v(328.66, -76.56) * mm, "end": v(307.38, -77.3) * mm});
            skLineSegment(sketch, "E374.MirrorCS", {"start": v(284.84, -91.3) * mm, "end": v(309.92, -90.43) * mm});
            skLineSegment(sketch, "E375.MirrorCS", {"start": v(312.46, -84.8) * mm, "end": v(337.55, -85.67) * mm});
            skLineSegment(sketch, "E376.MirrorCS", {"start": v(312.46, -152.46) * mm, "end": v(337.55, -153.33) * mm});
            skLineSegment(sketch, "E377.MirrorCS", {"start": v(286.11, -143.96) * mm, "end": v(311.2, -144.83) * mm});
            skLineSegment(sketch, "E378.MirrorCS", {"start": v(337.55, -77.52) * mm, "end": v(284.84, -77.52) * mm, "construction": true});
            skLineSegment(sketch, "E379.MirrorCS", {"start": v(335, -160.15) * mm, "end": v(311.2, -159.32) * mm});
            skLineSegment(sketch, "E380.MirrorCS", {"start": v(337.55, -83.15) * mm, "end": v(312.46, -84.03) * mm});
            skLineSegment(sketch, "E381.MirrorCS", {"start": v(335, -81.21) * mm, "end": v(311.2, -80.38) * mm});
            skLineSegment(sketch, "E382.MirrorCS", {"start": v(309.92, -89.67) * mm, "end": v(284.84, -88.8) * mm});
            skLineSegment(sketch, "E383.MirrorCS", {"start": v(335, -86.85) * mm, "end": v(311.2, -86.02) * mm});
            skLineSegment(sketch, "E384.MirrorCS", {"start": v(311.2, -82.8) * mm, "end": v(335, -81.97) * mm});
            skLineSegment(sketch, "E385.MirrorCS", {"start": v(284.84, -85.67) * mm, "end": v(309.92, -84.8) * mm});
            skLineSegment(sketch, "E386.MirrorCS", {"start": v(311.2, -88.44) * mm, "end": v(335, -87.61) * mm});
            skLineSegment(sketch, "E387.MirrorCS", {"start": v(337.55, -77.52) * mm, "end": v(312.15, -77.52) * mm, "construction": true});
            skLineSegment(sketch, "E388.MirrorCS", {"start": v(286.11, -87.57) * mm, "end": v(311.2, -88.44) * mm});
            skLineSegment(sketch, "E389.MirrorCS", {"start": v(312.46, -79.15) * mm, "end": v(337.55, -80.03) * mm});
            skLineSegment(sketch, "E390.MirrorCS", {"start": v(309.92, -78.4) * mm, "end": v(284.84, -77.52) * mm});
            skLineSegment(sketch, "E391.MirrorCS", {"start": v(337.55, -88.8) * mm, "end": v(312.46, -89.67) * mm});
            skLineSegment(sketch, "E392.MirrorCS", {"start": v(311.2, -86.02) * mm, "end": v(286.11, -86.9) * mm});
            skLineSegment(sketch, "E393.MirrorCS", {"start": v(337.55, -100.07) * mm, "end": v(312.46, -100.95) * mm});
            skLineSegment(sketch, "E394.MirrorCS", {"start": v(311.2, -80.38) * mm, "end": v(286.11, -81.26) * mm});
            skLineSegment(sketch, "E395.MirrorCS", {"start": v(309.92, -84.03) * mm, "end": v(284.84, -83.15) * mm});
            skLineSegment(sketch, "E396.MirrorCS", {"start": v(335, -98.13) * mm, "end": v(311.2, -97.3) * mm});
            skLineSegment(sketch, "E397.MirrorCS", {"start": v(335, -120.68) * mm, "end": v(311.2, -119.85) * mm});
            skLineSegment(sketch, "E398.MirrorCS", {"start": v(335, -143.24) * mm, "end": v(311.2, -142.4) * mm});
            skPoint(sketch, "E399.MirrorP", {"position": v(286.11, -81.6) * mm});
            skPoint(sketch, "E400.MirrorP", {"position": v(309.29, -88.5) * mm});
            skPoint(sketch, "E401.MirrorP", {"position": v(287.38, -93.35) * mm});
            skPoint(sketch, "E402.MirrorP", {"position": v(309.92, -78.77) * mm});
            skLineSegment(sketch, "E403.MirrorCS", {"start": v(286.11, -98.85) * mm, "end": v(311.2, -99.72) * mm});
            skLineSegment(sketch, "E404.MirrorCS", {"start": v(312.46, -107.35) * mm, "end": v(337.55, -108.22) * mm});
            skLineSegment(sketch, "E405.MirrorCS", {"start": v(284.84, -136.42) * mm, "end": v(309.92, -135.54) * mm});
            skLineSegment(sketch, "E406.MirrorCS", {"start": v(312.46, -129.9) * mm, "end": v(337.55, -130.78) * mm});
            skLineSegment(sketch, "E407.MirrorCS", {"start": v(284.84, -113.86) * mm, "end": v(309.92, -112.99) * mm});
            skLineSegment(sketch, "E408.MirrorCS", {"start": v(286.11, -121.4) * mm, "end": v(311.2, -122.28) * mm});
            skLineSegment(sketch, "E409.MirrorCS", {"start": v(284.84, -158.97) * mm, "end": v(309.92, -158.1) * mm});
            skLineSegment(sketch, "E410.MirrorCS", {"start": v(311.2, -136.77) * mm, "end": v(286.11, -137.64) * mm});
            skLineSegment(sketch, "E411.MirrorCS", {"start": v(311.2, -114.21) * mm, "end": v(286.11, -115.09) * mm});
            skLineSegment(sketch, "E412.MirrorCS", {"start": v(311.2, -159.32) * mm, "end": v(286.11, -160.2) * mm});
            skLineSegment(sketch, "E413.MirrorCS", {"start": v(311.2, -91.66) * mm, "end": v(286.11, -92.53) * mm});
            skLineSegment(sketch, "E414.MirrorCS", {"start": v(335, -137.6) * mm, "end": v(311.2, -136.77) * mm});
            skLineSegment(sketch, "E415.MirrorCS", {"start": v(335, -115.04) * mm, "end": v(311.2, -114.21) * mm});
            skLineSegment(sketch, "E416.MirrorCS", {"start": v(286.11, -160.87) * mm, "end": v(311.2, -161.75) * mm});
            skLineSegment(sketch, "E417.MirrorCS", {"start": v(335, -92.49) * mm, "end": v(311.2, -91.66) * mm});
            skLineSegment(sketch, "E418.MirrorCS", {"start": v(311.2, -99.72) * mm, "end": v(335, -98.89) * mm});
            skLineSegment(sketch, "E419.MirrorCS", {"start": v(286.11, -93.2) * mm, "end": v(311.2, -94.08) * mm});
            skLineSegment(sketch, "E420.MirrorCS", {"start": v(335, -109.4) * mm, "end": v(311.2, -108.57) * mm});
            skLineSegment(sketch, "E421.MirrorCS", {"start": v(335, -131.96) * mm, "end": v(311.2, -131.13) * mm});
            skLineSegment(sketch, "E422.MirrorCS", {"start": v(335, -154.52) * mm, "end": v(311.2, -153.68) * mm});
            skLineSegment(sketch, "E423.MirrorCS", {"start": v(337.55, -94.43) * mm, "end": v(312.46, -95.3) * mm});
            skLineSegment(sketch, "E424.MirrorCS", {"start": v(337.55, -128.26) * mm, "end": v(312.46, -129.14) * mm});
            skLineSegment(sketch, "E425.MirrorCS", {"start": v(311.2, -111) * mm, "end": v(335, -110.17) * mm});
            skLineSegment(sketch, "E426.MirrorCS", {"start": v(337.55, -139.54) * mm, "end": v(312.46, -140.42) * mm});
            skLineSegment(sketch, "E427.MirrorCS", {"start": v(311.2, -122.28) * mm, "end": v(335, -121.44) * mm});
            skLineSegment(sketch, "E428.MirrorCS", {"start": v(309.92, -100.95) * mm, "end": v(284.84, -100.07) * mm});
            skLineSegment(sketch, "E429.MirrorCS", {"start": v(337.55, -116.99) * mm, "end": v(312.46, -117.86) * mm});
            skLineSegment(sketch, "E430.MirrorCS", {"start": v(309.92, -112.22) * mm, "end": v(284.84, -111.35) * mm});
            skLineSegment(sketch, "E431.MirrorCS", {"start": v(311.2, -133.55) * mm, "end": v(335, -132.72) * mm});
            skLineSegment(sketch, "E432.MirrorCS", {"start": v(309.92, -123.5) * mm, "end": v(284.84, -122.63) * mm});
            skLineSegment(sketch, "E433.MirrorCS", {"start": v(311.2, -156.1) * mm, "end": v(335, -155.28) * mm});
            skLineSegment(sketch, "E434.MirrorCS", {"start": v(309.92, -146.06) * mm, "end": v(284.84, -145.18) * mm});
            skLineSegment(sketch, "E435.MirrorCS", {"start": v(337.55, -105.7) * mm, "end": v(312.46, -106.59) * mm});
            skLineSegment(sketch, "E436.MirrorCS", {"start": v(337.55, -150.82) * mm, "end": v(312.46, -151.7) * mm});
            skLineSegment(sketch, "E437.MirrorCS", {"start": v(309.92, -157.33) * mm, "end": v(284.84, -156.46) * mm});
            skLineSegment(sketch, "E438.MirrorCS", {"start": v(311.2, -144.83) * mm, "end": v(335, -144) * mm});
            skLineSegment(sketch, "E439.MirrorCS", {"start": v(309.92, -134.78) * mm, "end": v(284.84, -133.9) * mm});
            skLineSegment(sketch, "E440.MirrorCS", {"start": v(286.11, -110.12) * mm, "end": v(311.2, -111) * mm});
            skLineSegment(sketch, "E441.MirrorCS", {"start": v(286.11, -132.68) * mm, "end": v(311.2, -133.55) * mm});
            skLineSegment(sketch, "E442.MirrorCS", {"start": v(284.84, -102.58) * mm, "end": v(309.92, -101.7) * mm});
            skLineSegment(sketch, "E443.MirrorCS", {"start": v(312.46, -141.18) * mm, "end": v(337.55, -142.06) * mm});
            skLineSegment(sketch, "E444.MirrorCS", {"start": v(312.46, -118.62) * mm, "end": v(337.55, -119.5) * mm});
            skLineSegment(sketch, "E445.MirrorCS", {"start": v(284.84, -125.14) * mm, "end": v(309.92, -124.26) * mm});
            skLineSegment(sketch, "E446.MirrorCS", {"start": v(284.84, -147.7) * mm, "end": v(309.92, -146.82) * mm});
            skLineSegment(sketch, "E447.MirrorCS", {"start": v(286.11, -155.23) * mm, "end": v(311.2, -156.1) * mm});
            skLineSegment(sketch, "E448.MirrorCS", {"start": v(312.46, -96.07) * mm, "end": v(337.55, -96.95) * mm});
            skPoint(sketch, "E449.MirrorP", {"position": v(328.64, -100.43) * mm});
            skLineSegment(sketch, "E450.MirrorCS", {"start": v(311.2, -125.5) * mm, "end": v(286.11, -126.37) * mm});
            skLineSegment(sketch, "E451.MirrorCS", {"start": v(311.2, -102.93) * mm, "end": v(286.11, -103.81) * mm});
            skLineSegment(sketch, "E452.MirrorCS", {"start": v(337.55, -162.6) * mm, "end": v(312.46, -163.48) * mm});
            skLineSegment(sketch, "E453.MirrorCS", {"start": v(311.2, -148.05) * mm, "end": v(286.11, -148.92) * mm});
            skLineSegment(sketch, "E454.MirrorCS", {"start": v(312.46, -101.7) * mm, "end": v(337.55, -102.58) * mm});
            skLineSegment(sketch, "E455.MirrorCS", {"start": v(284.84, -153.33) * mm, "end": v(309.92, -152.46) * mm});
            skLineSegment(sketch, "E456.MirrorCS", {"start": v(312.46, -124.26) * mm, "end": v(337.55, -125.14) * mm});
            skLineSegment(sketch, "E457.MirrorCS", {"start": v(312.46, -163.48) * mm, "end": v(337.55, -163.48) * mm});
            skLineSegment(sketch, "E458.MirrorCS", {"start": v(286.11, -138.32) * mm, "end": v(311.2, -139.2) * mm});
            skLineSegment(sketch, "E459.MirrorCS", {"start": v(335, -126.32) * mm, "end": v(311.2, -125.5) * mm});
            skLineSegment(sketch, "E460.MirrorCS", {"start": v(335, -103.77) * mm, "end": v(311.2, -102.93) * mm});
            skLineSegment(sketch, "E461.MirrorCS", {"start": v(335, -148.88) * mm, "end": v(311.2, -148.05) * mm});
            skLineSegment(sketch, "E462.MirrorCS", {"start": v(284.84, -130.78) * mm, "end": v(309.92, -129.9) * mm});
            skLineSegment(sketch, "E463.MirrorCS", {"start": v(309.92, -95.3) * mm, "end": v(284.84, -94.43) * mm});
            skLineSegment(sketch, "E464.MirrorCS", {"start": v(309.92, -117.86) * mm, "end": v(284.84, -116.99) * mm});
            skLineSegment(sketch, "E465.MirrorCS", {"start": v(311.2, -127.92) * mm, "end": v(335, -127.08) * mm});
            skLineSegment(sketch, "E466.MirrorCS", {"start": v(337.55, -156.46) * mm, "end": v(312.46, -157.33) * mm});
            skLineSegment(sketch, "E467.MirrorCS", {"start": v(311.2, -105.36) * mm, "end": v(335, -104.53) * mm});
            skLineSegment(sketch, "E468.MirrorCS", {"start": v(337.55, -111.35) * mm, "end": v(312.46, -112.22) * mm});
            skLineSegment(sketch, "E469.MirrorCS", {"start": v(311.2, -150.47) * mm, "end": v(335, -149.64) * mm});
            skLineSegment(sketch, "E470.MirrorCS", {"start": v(309.92, -140.42) * mm, "end": v(284.84, -139.54) * mm});
            skLineSegment(sketch, "E471.MirrorCS", {"start": v(312.46, -146.82) * mm, "end": v(337.55, -147.7) * mm});
            skLineSegment(sketch, "E472.MirrorCS", {"start": v(337.55, -133.9) * mm, "end": v(312.46, -134.78) * mm});
            skLineSegment(sketch, "E473.MirrorCS", {"start": v(284.84, -162.6) * mm, "end": v(309.92, -163.48) * mm});
            skPoint(sketch, "E474.MirrorP", {"position": v(309.29, -100.43) * mm});
            skLineSegment(sketch, "E475.MirrorCS", {"start": v(286.11, -115.76) * mm, "end": v(311.2, -116.64) * mm});
            skPoint(sketch, "E476.MirrorP", {"position": v(328.64, -88.5) * mm});
            skPoint(sketch, "E477.MirrorP", {"position": v(328.64, -76.56) * mm});
            skLineSegment(sketch, "E478.MirrorCS", {"start": v(284.84, -80.03) * mm, "end": v(309.92, -79.15) * mm});
            skLineSegment(sketch, "E479.MirrorCS", {"start": v(286.11, -81.93) * mm, "end": v(311.2, -82.8) * mm});
            skLineSegment(sketch, "E480.MirrorCS", {"start": v(284.84, -96.95) * mm, "end": v(309.92, -96.07) * mm});
            skLineSegment(sketch, "E481.MirrorCS", {"start": v(286.11, -127.04) * mm, "end": v(311.2, -127.92) * mm});
            skLineSegment(sketch, "E482.MirrorCS", {"start": v(312.46, -90.43) * mm, "end": v(337.55, -91.3) * mm});
            skLineSegment(sketch, "E483.MirrorCS", {"start": v(284.84, -119.5) * mm, "end": v(309.92, -118.62) * mm});
            skLineSegment(sketch, "E484.MirrorCS", {"start": v(286.11, -104.48) * mm, "end": v(311.2, -105.36) * mm});
            skLineSegment(sketch, "E485.MirrorCS", {"start": v(312.46, -112.99) * mm, "end": v(337.55, -113.86) * mm});
            skLineSegment(sketch, "E486.MirrorCS", {"start": v(312.46, -158.1) * mm, "end": v(337.55, -158.97) * mm});
            skLineSegment(sketch, "E487.MirrorCS", {"start": v(284.84, -142.06) * mm, "end": v(309.92, -141.18) * mm});
            skLineSegment(sketch, "E488.MirrorCS", {"start": v(286.11, -149.6) * mm, "end": v(311.2, -150.47) * mm});
            skLineSegment(sketch, "E489.MirrorCS", {"start": v(309.92, -163.48) * mm, "end": v(284.84, -163.48) * mm});
            skLineSegment(sketch, "E490.MirrorCS", {"start": v(312.46, -135.54) * mm, "end": v(337.55, -136.42) * mm});
            skLineSegment(sketch, "E491.MirrorCS", {"start": v(311.2, -108.57) * mm, "end": v(286.11, -109.45) * mm});
            skLineSegment(sketch, "E492.MirrorCS", {"start": v(311.2, -97.3) * mm, "end": v(286.11, -98.17) * mm});
            skLineSegment(sketch, "E493.MirrorCS", {"start": v(311.2, -119.85) * mm, "end": v(286.11, -120.73) * mm});
            skLineSegment(sketch, "E494.MirrorCS", {"start": v(311.2, -142.4) * mm, "end": v(286.11, -143.28) * mm});
            skLineSegment(sketch, "E495.MirrorCS", {"start": v(284.84, -108.22) * mm, "end": v(309.92, -107.35) * mm});
            skLineSegment(sketch, "E496.MirrorCS", {"start": v(337.55, -145.18) * mm, "end": v(312.46, -146.06) * mm});
            skLineSegment(sketch, "E497.MirrorCS", {"start": v(309.92, -151.7) * mm, "end": v(284.84, -150.82) * mm});
            skLineSegment(sketch, "E498.MirrorCS", {"start": v(311.2, -161.75) * mm, "end": v(335, -160.92) * mm});
            skLineSegment(sketch, "E499.MirrorCS", {"start": v(311.2, -116.64) * mm, "end": v(335, -115.8) * mm});
            skLineSegment(sketch, "E500.MirrorCS", {"start": v(337.55, -122.63) * mm, "end": v(312.46, -123.5) * mm});
            skLineSegment(sketch, "E501.MirrorCS", {"start": v(309.92, -129.14) * mm, "end": v(284.84, -128.26) * mm});
            skLineSegment(sketch, "E502.MirrorCS", {"start": v(311.2, -139.2) * mm, "end": v(335, -138.36) * mm});
            skLineSegment(sketch, "E503.MirrorCS", {"start": v(309.92, -106.59) * mm, "end": v(284.84, -105.7) * mm});
            skLineSegment(sketch, "E504.MirrorCS", {"start": v(328.66, -76.56) * mm, "end": v(289.94, -76.56) * mm, "construction": true});
            skLineSegment(sketch, "E505.MirrorCS", {"start": v(311.2, -131.13) * mm, "end": v(286.11, -132) * mm});
            skLineSegment(sketch, "E506.MirrorCS", {"start": v(311.2, -153.68) * mm, "end": v(286.11, -154.56) * mm});
            skLineSegment(sketch, "E507", {"start": v(309.92, -95.3) * mm, "end": v(309.92, -96.07) * mm});
            skLineSegment(sketch, "E508", {"start": v(311.2, -94.08) * mm, "end": v(335, -93.25) * mm});
            const initialGuessF0  = {"E234": [0.9554837378845216, -0.09083065924899618, 1, 0, 0.029171900000000004, 0.03175, 3.170687300529468, 6.283185307179586], "E242.MirrorCS": [1.0313487332064482, -0.09083065924899618, -1, 0, 0.029171900000000004, 0.03175, 6.283185307179586, 3.112498006650118]};
            skSetInitialGuess(sketch, initialGuessF0);
            skSolve(sketch);
        }
        {
            var Q0;
            Q0=makeQuery(id+"F0.imprint","IMPRINT",FACE,{"disambiguationData":[TD([[makeQuery(id+"F0.imprint","IMPRINT",EDGE,{"derivedFrom":sQuery(id+"F0.wireOp",EDGE,"E181")}),1.0]])]});
            var Q1;
            Q1=makeQuery(id+"F0.imprint","IMPRINT",FACE,{"disambiguationData":[TD([[makeQuery(id+"F0.imprint","IMPRINT",EDGE,{"derivedFrom":sQuery(id+"F0.wireOp",EDGE,"E191")}),1.0]])]});
            var Q2;
            Q2=makeQuery(id+"F0.imprint","IMPRINT",FACE,{"disambiguationData":[TD([[makeQuery(id+"F0.imprint","IMPRINT",EDGE,{"derivedFrom":sQuery(id+"F0.wireOp",EDGE,"E228")}),-1.0]])]});
            var Q3;
            Q3=makeQuery(id+"F0.imprint","IMPRINT",FACE,{"disambiguationData":[TD([[makeQuery(id+"F0.imprint","IMPRINT",EDGE,{"derivedFrom":sQuery(id+"F0.wireOp",EDGE,"E253")}),-1.0]])]});
            var Q4;
            Q4=makeQuery(id+"F0.imprint","IMPRINT",FACE,{"disambiguationData":[TD([[makeQuery(id+"F0.imprint","IMPRINT",EDGE,{"derivedFrom":sQuery(id+"F0.wireOp",EDGE,"E0.bottom")}),-1.0]])]});
            var Q5;
            Q5=makeQuery(id+"F0.imprint","IMPRINT",FACE,{"disambiguationData":[TD([[makeQuery(id+"F0.imprint","IMPRINT",EDGE,{"derivedFrom":sQuery(id+"F0.wireOp",EDGE,"E4.top")}),1.0]])]});
            var Q6;
            Q6=makeQuery(id+"F0.imprint","IMPRINT",FACE,{"disambiguationData":[TD([[makeQuery(id+"F0.imprint","IMPRINT",EDGE,{"derivedFrom":sQuery(id+"F0.wireOp",EDGE,"E128.bottom")}),-1.0]])]});
            var Q7;
            {var subQ4=sQuery(id+"F0.wireOp",EDGE,"E3.0");Q7=makeQuery(id+"F0.imprint","IMPRINT",FACE,{"disambiguationData":[TD([[makeQuery(id+"F0.imprint","IMPRINT",EDGE,{"derivedFrom":subQ4}),1.0]])]});}
            var Q8;
            Q8=makeQuery(id+"F0.imprint","IMPRINT",FACE,{"disambiguationData":[TD([[makeQuery(id+"F0.imprint","IMPRINT",EDGE,{"derivedFrom":sQuery(id+"F0.wireOp",EDGE,"E132")}),1.0]])]});
            var Q9;
            {var subQ0=sQuery(id+"F0.wireOp",EDGE,"E4.bottom");Q9=makeQuery(id+"F0.imprint","IMPRINT",FACE,{"disambiguationData":[TD([[makeQuery(id+"F0.imprint","IMPRINT",EDGE,{"derivedFrom":subQ0}),-1.0]])]});}
            var Q10;
            Q10=sQuery(id+"F0.wireOp",EDGE,"E0.left");
            var Q11;
            Q11=sQuery(id+"F0.wireOp",EDGE,"E1");
            var Q12;
            Q12=sQuery(id+"F0.wireOp",EDGE,"E66.trimOffspring");
            var Q13;
            Q13=sQuery(id+"F0.wireOp",EDGE,"E61.0.7.0");
            var Q14;
            Q14=sQuery(id+"F0.wireOp",EDGE,"E61.0.10.0");
            var Q15;
            Q15=sQuery(id+"F0.wireOp",EDGE,"E61.0.4.0");
            var Q16;
            Q16=sQuery(id+"F0.wireOp",EDGE,"E69.trimOffspring");
            var Q17;
            Q17=sQuery(id+"F0.wireOp",EDGE,"E62.trimOffspring");
            var Q18;
            Q18=sQuery(id+"F0.wireOp",EDGE,"E63.trimOffspring");
            var Q19;
            Q19=sQuery(id+"F0.wireOp",EDGE,"E61.0.3.0");
            var Q20;
            Q20=sQuery(id+"F0.wireOp",EDGE,"E17.trimOffspring");
            var Q21;
            Q21=sQuery(id+"F0.wireOp",EDGE,"E77.trimOffspring");
            var Q22;
            Q22=sQuery(id+"F0.wireOp",EDGE,"E20.trimOffspring");
            var Q23;
            Q23=sQuery(id+"F0.wireOp",EDGE,"E61.0.2.0");
            var Q24;
            Q24=sQuery(id+"F0.wireOp",EDGE,"E73.trimOffspring");
            var Q25;
            Q25=sQuery(id+"F0.wireOp",EDGE,"E78.trimOffspring");
            var Q26;
            Q26=sQuery(id+"F0.wireOp",EDGE,"E64.trimOffspring");
            var Q27;
            Q27=sQuery(id+"F0.wireOp",EDGE,"E61.0.5.0");
            var Q28;
            Q28=sQuery(id+"F0.wireOp",EDGE,"E61.0.8.0");
            var Q29;
            Q29=sQuery(id+"F0.wireOp",EDGE,"E67.trimOffspring");
            var Q30;
            Q30=sQuery(id+"F0.wireOp",EDGE,"E68.trimOffspring");
            var Q31;
            Q31=sQuery(id+"F0.wireOp",EDGE,"E16.trimOffspring");
            var Q32;
            Q32=sQuery(id+"F0.wireOp",EDGE,"E61.0.9.0");
            var Q33;
            Q33=sQuery(id+"F0.wireOp",EDGE,"E61.0.11.0");
            var Q34;
            Q34=sQuery(id+"F0.wireOp",EDGE,"E0.bottom");
            var Q35;
            Q35=sQuery(id+"F0.wireOp",EDGE,"E18.trimOffspring");
            var Q36;
            Q36=sQuery(id+"F0.wireOp",EDGE,"E70.trimOffspring");
            var Q37;
            Q37=sQuery(id+"F0.wireOp",EDGE,"E61.0.13.0");
            var Q38;
            Q38=sQuery(id+"F0.wireOp",EDGE,"E65.trimOffspring");
            var Q39;
            Q39=sQuery(id+"F0.wireOp",EDGE,"E61.0.6.0");
            var Q40;
            Q40=sQuery(id+"F0.wireOp",EDGE,"E61.0.17.0");
            var Q41;
            Q41=sQuery(id+"F0.wireOp",EDGE,"E61.0.1.0");
            var Q42;
            Q42=sQuery(id+"F0.wireOp",EDGE,"E19.trimOffspring");
            var Q43;
            Q43=sQuery(id+"F0.wireOp",EDGE,"E76.trimOffspring");
            var Q44;
            Q44=sQuery(id+"F0.wireOp",EDGE,"E61.0.14.0");
            var Q45;
            Q45=sQuery(id+"F0.wireOp",EDGE,"E75.trimOffspring");
            var Q46;
            Q46=sQuery(id+"F0.wireOp",EDGE,"E61.0.16.0");
            var Q47;
            Q47=sQuery(id+"F0.wireOp",EDGE,"E71.trimOffspring");
            var Q48;
            Q48=sQuery(id+"F0.wireOp",EDGE,"E61.0.12.0");
            var Q49;
            Q49=sQuery(id+"F0.wireOp",EDGE,"E74.trimOffspring");
            var Q50;
            Q50=sQuery(id+"F0.wireOp",EDGE,"E72.trimOffspring");
            var Q51;
            Q51=sQuery(id+"F0.wireOp",EDGE,"E61.0.15.0");
            var Q52;
            Q52=sQuery(id+"F0.wireOp",EDGE,"E2.0");
            var Q53;
            Q53=sQuery(id+"F0.wireOp",EDGE,"E2.1");
            var Q54;
            Q54=sQuery(id+"F0.wireOp",EDGE,"E11");
            var Q55;
            Q55=sQuery(id+"F0.wireOp",EDGE,"E12");
            var Q56;
            Q56=sQuery(id+"F0.wireOp",EDGE,"E14");
            var Q57;
            Q57=sQuery(id+"F0.wireOp",EDGE,"E10");
            var Q58;
            Q58=sQuery(id+"F0.wireOp",EDGE,"E15");
            var Q59;
            Q59=sQuery(id+"F0.wireOp",EDGE,"E13");
            var Q60;
            Q60=sQuery(id+"F0.wireOp",EDGE,"E60");
            var Q61;
            Q61=sQuery(id+"F0.wireOp",EDGE,"E0.right");
            extrude(context, id + "F1", {"entities" : qUnion([Q0, Q1, Q2, Q3, Q4, Q5, Q6, Q7, Q8, Q9]), "bodyType" : ToolBodyType.SURFACE, "surfaceEntities" : qUnion([Q10, Q11, Q12, Q13, Q14, Q15, Q16, Q17, Q18, Q19, Q20, Q21, Q22, Q23, Q24, Q25, Q26, Q27, Q28, Q29, Q30, Q31, Q32, Q33, Q34, Q35, Q36, Q37, Q38, Q39, Q40, Q41, Q42, Q43, Q44, Q45, Q46, Q47, Q48, Q49, Q50, Q51, Q52, Q53, Q54, Q55, Q56, Q57, Q58, Q59, Q60, Q61]), "depth" : 25.4 * mm});
        }
        {
            var Q0;
            Q0=sQuery(id+"F0.wireOp",EDGE,"E3.0");
            var Q1;
            Q1=sQuery(id+"F0.wireOp",EDGE,"E21");
            extrude(context, id + "F2", {"bodyType" : ToolBodyType.SURFACE, "surfaceEntities" : qUnion([Q0, Q1]), "depth" : 25.4 * mm});
        }
        {
            var Q0;
            {var subQ0=sQuery(id+"F0.wireOp",EDGE,"E4.bottom");Q0=makeQuery(id+"F0.imprint","IMPRINT",FACE,{"disambiguationData":[TD([[makeQuery(id+"F0.imprint","IMPRINT",EDGE,{"derivedFrom":subQ0}),-1.0]])]});}
            var Q1;
            Q1=makeQuery(id+"F0.imprint","IMPRINT",FACE,{"disambiguationData":[TD([[makeQuery(id+"F0.imprint","IMPRINT",EDGE,{"derivedFrom":sQuery(id+"F0.wireOp",EDGE,"E4.top")}),1.0]])]});
            var Q2;
            Q2=sQuery(id+"F0.wireOp",EDGE,"E30.trimOffspring");
            var Q3;
            Q3=sQuery(id+"F0.wireOp",EDGE,"E45.MirrorCS");
            var Q4;
            Q4=sQuery(id+"F0.wireOp",EDGE,"E26");
            var Q5;
            Q5=sQuery(id+"F0.wireOp",EDGE,"E24");
            var Q6;
            Q6=sQuery(id+"F0.wireOp",EDGE,"E47.MirrorCS");
            var Q7;
            Q7=sQuery(id+"F0.wireOp",EDGE,"E44.MirrorCS");
            var Q8;
            Q8=sQuery(id+"F0.wireOp",EDGE,"E29.trimOffspring");
            var Q9;
            Q9=sQuery(id+"F0.wireOp",EDGE,"E25");
            var Q10;
            Q10=sQuery(id+"F0.wireOp",EDGE,"E37.trimOffspring");
            var Q11;
            Q11=sQuery(id+"F0.wireOp",EDGE,"E31.trimOffspring");
            var Q12;
            Q12=sQuery(id+"F0.wireOp",EDGE,"E51.MirrorCS");
            var Q13;
            Q13=sQuery(id+"F0.wireOp",EDGE,"E46.MirrorCS");
            var Q14;
            Q14=sQuery(id+"F0.wireOp",EDGE,"E28.trimOffspring");
            var Q15;
            Q15=sQuery(id+"F0.wireOp",EDGE,"E4.left");
            var Q16;
            Q16=sQuery(id+"F0.wireOp",EDGE,"E4.top");
            var Q17;
            Q17=sQuery(id+"F0.wireOp",EDGE,"E4.bottom");
            var Q18;
            Q18=sQuery(id+"F0.wireOp",EDGE,"E5.3");
            var Q19;
            Q19=sQuery(id+"F0.wireOp",EDGE,"E23");
            var Q20;
            Q20=sQuery(id+"F0.wireOp",EDGE,"E22");
            var Q21;
            Q21=sQuery(id+"F0.wireOp",EDGE,"E41.MirrorCS");
            var Q22;
            Q22=sQuery(id+"F0.wireOp",EDGE,"E59.MirrorCS");
            var Q23;
            Q23=sQuery(id+"F0.wireOp",EDGE,"E58.MirrorCS");
            var Q24;
            Q24=sQuery(id+"F0.wireOp",EDGE,"E36.trimOffspring");
            var Q25;
            Q25=sQuery(id+"F0.wireOp",EDGE,"E56.MirrorCS");
            var Q26;
            Q26=sQuery(id+"F0.wireOp",EDGE,"E35");
            var Q27;
            Q27=sQuery(id+"F0.wireOp",EDGE,"E54.MirrorCS");
            var Q28;
            Q28=sQuery(id+"F0.wireOp",EDGE,"E34");
            var Q29;
            Q29=sQuery(id+"F0.wireOp",EDGE,"E53.MirrorCS");
            var Q30;
            Q30=sQuery(id+"F0.wireOp",EDGE,"E33");
            var Q31;
            Q31=sQuery(id+"F0.wireOp",EDGE,"E52.MirrorCS");
            var Q32;
            Q32=sQuery(id+"F0.wireOp",EDGE,"E57.MirrorCS");
            var Q33;
            Q33=sQuery(id+"F0.wireOp",EDGE,"E48.MirrorCS");
            var Q34;
            Q34=sQuery(id+"F0.wireOp",EDGE,"E43.MirrorCS");
            var Q35;
            Q35=sQuery(id+"F0.wireOp",EDGE,"E49.MirrorCS");
            var Q36;
            Q36=sQuery(id+"F0.wireOp",EDGE,"E42.MirrorCS");
            var Q37;
            Q37=sQuery(id+"F0.wireOp",EDGE,"E40.MirrorCS");
            extrude(context, id + "F3", {"entities" : qUnion([Q0, Q1]), "bodyType" : ToolBodyType.SURFACE, "surfaceEntities" : qUnion([Q2, Q3, Q4, Q5, Q6, Q7, Q8, Q9, Q10, Q11, Q12, Q13, Q14, Q15, Q16, Q17, Q18, Q19, Q20, Q21, Q22, Q23, Q24, Q25, Q26, Q27, Q28, Q29, Q30, Q31, Q32, Q33, Q34, Q35, Q36, Q37]), "depth" : 25.4 * mm});
        }
        {
            var Q0;
            Q0=sQuery(id+"F0.wireOp",EDGE,"E7");
            extrude(context, id + "F4", {"bodyType" : ToolBodyType.SURFACE, "surfaceEntities" : qUnion([Q0]), "depth" : 25.4 * mm});
        }
        {
            var Q0;
            Q0=sQuery(id+"F0.wireOp",EDGE,"E5.0");
            extrude(context, id + "F5", {"bodyType" : ToolBodyType.SURFACE, "surfaceEntities" : qUnion([Q0]), "depth" : 25.4 * mm});
        }
        {
            var Q0;
            Q0=sQuery(id+"F0.wireOp",EDGE,"E93.MirrorCS");
            var Q1;
            Q1=sQuery(id+"F0.wireOp",EDGE,"E83.0.8.3");
            var Q2;
            Q2=sQuery(id+"F0.wireOp",EDGE,"E83.0.8.1");
            var Q3;
            Q3=sQuery(id+"F0.wireOp",EDGE,"E107.MirrorCS");
            var Q4;
            Q4=sQuery(id+"F0.wireOp",EDGE,"E83.0.3.3");
            var Q5;
            Q5=sQuery(id+"F0.wireOp",EDGE,"E81");
            var Q6;
            Q6=sQuery(id+"F0.wireOp",EDGE,"E83.0.4.3");
            var Q7;
            Q7=sQuery(id+"F0.wireOp",EDGE,"E83.0.5.0");
            var Q8;
            Q8=sQuery(id+"F0.wireOp",EDGE,"E83.0.4.2");
            var Q9;
            Q9=sQuery(id+"F0.wireOp",EDGE,"E83.0.7.3");
            var Q10;
            Q10=sQuery(id+"F0.wireOp",EDGE,"E90.MirrorCS");
            var Q11;
            Q11=sQuery(id+"F0.wireOp",EDGE,"E96.MirrorCS");
            var Q12;
            Q12=sQuery(id+"F0.wireOp",EDGE,"E83.0.8.2");
            var Q13;
            Q13=sQuery(id+"F0.wireOp",EDGE,"E102.MirrorCS");
            var Q14;
            Q14=sQuery(id+"F0.wireOp",EDGE,"E109.MirrorCS");
            var Q15;
            Q15=sQuery(id+"F0.wireOp",EDGE,"E126.MirrorCS");
            var Q16;
            Q16=sQuery(id+"F0.wireOp",EDGE,"E83.0.6.3");
            var Q17;
            Q17=sQuery(id+"F0.wireOp",EDGE,"E114.MirrorCS");
            var Q18;
            Q18=sQuery(id+"F0.wireOp",EDGE,"E108.MirrorCS");
            var Q19;
            Q19=sQuery(id+"F0.wireOp",EDGE,"E83.0.4.1");
            var Q20;
            Q20=sQuery(id+"F0.wireOp",EDGE,"E125.MirrorCS");
            var Q21;
            Q21=sQuery(id+"F0.wireOp",EDGE,"E113.MirrorCS");
            var Q22;
            Q22=sQuery(id+"F0.wireOp",EDGE,"E83.0.2.3");
            var Q23;
            Q23=sQuery(id+"F0.wireOp",EDGE,"E83.0.1.0");
            var Q24;
            Q24=sQuery(id+"F0.wireOp",EDGE,"E92.MirrorCS");
            var Q25;
            Q25=sQuery(id+"F0.wireOp",EDGE,"E83.0.3.2");
            var Q26;
            Q26=sQuery(id+"F0.wireOp",EDGE,"E121.MirrorCS");
            var Q27;
            Q27=sQuery(id+"F0.wireOp",EDGE,"E105.MirrorCS");
            var Q28;
            Q28=sQuery(id+"F0.wireOp",EDGE,"E104.MirrorCS");
            var Q29;
            Q29=sQuery(id+"F0.wireOp",EDGE,"E83.0.3.1");
            var Q30;
            Q30=sQuery(id+"F0.wireOp",EDGE,"E83.0.7.1");
            var Q31;
            Q31=sQuery(id+"F0.wireOp",EDGE,"E127.MirrorCS");
            var Q32;
            Q32=sQuery(id+"F0.wireOp",EDGE,"E82");
            var Q33;
            Q33=sQuery(id+"F0.wireOp",EDGE,"E83.0.8.0");
            var Q34;
            Q34=sQuery(id+"F0.wireOp",EDGE,"E91.MirrorCS");
            var Q35;
            Q35=sQuery(id+"F0.wireOp",EDGE,"E83.0.4.0");
            var Q36;
            Q36=sQuery(id+"F0.wireOp",EDGE,"E79");
            var Q37;
            Q37=sQuery(id+"F0.wireOp",EDGE,"E123.MirrorCS");
            var Q38;
            Q38=sQuery(id+"F0.wireOp",EDGE,"E111.MirrorCS");
            var Q39;
            Q39=sQuery(id+"F0.wireOp",EDGE,"E95.MirrorCS");
            var Q40;
            Q40=sQuery(id+"F0.wireOp",EDGE,"E83.0.5.1");
            var Q41;
            Q41=sQuery(id+"F0.wireOp",EDGE,"E83.0.1.1");
            var Q42;
            Q42=sQuery(id+"F0.wireOp",EDGE,"E112.MirrorCS");
            var Q43;
            Q43=sQuery(id+"F0.wireOp",EDGE,"E83.0.5.2");
            var Q44;
            Q44=sQuery(id+"F0.wireOp",EDGE,"E83.0.1.2");
            var Q45;
            Q45=sQuery(id+"F0.wireOp",EDGE,"E84.0.1.0");
            var Q46;
            Q46=sQuery(id+"F0.wireOp",EDGE,"E97.MirrorCS");
            var Q47;
            Q47=sQuery(id+"F0.wireOp",EDGE,"E83.0.5.3");
            var Q48;
            Q48=sQuery(id+"F0.wireOp",EDGE,"E83.0.1.3");
            var Q49;
            Q49=sQuery(id+"F0.wireOp",EDGE,"E98.MirrorCS");
            var Q50;
            Q50=sQuery(id+"F0.wireOp",EDGE,"E84.0.1.1");
            var Q51;
            Q51=sQuery(id+"F0.wireOp",EDGE,"E85.MirrorCS");
            var Q52;
            Q52=sQuery(id+"F0.wireOp",EDGE,"E83.0.6.2");
            var Q53;
            Q53=sQuery(id+"F0.wireOp",EDGE,"E83.0.2.2");
            var Q54;
            Q54=sQuery(id+"F0.wireOp",EDGE,"E117.MirrorCS");
            var Q55;
            Q55=sQuery(id+"F0.wireOp",EDGE,"E101.MirrorCS");
            var Q56;
            Q56=sQuery(id+"F0.wireOp",EDGE,"E86.MirrorCS");
            var Q57;
            Q57=sQuery(id+"F0.wireOp",EDGE,"E118.MirrorCS");
            var Q58;
            Q58=sQuery(id+"F0.wireOp",EDGE,"E87.MirrorCS");
            var Q59;
            Q59=sQuery(id+"F0.wireOp",EDGE,"E83.0.7.0");
            var Q60;
            Q60=sQuery(id+"F0.wireOp",EDGE,"E83.0.3.0");
            var Q61;
            Q61=sQuery(id+"F0.wireOp",EDGE,"E119.MirrorCS");
            var Q62;
            Q62=sQuery(id+"F0.wireOp",EDGE,"E103.MirrorCS");
            var Q63;
            Q63=sQuery(id+"F0.wireOp",EDGE,"E88.MirrorCS");
            var Q64;
            Q64=sQuery(id+"F0.wireOp",EDGE,"E120.MirrorCS");
            var Q65;
            Q65=sQuery(id+"F0.wireOp",EDGE,"E8");
            var Q66;
            Q66=sQuery(id+"F0.wireOp",EDGE,"E89.MirrorCS");
            var Q67;
            Q67=sQuery(id+"F0.wireOp",EDGE,"E83.0.7.2");
            var Q68;
            Q68=sQuery(id+"F0.wireOp",EDGE,"E83.0.6.0");
            var Q69;
            Q69=sQuery(id+"F0.wireOp",EDGE,"E83.0.2.0");
            var Q70;
            Q70=sQuery(id+"F0.wireOp",EDGE,"E115.MirrorCS");
            var Q71;
            Q71=sQuery(id+"F0.wireOp",EDGE,"E83.0.6.1");
            var Q72;
            Q72=sQuery(id+"F0.wireOp",EDGE,"E83.0.2.1");
            var Q73;
            Q73=sQuery(id+"F0.wireOp",EDGE,"E116.MirrorCS");
            var Q74;
            Q74=sQuery(id+"F0.wireOp",EDGE,"E100.MirrorCS");
            var Q75;
            Q75=sQuery(id+"F0.wireOp",EDGE,"E122.MirrorCS");
            extrude(context, id + "F6", {"bodyType" : ToolBodyType.SURFACE, "surfaceEntities" : qUnion([Q0, Q1, Q2, Q3, Q4, Q5, Q6, Q7, Q8, Q9, Q10, Q11, Q12, Q13, Q14, Q15, Q16, Q17, Q18, Q19, Q20, Q21, Q22, Q23, Q24, Q25, Q26, Q27, Q28, Q29, Q30, Q31, Q32, Q33, Q34, Q35, Q36, Q37, Q38, Q39, Q40, Q41, Q42, Q43, Q44, Q45, Q46, Q47, Q48, Q49, Q50, Q51, Q52, Q53, Q54, Q55, Q56, Q57, Q58, Q59, Q60, Q61, Q62, Q63, Q64, Q65, Q66, Q67, Q68, Q69, Q70, Q71, Q72, Q73, Q74, Q75]), "depth" : 25.4 * mm});
        }
        {
            var Q0;
            Q0=sQuery(id+"F0.wireOp",EDGE,"E6.left");
            var Q1;
            Q1=sQuery(id+"F0.wireOp",EDGE,"E6.right");
            extrude(context, id + "F7", {"bodyType" : ToolBodyType.SURFACE, "surfaceEntities" : qUnion([Q0, Q1]), "depth" : 25.4 * mm});
        }
        {
            var Q0;
            Q0=sQuery(id+"F0.wireOp",EDGE,"E182");
            var Q1;
            Q1=sQuery(id+"F0.wireOp",EDGE,"E181");
            var Q2;
            Q2=sQuery(id+"F0.wireOp",EDGE,"E187.MirrorCS");
            var Q3;
            Q3=sQuery(id+"F0.wireOp",EDGE,"E189.MirrorCS");
            var Q4;
            Q4=sQuery(id+"F0.wireOp",EDGE,"E190.MirrorCS");
            var Q5;
            Q5=sQuery(id+"F0.wireOp",EDGE,"E186");
            var Q6;
            Q6=sQuery(id+"F0.wireOp",EDGE,"E188.MirrorCS");
            var Q7;
            Q7=sQuery(id+"F0.wireOp",EDGE,"E185");
            var Q8;
            Q8=sQuery(id+"F0.wireOp",EDGE,"E267");
            extrude(context, id + "F8", {"bodyType" : ToolBodyType.SURFACE, "surfaceEntities" : qUnion([Q0, Q1, Q2, Q3, Q4, Q5, Q6, Q7, Q8]), "depth" : 25.4 * mm});
        }
        {
            var Q0;
            Q0=sQuery(id+"F0.wireOp",EDGE,"E210");
            var Q1;
            Q1=sQuery(id+"F0.wireOp",EDGE,"E208");
            var Q2;
            Q2=sQuery(id+"F0.wireOp",EDGE,"E221.MirrorCS");
            var Q3;
            Q3=sQuery(id+"F0.wireOp",EDGE,"E191");
            var Q4;
            Q4=sQuery(id+"F0.wireOp",EDGE,"E222.MirrorCS");
            var Q5;
            Q5=sQuery(id+"F0.wireOp",EDGE,"E226.MirrorCS");
            var Q6;
            Q6=sQuery(id+"F0.wireOp",EDGE,"E209");
            var Q7;
            Q7=sQuery(id+"F0.wireOp",EDGE,"E225.MirrorCS");
            var Q8;
            Q8=sQuery(id+"F0.wireOp",EDGE,"E223.MirrorCS");
            var Q9;
            Q9=sQuery(id+"F0.wireOp",EDGE,"E211");
            var Q10;
            Q10=sQuery(id+"F0.wireOp",EDGE,"E213");
            var Q11;
            Q11=sQuery(id+"F0.wireOp",EDGE,"E216");
            var Q12;
            Q12=sQuery(id+"F0.wireOp",EDGE,"E215");
            var Q13;
            Q13=sQuery(id+"F0.wireOp",EDGE,"E220.MirrorCS");
            var Q14;
            Q14=sQuery(id+"F0.wireOp",EDGE,"E219.MirrorCS");
            var Q15;
            Q15=sQuery(id+"F0.wireOp",EDGE,"E218.MirrorCS");
            var Q16;
            Q16=sQuery(id+"F0.wireOp",EDGE,"E217.MirrorCS");
            var Q17;
            Q17=sQuery(id+"F0.wireOp",EDGE,"E212");
            extrude(context, id + "F9", {"bodyType" : ToolBodyType.SURFACE, "surfaceEntities" : qUnion([Q0, Q1, Q2, Q3, Q4, Q5, Q6, Q7, Q8, Q9, Q10, Q11, Q12, Q13, Q14, Q15, Q16, Q17]), "depth" : 25.4 * mm});
        }
        {
            var Q0;
            Q0=sQuery(id+"F0.wireOp",EDGE,"E229");
            var Q1;
            Q1=sQuery(id+"F0.wireOp",EDGE,"E239.MirrorCS");
            var Q2;
            Q2=sQuery(id+"F0.wireOp",EDGE,"E238");
            var Q3;
            Q3=sQuery(id+"F0.wireOp",EDGE,"E236");
            var Q4;
            Q4=sQuery(id+"F0.wireOp",EDGE,"E228");
            var Q5;
            Q5=sQuery(id+"F0.wireOp",EDGE,"E235");
            var Q6;
            Q6=sQuery(id+"F0.wireOp",EDGE,"E245.MirrorCS");
            var Q7;
            Q7=sQuery(id+"F0.wireOp",EDGE,"E242.MirrorCS");
            var Q8;
            Q8=sQuery(id+"F0.wireOp",EDGE,"E244.MirrorCS");
            var Q9;
            Q9=sQuery(id+"F0.wireOp",EDGE,"E234");
            var Q10;
            Q10=sQuery(id+"F0.wireOp",EDGE,"E231");
            var Q11;
            Q11=sQuery(id+"F0.wireOp",EDGE,"E240.MirrorCS");
            var Q12;
            Q12=sQuery(id+"F0.wireOp",EDGE,"E241.MirrorCS");
            var Q13;
            Q13=sQuery(id+"F0.wireOp",EDGE,"E232");
            var Q14;
            Q14=sQuery(id+"F0.wireOp",EDGE,"E243.MirrorCS");
            var Q15;
            Q15=sQuery(id+"F0.wireOp",EDGE,"E251.MirrorCS");
            var Q16;
            Q16=sQuery(id+"F0.wireOp",EDGE,"E237.filletArc");
            extrude(context, id + "F10", {"bodyType" : ToolBodyType.SURFACE, "surfaceEntities" : qUnion([Q0, Q1, Q2, Q3, Q4, Q5, Q6, Q7, Q8, Q9, Q10, Q11, Q12, Q13, Q14, Q15, Q16]), "depth" : 25.4 * mm});
        }
        {
            var Q0;
            Q0=makeQuery(id+"F0.imprint","IMPRINT",FACE,{"disambiguationData":[TD([[makeQuery(id+"F0.imprint","IMPRINT",EDGE,{"derivedFrom":sQuery(id+"F0.wireOp",EDGE,"E253")}),-1.0]])]});
            var Q1;
            Q1=sQuery(id+"F0.wireOp",EDGE,"E255.MirrorCS");
            var Q2;
            Q2=sQuery(id+"F0.wireOp",EDGE,"E256.MirrorCS");
            var Q3;
            Q3=sQuery(id+"F0.wireOp",EDGE,"E257.MirrorCS");
            var Q4;
            Q4=sQuery(id+"F0.wireOp",EDGE,"E253");
            extrude(context, id + "F11", {"entities" : qUnion([Q0]), "bodyType" : ToolBodyType.SURFACE, "surfaceEntities" : qUnion([Q1, Q2, Q3, Q4]), "depth" : 25.4 * mm});
        }
        {
            var Q0;
            Q0=sQuery(id+"F0.wireOp",EDGE,"E180.1");
            var Q1;
            Q1=sQuery(id+"F0.wireOp",EDGE,"E180.0");
            var Q2;
            Q2=sQuery(id+"F0.wireOp",EDGE,"E132");
            var Q3;
            Q3=sQuery(id+"F0.wireOp",EDGE,"E134");
            var Q4;
            Q4=sQuery(id+"F0.wireOp",EDGE,"E180.2");
            var Q5;
            Q5=sQuery(id+"F0.wireOp",EDGE,"E133");
            var Q6;
            Q6=sQuery(id+"F0.wireOp",EDGE,"fc53a9f3-5fa7-448e-a30a-fa5267a044a0");
            var Q7;
            Q7=sQuery(id+"F0.wireOp",EDGE,"4fb24d02-ac4f-4f08-8406-d5561f622e68.MirrorCS");
            var Q8;
            Q8=sQuery(id+"F0.wireOp",EDGE,"3254d6ae-d2f0-4b72-ba5d-33e5e97f0522.0.6.2");
            var Q9;
            Q9=sQuery(id+"F0.wireOp",EDGE,"3254d6ae-d2f0-4b72-ba5d-33e5e97f0522.0.4.3");
            var Q10;
            Q10=sQuery(id+"F0.wireOp",EDGE,"ec919566-703f-44a7-b3ad-99448f98d498.MirrorCS");
            var Q11;
            Q11=sQuery(id+"F0.wireOp",EDGE,"8d1420b8-e9ac-44bf-9581-763be117281d.MirrorCS");
            var Q12;
            Q12=sQuery(id+"F0.wireOp",EDGE,"3254d6ae-d2f0-4b72-ba5d-33e5e97f0522.0.2.2");
            var Q13;
            Q13=sQuery(id+"F0.wireOp",EDGE,"3254d6ae-d2f0-4b72-ba5d-33e5e97f0522.0.1.3");
            var Q14;
            Q14=sQuery(id+"F0.wireOp",EDGE,"3254d6ae-d2f0-4b72-ba5d-33e5e97f0522.0.4.2");
            var Q15;
            Q15=sQuery(id+"F0.wireOp",EDGE,"3254d6ae-d2f0-4b72-ba5d-33e5e97f0522.0.5.1");
            var Q16;
            Q16=sQuery(id+"F0.wireOp",EDGE,"3254d6ae-d2f0-4b72-ba5d-33e5e97f0522.0.4.0");
            var Q17;
            Q17=sQuery(id+"F0.wireOp",EDGE,"572cea9d-ebc9-4609-ada1-aaea7138f4d6.MirrorCS");
            var Q18;
            Q18=sQuery(id+"F0.wireOp",EDGE,"e9395519-7992-4df9-b4e1-71a6f29e8405.MirrorCS");
            var Q19;
            Q19=sQuery(id+"F0.wireOp",EDGE,"3254d6ae-d2f0-4b72-ba5d-33e5e97f0522.0.5.2");
            var Q20;
            Q20=sQuery(id+"F0.wireOp",EDGE,"65e45e9f-0995-4d26-829c-86e4993f6eb5.MirrorCS");
            var Q21;
            Q21=sQuery(id+"F0.wireOp",EDGE,"3254d6ae-d2f0-4b72-ba5d-33e5e97f0522.0.3.1");
            var Q22;
            Q22=sQuery(id+"F0.wireOp",EDGE,"2e7d90cb-8bac-4d67-9015-8ff395367a8b.MirrorCS");
            var Q23;
            Q23=sQuery(id+"F0.wireOp",EDGE,"0b6ebfb0-3530-455f-b61b-24027b82720b.MirrorCS");
            var Q24;
            Q24=sQuery(id+"F0.wireOp",EDGE,"6c401fb8-abea-4e19-b295-100b5f4fdfef.MirrorCS");
            var Q25;
            Q25=sQuery(id+"F0.wireOp",EDGE,"8b1f1520-3865-4302-96c6-3611b4a89b7e.0.1.1");
            var Q26;
            Q26=sQuery(id+"F0.wireOp",EDGE,"cf22ce5c-1562-4da7-a4c7-b21e6a170815.MirrorCS");
            var Q27;
            Q27=sQuery(id+"F0.wireOp",EDGE,"0d962791-e4bc-4981-84d0-5a9cbd59bd57.MirrorCS");
            var Q28;
            Q28=sQuery(id+"F0.wireOp",EDGE,"ad77e980-506d-4a86-81e9-3747b8620e92.MirrorCS");
            var Q29;
            Q29=sQuery(id+"F0.wireOp",EDGE,"3254d6ae-d2f0-4b72-ba5d-33e5e97f0522.0.8.2");
            var Q30;
            Q30=sQuery(id+"F0.wireOp",EDGE,"bb50b7a2-d199-4059-b79a-004283f32853.MirrorCS");
            var Q31;
            Q31=sQuery(id+"F0.wireOp",EDGE,"47e2b7df-931a-4b32-88b9-3dcbaf488a01.MirrorCS");
            var Q32;
            Q32=sQuery(id+"F0.wireOp",EDGE,"9085c06c-c75b-49cb-900b-1cac99c266af");
            var Q33;
            Q33=sQuery(id+"F0.wireOp",EDGE,"3254d6ae-d2f0-4b72-ba5d-33e5e97f0522.0.4.1");
            var Q34;
            Q34=sQuery(id+"F0.wireOp",EDGE,"9f6776e1-d5f1-47e2-96a2-7c229ce02e4a.MirrorCS");
            var Q35;
            Q35=sQuery(id+"F0.wireOp",EDGE,"cdfb3fe2-d8c4-4916-bef3-4fbe3eb32fb3.MirrorCS");
            var Q36;
            Q36=sQuery(id+"F0.wireOp",EDGE,"88d0b271-fd5b-44c8-9aa6-4b9dd50c574d.MirrorCS");
            var Q37;
            Q37=sQuery(id+"F0.wireOp",EDGE,"3254d6ae-d2f0-4b72-ba5d-33e5e97f0522.0.3.0");
            var Q38;
            Q38=sQuery(id+"F0.wireOp",EDGE,"c3463710-7ca2-4f02-b968-ba71700d5fc8.MirrorCS");
            var Q39;
            Q39=sQuery(id+"F0.wireOp",EDGE,"1fef89d9-2ba7-4ab0-877f-b2474d01b7ad.MirrorCS");
            var Q40;
            Q40=sQuery(id+"F0.wireOp",EDGE,"3254d6ae-d2f0-4b72-ba5d-33e5e97f0522.0.5.3");
            var Q41;
            Q41=sQuery(id+"F0.wireOp",EDGE,"4a9058d4-6f30-4fad-a5f5-ca3147a05b7d.MirrorCS");
            var Q42;
            Q42=sQuery(id+"F0.wireOp",EDGE,"3254d6ae-d2f0-4b72-ba5d-33e5e97f0522.0.7.2");
            var Q43;
            Q43=sQuery(id+"F0.wireOp",EDGE,"3254d6ae-d2f0-4b72-ba5d-33e5e97f0522.0.5.0");
            var Q44;
            Q44=sQuery(id+"F0.wireOp",EDGE,"513b9647-341d-4573-9d2a-c188213fadf9.MirrorCS");
            var Q45;
            Q45=sQuery(id+"F0.wireOp",EDGE,"1f2b9d94-d912-4183-a4f1-711f5dd33fc4.MirrorCS");
            var Q46;
            Q46=sQuery(id+"F0.wireOp",EDGE,"3254d6ae-d2f0-4b72-ba5d-33e5e97f0522.0.8.0");
            var Q47;
            Q47=sQuery(id+"F0.wireOp",EDGE,"3254d6ae-d2f0-4b72-ba5d-33e5e97f0522.0.8.3");
            var Q48;
            Q48=sQuery(id+"F0.wireOp",EDGE,"3254d6ae-d2f0-4b72-ba5d-33e5e97f0522.0.7.3");
            var Q49;
            Q49=sQuery(id+"F0.wireOp",EDGE,"3254d6ae-d2f0-4b72-ba5d-33e5e97f0522.0.3.3");
            var Q50;
            Q50=sQuery(id+"F0.wireOp",EDGE,"9ab1c175-7ecd-4a3a-8d18-fec9413b51c2.MirrorCS");
            var Q51;
            Q51=sQuery(id+"F0.wireOp",EDGE,"11a26f71-97fc-4ee9-a5af-cc3bdf452f60.MirrorCS");
            var Q52;
            Q52=sQuery(id+"F0.wireOp",EDGE,"20235c37-fdb4-4523-b8a3-3e53efb61d46.MirrorCS");
            var Q53;
            Q53=sQuery(id+"F0.wireOp",EDGE,"3f7bac8c-5681-4184-98bf-19059c982698.MirrorCS");
            var Q54;
            Q54=sQuery(id+"F0.wireOp",EDGE,"f3a988e3-31d6-4c45-97d4-2d99949105f5.MirrorCS");
            var Q55;
            Q55=sQuery(id+"F0.wireOp",EDGE,"3254d6ae-d2f0-4b72-ba5d-33e5e97f0522.0.3.2");
            var Q56;
            Q56=sQuery(id+"F0.wireOp",EDGE,"3254d6ae-d2f0-4b72-ba5d-33e5e97f0522.0.1.1");
            var Q57;
            Q57=sQuery(id+"F0.wireOp",EDGE,"3254d6ae-d2f0-4b72-ba5d-33e5e97f0522.0.7.1");
            var Q58;
            Q58=sQuery(id+"F0.wireOp",EDGE,"aae9c3d1-cfe6-4fb8-b82f-73b150c73998.MirrorCS");
            var Q59;
            Q59=sQuery(id+"F0.wireOp",EDGE,"307995c1-5f86-44ad-9839-6cce27f8c432.MirrorCS");
            var Q60;
            Q60=sQuery(id+"F0.wireOp",EDGE,"3254d6ae-d2f0-4b72-ba5d-33e5e97f0522.0.1.2");
            var Q61;
            Q61=sQuery(id+"F0.wireOp",EDGE,"be1136d5-7ebc-4b9e-bc7b-2050abe5db45.MirrorCS");
            var Q62;
            Q62=sQuery(id+"F0.wireOp",EDGE,"fc9e3234-9110-4186-b773-a366b7e27d76.MirrorCS");
            var Q63;
            Q63=sQuery(id+"F0.wireOp",EDGE,"3254d6ae-d2f0-4b72-ba5d-33e5e97f0522.0.1.0");
            var Q64;
            Q64=sQuery(id+"F0.wireOp",EDGE,"b8db8502-623b-4476-80fe-902f54c1294a.MirrorCS");
            var Q65;
            Q65=sQuery(id+"F0.wireOp",EDGE,"383a791b-9da2-44e3-b695-9919042acf29.MirrorCS");
            var Q66;
            Q66=sQuery(id+"F0.wireOp",EDGE,"3254d6ae-d2f0-4b72-ba5d-33e5e97f0522.0.6.1");
            var Q67;
            Q67=sQuery(id+"F0.wireOp",EDGE,"3254d6ae-d2f0-4b72-ba5d-33e5e97f0522.0.7.0");
            var Q68;
            Q68=sQuery(id+"F0.wireOp",EDGE,"3254d6ae-d2f0-4b72-ba5d-33e5e97f0522.0.2.1");
            var Q69;
            Q69=sQuery(id+"F0.wireOp",EDGE,"8b1f1520-3865-4302-96c6-3611b4a89b7e.0.1.0");
            var Q70;
            Q70=sQuery(id+"F0.wireOp",EDGE,"24e685c0-83a3-4415-9449-488847f29245.MirrorCS");
            var Q71;
            Q71=sQuery(id+"F0.wireOp",EDGE,"d5e235bd-ecae-4cd2-ab79-1bdfb5cd6f4f.MirrorCS");
            var Q72;
            Q72=sQuery(id+"F0.wireOp",EDGE,"918b1c0b-fbf3-434c-ace6-ca09c4062e45.MirrorCS");
            var Q73;
            Q73=sQuery(id+"F0.wireOp",EDGE,"3254d6ae-d2f0-4b72-ba5d-33e5e97f0522.0.8.1");
            var Q74;
            Q74=sQuery(id+"F0.wireOp",EDGE,"3254d6ae-d2f0-4b72-ba5d-33e5e97f0522.0.2.3");
            var Q75;
            Q75=sQuery(id+"F0.wireOp",EDGE,"362c904f-289d-497a-b4f2-b0830128a88b.MirrorCS");
            var Q76;
            Q76=sQuery(id+"F0.wireOp",EDGE,"3254d6ae-d2f0-4b72-ba5d-33e5e97f0522.0.6.3");
            var Q77;
            Q77=sQuery(id+"F0.wireOp",EDGE,"3917e9ac-7778-47fe-830d-2f8bf6be8240");
            var Q78;
            Q78=sQuery(id+"F0.wireOp",EDGE,"3254d6ae-d2f0-4b72-ba5d-33e5e97f0522.0.6.0");
            var Q79;
            Q79=sQuery(id+"F0.wireOp",EDGE,"3254d6ae-d2f0-4b72-ba5d-33e5e97f0522.0.2.0");
            var Q80;
            Q80=sQuery(id+"F0.wireOp",EDGE,"E179");
            var Q81;
            Q81=sQuery(id+"F0.wireOp",EDGE,"3cd0644f-c177-4327-8bd8-2bc085255346");
            var Q82;
            Q82=sQuery(id+"F0.wireOp",EDGE,"7d1e28d7-469a-43ea-bba7-8bab66ebc8f6.MirrorCS");
            var Q83;
            Q83=sQuery(id+"F0.wireOp",EDGE,"ssZe56ps-8knL-qMRk-LBrc-yhTDze4BGWGT");
            var Q84;
            Q84=sQuery(id+"F0.wireOp",EDGE,"w6JuM9Ky-uXfy-m1yp-JmWf-DL3Zjl29ogjD");
            var Q85;
            Q85=sQuery(id+"F0.wireOp",EDGE,"pU61Y423-OOam-kZ1X-ZPk0-gyHz3Y6RvGHW");
            extrude(context, id + "F12", {"bodyType" : ToolBodyType.SURFACE, "surfaceEntities" : qUnion([Q0, Q1, Q2, Q3, Q4, Q5, Q6, Q7, Q8, Q9, Q10, Q11, Q12, Q13, Q14, Q15, Q16, Q17, Q18, Q19, Q20, Q21, Q22, Q23, Q24, Q25, Q26, Q27, Q28, Q29, Q30, Q31, Q32, Q33, Q34, Q35, Q36, Q37, Q38, Q39, Q40, Q41, Q42, Q43, Q44, Q45, Q46, Q47, Q48, Q49, Q50, Q51, Q52, Q53, Q54, Q55, Q56, Q57, Q58, Q59, Q60, Q61, Q62, Q63, Q64, Q65, Q66, Q67, Q68, Q69, Q70, Q71, Q72, Q73, Q74, Q75, Q76, Q77, Q78, Q79, Q80, Q81, Q82, Q83, Q84, Q85]), "depth" : 25.4 * mm});
        }
        {
            var Q0;
            Q0=sQuery(id+"F0.wireOp",EDGE,"E129.left");
            var Q1;
            Q1=sQuery(id+"F0.wireOp",EDGE,"UjF9LhMT-lXVe-WLjf-KscX-ks1rPGe4wGXW");
            extrude(context, id + "F13", {"bodyType" : ToolBodyType.SURFACE, "surfaceEntities" : qUnion([Q0, Q1]), "depth" : 25.4 * mm});
        }
        {
            var Q0;
            Q0=sQuery(id+"F0.wireOp",EDGE,"E165.MirrorCS");
            var Q1;
            Q1=sQuery(id+"F0.wireOp",EDGE,"E151.0.2.1");
            var Q2;
            Q2=sQuery(id+"F0.wireOp",EDGE,"E271");
            var Q3;
            Q3=sQuery(id+"F0.wireOp",EDGE,"E176.MirrorCS");
            var Q4;
            Q4=sQuery(id+"F0.wireOp",EDGE,"E173.MirrorCS");
            var Q5;
            Q5=sQuery(id+"F0.wireOp",EDGE,"E151.0.7.4");
            var Q6;
            Q6=sQuery(id+"F0.wireOp",EDGE,"E147");
            var Q7;
            Q7=sQuery(id+"F0.wireOp",EDGE,"E164.MirrorCS");
            var Q8;
            Q8=sQuery(id+"F0.wireOp",EDGE,"E261");
            var Q9;
            Q9=sQuery(id+"F0.wireOp",EDGE,"E159.MirrorCS");
            var Q10;
            Q10=sQuery(id+"F0.wireOp",EDGE,"E177.MirrorCS");
            var Q11;
            Q11=sQuery(id+"F0.wireOp",EDGE,"E151.0.4.2");
            var Q12;
            Q12=sQuery(id+"F0.wireOp",EDGE,"E272");
            var Q13;
            Q13=sQuery(id+"F0.wireOp",EDGE,"E151.0.3.3");
            var Q14;
            Q14=sQuery(id+"F0.wireOp",EDGE,"E171.MirrorCS");
            var Q15;
            Q15=sQuery(id+"F0.wireOp",EDGE,"E270");
            var Q16;
            Q16=sQuery(id+"F0.wireOp",EDGE,"E141");
            var Q17;
            Q17=sQuery(id+"F0.wireOp",EDGE,"E152.MirrorCS");
            var Q18;
            Q18=sQuery(id+"F0.wireOp",EDGE,"E175.MirrorCS");
            var Q19;
            Q19=sQuery(id+"F0.wireOp",EDGE,"E157.MirrorCS");
            var Q20;
            Q20=sQuery(id+"F0.wireOp",EDGE,"E172.MirrorCS");
            var Q21;
            Q21=sQuery(id+"F0.wireOp",EDGE,"E146.trimOffspring");
            var Q22;
            Q22=sQuery(id+"F0.wireOp",EDGE,"E151.0.6.3");
            var Q23;
            Q23=sQuery(id+"F0.wireOp",EDGE,"E262");
            var Q24;
            Q24=sQuery(id+"F0.wireOp",EDGE,"E151.0.6.2");
            var Q25;
            Q25=sQuery(id+"F0.wireOp",EDGE,"E151.0.3.2");
            var Q26;
            Q26=sQuery(id+"F0.wireOp",EDGE,"E151.0.3.1");
            var Q27;
            Q27=sQuery(id+"F0.wireOp",EDGE,"E174.MirrorCS");
            var Q28;
            Q28=sQuery(id+"F0.wireOp",EDGE,"E151.0.1.3");
            var Q29;
            Q29=sQuery(id+"F0.wireOp",EDGE,"E148");
            var Q30;
            Q30=sQuery(id+"F0.wireOp",EDGE,"E151.0.1.1");
            var Q31;
            Q31=sQuery(id+"F0.wireOp",EDGE,"E151.0.8.3");
            var Q32;
            Q32=sQuery(id+"F0.wireOp",EDGE,"E151.0.5.1");
            var Q33;
            Q33=sQuery(id+"F0.wireOp",EDGE,"E140");
            var Q34;
            Q34=sQuery(id+"F0.wireOp",EDGE,"E151.0.4.1");
            var Q35;
            Q35=sQuery(id+"F0.wireOp",EDGE,"E139");
            var Q36;
            Q36=sQuery(id+"F0.wireOp",EDGE,"E178.MirrorCS");
            var Q37;
            Q37=sQuery(id+"F0.wireOp",EDGE,"E258");
            var Q38;
            Q38=sQuery(id+"F0.wireOp",EDGE,"E144.trimOffspring");
            var Q39;
            Q39=sQuery(id+"F0.wireOp",EDGE,"E170.MirrorCS");
            var Q40;
            Q40=sQuery(id+"F0.wireOp",EDGE,"E163.MirrorCS");
            var Q41;
            Q41=sQuery(id+"F0.wireOp",EDGE,"E158.MirrorCS");
            var Q42;
            Q42=sQuery(id+"F0.wireOp",EDGE,"E151.0.4.3");
            var Q43;
            Q43=sQuery(id+"F0.wireOp",EDGE,"E269");
            var Q44;
            Q44=sQuery(id+"F0.wireOp",EDGE,"E138");
            var Q45;
            Q45=sQuery(id+"F0.wireOp",EDGE,"E263");
            var Q46;
            Q46=sQuery(id+"F0.wireOp",EDGE,"E151.0.3.4");
            var Q47;
            Q47=sQuery(id+"F0.wireOp",EDGE,"E142.trimOffspring");
            var Q48;
            Q48=sQuery(id+"F0.wireOp",EDGE,"E151.0.6.1");
            var Q49;
            Q49=sQuery(id+"F0.wireOp",EDGE,"E151.0.2.2");
            var Q50;
            Q50=sQuery(id+"F0.wireOp",EDGE,"E156.MirrorCS");
            var Q51;
            Q51=sQuery(id+"F0.wireOp",EDGE,"E151.0.7.3");
            var Q52;
            Q52=sQuery(id+"F0.wireOp",EDGE,"E128.bottom");
            var Q53;
            Q53=sQuery(id+"F0.wireOp",EDGE,"E151.0.5.4");
            var Q54;
            Q54=sQuery(id+"F0.wireOp",EDGE,"E154.MirrorCS");
            var Q55;
            Q55=sQuery(id+"F0.wireOp",EDGE,"E161.MirrorCS");
            var Q56;
            Q56=sQuery(id+"F0.wireOp",EDGE,"E131.0");
            var Q57;
            Q57=sQuery(id+"F0.wireOp",EDGE,"E135");
            var Q58;
            Q58=sQuery(id+"F0.wireOp",EDGE,"E131.1");
            var Q59;
            Q59=sQuery(id+"F0.wireOp",EDGE,"E150.trimOffspring");
            var Q60;
            Q60=sQuery(id+"F0.wireOp",EDGE,"E265");
            var Q61;
            Q61=sQuery(id+"F0.wireOp",EDGE,"E153.MirrorCS");
            var Q62;
            Q62=sQuery(id+"F0.wireOp",EDGE,"E149");
            var Q63;
            Q63=sQuery(id+"F0.wireOp",EDGE,"E151.0.1.2");
            var Q64;
            Q64=sQuery(id+"F0.wireOp",EDGE,"E259");
            var Q65;
            Q65=sQuery(id+"F0.wireOp",EDGE,"E151.0.8.2");
            var Q66;
            Q66=sQuery(id+"F0.wireOp",EDGE,"E137");
            var Q67;
            Q67=sQuery(id+"F0.wireOp",EDGE,"E151.0.5.2");
            var Q68;
            Q68=sQuery(id+"F0.wireOp",EDGE,"E151.0.2.3");
            var Q69;
            Q69=sQuery(id+"F0.wireOp",EDGE,"E162.MirrorCS");
            var Q70;
            Q70=sQuery(id+"F0.wireOp",EDGE,"E136");
            var Q71;
            Q71=sQuery(id+"F0.wireOp",EDGE,"E273");
            var Q72;
            Q72=sQuery(id+"F0.wireOp",EDGE,"67ec816b-5f9f-461e-9043-27507b7db0ba0.MirrorCS");
            var Q73;
            Q73=sQuery(id+"F0.wireOp",EDGE,"E166.MirrorCS");
            var Q74;
            Q74=sQuery(id+"F0.wireOp",EDGE,"E151.0.7.1");
            var Q75;
            Q75=sQuery(id+"F0.wireOp",EDGE,"E266");
            var Q76;
            Q76=sQuery(id+"F0.wireOp",EDGE,"E143.trimOffspring");
            var Q77;
            Q77=sQuery(id+"F0.wireOp",EDGE,"E155.MirrorCS");
            var Q78;
            Q78=sQuery(id+"F0.wireOp",EDGE,"E151.0.1.4");
            var Q79;
            Q79=sQuery(id+"F0.wireOp",EDGE,"E151.0.4.4");
            var Q80;
            Q80=sQuery(id+"F0.wireOp",EDGE,"E168.MirrorCS");
            var Q81;
            Q81=sQuery(id+"F0.wireOp",EDGE,"E128.left");
            var Q82;
            Q82=sQuery(id+"F0.wireOp",EDGE,"E151.0.8.1");
            var Q83;
            Q83=sQuery(id+"F0.wireOp",EDGE,"E160.MirrorCS");
            var Q84;
            Q84=sQuery(id+"F0.wireOp",EDGE,"E145.trimOffspring");
            var Q85;
            Q85=sQuery(id+"F0.wireOp",EDGE,"E264");
            var Q86;
            Q86=sQuery(id+"F0.wireOp",EDGE,"E260");
            var Q87;
            Q87=sQuery(id+"F0.wireOp",EDGE,"E151.0.5.3");
            extrude(context, id + "F14", {"bodyType" : ToolBodyType.SURFACE, "surfaceEntities" : qUnion([Q0, Q1, Q2, Q3, Q4, Q5, Q6, Q7, Q8, Q9, Q10, Q11, Q12, Q13, Q14, Q15, Q16, Q17, Q18, Q19, Q20, Q21, Q22, Q23, Q24, Q25, Q26, Q27, Q28, Q29, Q30, Q31, Q32, Q33, Q34, Q35, Q36, Q37, Q38, Q39, Q40, Q41, Q42, Q43, Q44, Q45, Q46, Q47, Q48, Q49, Q50, Q51, Q52, Q53, Q54, Q55, Q56, Q57, Q58, Q59, Q60, Q61, Q62, Q63, Q64, Q65, Q66, Q67, Q68, Q69, Q70, Q71, Q72, Q73, Q74, Q75, Q76, Q77, Q78, Q79, Q80, Q81, Q82, Q83, Q84, Q85, Q86, Q87]), "depth" : 25.4 * mm});
        }
        {
            var Q0;
            Q0=sQuery(id+"F0.wireOp",EDGE,"E2790.MirrorCS");
            var Q1;
            Q1=sQuery(id+"F0.wireOp",EDGE,"83a6329f-aab3-466c-9b30-dc960f796cd538.MirrorCS");
            var Q2;
            Q2=sQuery(id+"F0.wireOp",EDGE,"83a6329f-aab3-466c-9b30-dc960f796cd573.MirrorCS");
            var Q3;
            Q3=sQuery(id+"F0.wireOp",EDGE,"576c9210-4d5f-4eda-a998-4eb618526b88.0.22.1");
            var Q4;
            Q4=sQuery(id+"F0.wireOp",EDGE,"576c9210-4d5f-4eda-a998-4eb618526b88.0.12.2");
            var Q5;
            Q5=sQuery(id+"F0.wireOp",EDGE,"83a6329f-aab3-466c-9b30-dc960f796cd544.MirrorCS");
            var Q6;
            Q6=sQuery(id+"F0.wireOp",EDGE,"83a6329f-aab3-466c-9b30-dc960f796cd553.MirrorCS");
            var Q7;
            Q7=sQuery(id+"F0.wireOp",EDGE,"83a6329f-aab3-466c-9b30-dc960f796cd537.MirrorCS");
            var Q8;
            Q8=sQuery(id+"F0.wireOp",EDGE,"83a6329f-aab3-466c-9b30-dc960f796cd521.MirrorCS");
            var Q9;
            Q9=sQuery(id+"F0.wireOp",EDGE,"576c9210-4d5f-4eda-a998-4eb618526b88.0.13.1");
            var Q10;
            Q10=sQuery(id+"F0.wireOp",EDGE,"576c9210-4d5f-4eda-a998-4eb618526b88.0.4.2");
            var Q11;
            Q11=sQuery(id+"F0.wireOp",EDGE,"83a6329f-aab3-466c-9b30-dc960f796cd565.MirrorCS");
            var Q12;
            Q12=sQuery(id+"F0.wireOp",EDGE,"83a6329f-aab3-466c-9b30-dc960f796cd548.MirrorCS");
            var Q13;
            Q13=sQuery(id+"F0.wireOp",EDGE,"576c9210-4d5f-4eda-a998-4eb618526b88.0.15.1");
            var Q14;
            Q14=sQuery(id+"F0.wireOp",EDGE,"83a6329f-aab3-466c-9b30-dc960f796cd527.MirrorCS");
            var Q15;
            Q15=sQuery(id+"F0.wireOp",EDGE,"83a6329f-aab3-466c-9b30-dc960f796cd572.MirrorCS");
            var Q16;
            Q16=sQuery(id+"F0.wireOp",EDGE,"576c9210-4d5f-4eda-a998-4eb618526b88.0.1.1");
            var Q17;
            Q17=sQuery(id+"F0.wireOp",EDGE,"576c9210-4d5f-4eda-a998-4eb618526b88.0.16.2");
            var Q18;
            Q18=sQuery(id+"F0.wireOp",EDGE,"576c9210-4d5f-4eda-a998-4eb618526b88.0.3.1");
            var Q19;
            Q19=sQuery(id+"F0.wireOp",EDGE,"83a6329f-aab3-466c-9b30-dc960f796cd576.MirrorCS");
            var Q20;
            Q20=sQuery(id+"F0.wireOp",EDGE,"576c9210-4d5f-4eda-a998-4eb618526b88.0.1.2");
            var Q21;
            Q21=sQuery(id+"F0.wireOp",EDGE,"83a6329f-aab3-466c-9b30-dc960f796cd555.MirrorCS");
            var Q22;
            Q22=sQuery(id+"F0.wireOp",EDGE,"576c9210-4d5f-4eda-a998-4eb618526b88.0.17.1");
            var Q23;
            Q23=sQuery(id+"F0.wireOp",EDGE,"E2792.MirrorCS");
            var Q24;
            Q24=sQuery(id+"F0.wireOp",EDGE,"576c9210-4d5f-4eda-a998-4eb618526b88.0.7.0");
            var Q25;
            Q25=sQuery(id+"F0.wireOp",EDGE,"E2798.MirrorCS");
            var Q26;
            Q26=sQuery(id+"F0.wireOp",EDGE,"83a6329f-aab3-466c-9b30-dc960f796cd550.MirrorCS");
            var Q27;
            Q27=sQuery(id+"F0.wireOp",EDGE,"576c9210-4d5f-4eda-a998-4eb618526b88.0.5.2");
            var Q28;
            Q28=sQuery(id+"F0.wireOp",EDGE,"576c9210-4d5f-4eda-a998-4eb618526b88.0.21.2");
            var Q29;
            Q29=sQuery(id+"F0.wireOp",EDGE,"83a6329f-aab3-466c-9b30-dc960f796cd56.MirrorCS");
            var Q30;
            Q30=sQuery(id+"F0.wireOp",EDGE,"576c9210-4d5f-4eda-a998-4eb618526b88.0.16.0");
            var Q31;
            Q31=sQuery(id+"F0.wireOp",EDGE,"83a6329f-aab3-466c-9b30-dc960f796cd532.MirrorCS");
            var Q32;
            Q32=sQuery(id+"F0.wireOp",EDGE,"576c9210-4d5f-4eda-a998-4eb618526b88.0.7.1");
            var Q33;
            Q33=sQuery(id+"F0.wireOp",EDGE,"576c9210-4d5f-4eda-a998-4eb618526b88.0.19.0");
            var Q34;
            Q34=sQuery(id+"F0.wireOp",EDGE,"E2793.MirrorCS");
            var Q35;
            Q35=sQuery(id+"F0.wireOp",EDGE,"576c9210-4d5f-4eda-a998-4eb618526b88.0.21.0");
            var Q36;
            Q36=sQuery(id+"F0.wireOp",EDGE,"576c9210-4d5f-4eda-a998-4eb618526b88.0.1.0");
            var Q37;
            Q37=sQuery(id+"F0.wireOp",EDGE,"576c9210-4d5f-4eda-a998-4eb618526b88.0.20.0");
            var Q38;
            Q38=sQuery(id+"F0.wireOp",EDGE,"83a6329f-aab3-466c-9b30-dc960f796cd59.MirrorCS");
            var Q39;
            Q39=sQuery(id+"F0.wireOp",EDGE,"83a6329f-aab3-466c-9b30-dc960f796cd55.MirrorCS");
            var Q40;
            Q40=sQuery(id+"F0.wireOp",EDGE,"83a6329f-aab3-466c-9b30-dc960f796cd566.MirrorCS");
            var Q41;
            Q41=sQuery(id+"F0.wireOp",EDGE,"576c9210-4d5f-4eda-a998-4eb618526b88.0.9.1");
            var Q42;
            Q42=sQuery(id+"F0.wireOp",EDGE,"83a6329f-aab3-466c-9b30-dc960f796cd559.MirrorCS");
            var Q43;
            Q43=sQuery(id+"F0.wireOp",EDGE,"83a6329f-aab3-466c-9b30-dc960f796cd528.MirrorCS");
            var Q44;
            Q44=sQuery(id+"F0.wireOp",EDGE,"83a6329f-aab3-466c-9b30-dc960f796cd560.MirrorCS");
            var Q45;
            Q45=sQuery(id+"F0.wireOp",EDGE,"576c9210-4d5f-4eda-a998-4eb618526b88.0.23.1");
            var Q46;
            Q46=sQuery(id+"F0.wireOp",EDGE,"576c9210-4d5f-4eda-a998-4eb618526b88.0.2.1");
            var Q47;
            Q47=sQuery(id+"F0.wireOp",EDGE,"fTztT9gn-QBvG-o5l6-IoOj-KpO1ImnGZjxT");
            var Q48;
            Q48=sQuery(id+"F0.wireOp",EDGE,"83a6329f-aab3-466c-9b30-dc960f796cd557.MirrorCS");
            var Q49;
            Q49=sQuery(id+"F0.wireOp",EDGE,"576c9210-4d5f-4eda-a998-4eb618526b88.0.6.0");
            var Q50;
            Q50=sQuery(id+"F0.wireOp",EDGE,"83a6329f-aab3-466c-9b30-dc960f796cd540.MirrorCS");
            var Q51;
            Q51=sQuery(id+"F0.wireOp",EDGE,"576c9210-4d5f-4eda-a998-4eb618526b88.0.16.1");
            var Q52;
            Q52=sQuery(id+"F0.wireOp",EDGE,"576c9210-4d5f-4eda-a998-4eb618526b88.0.14.2");
            var Q53;
            Q53=sQuery(id+"F0.wireOp",EDGE,"576c9210-4d5f-4eda-a998-4eb618526b88.0.22.0");
            var Q54;
            Q54=sQuery(id+"F0.wireOp",EDGE,"83a6329f-aab3-466c-9b30-dc960f796cd575.MirrorCS");
            var Q55;
            Q55=sQuery(id+"F0.wireOp",EDGE,"83a6329f-aab3-466c-9b30-dc960f796cd542.MirrorCS");
            var Q56;
            Q56=sQuery(id+"F0.wireOp",EDGE,"576c9210-4d5f-4eda-a998-4eb618526b88.0.11.0");
            var Q57;
            Q57=sQuery(id+"F0.wireOp",EDGE,"576c9210-4d5f-4eda-a998-4eb618526b88.0.9.2");
            var Q58;
            Q58=sQuery(id+"F0.wireOp",EDGE,"576c9210-4d5f-4eda-a998-4eb618526b88.0.14.1");
            var Q59;
            Q59=sQuery(id+"F0.wireOp",EDGE,"83a6329f-aab3-466c-9b30-dc960f796cd567.MirrorCS");
            var Q60;
            Q60=sQuery(id+"F0.wireOp",EDGE,"576c9210-4d5f-4eda-a998-4eb618526b88.0.21.1");
            var Q61;
            Q61=sQuery(id+"F0.wireOp",EDGE,"83a6329f-aab3-466c-9b30-dc960f796cd543.MirrorCS");
            var Q62;
            Q62=sQuery(id+"F0.wireOp",EDGE,"576c9210-4d5f-4eda-a998-4eb618526b88.0.5.1");
            var Q63;
            Q63=sQuery(id+"F0.wireOp",EDGE,"83a6329f-aab3-466c-9b30-dc960f796cd531.MirrorCS");
            var Q64;
            Q64=sQuery(id+"F0.wireOp",EDGE,"E2795.MirrorCS");
            var Q65;
            Q65=sQuery(id+"F0.wireOp",EDGE,"E279.MirrorCS");
            var Q66;
            Q66=sQuery(id+"F0.wireOp",EDGE,"576c9210-4d5f-4eda-a998-4eb618526b88.0.23.0");
            var Q67;
            Q67=sQuery(id+"F0.wireOp",EDGE,"83a6329f-aab3-466c-9b30-dc960f796cd545.MirrorCS");
            var Q68;
            Q68=sQuery(id+"F0.wireOp",EDGE,"576c9210-4d5f-4eda-a998-4eb618526b88.0.19.2");
            var Q69;
            Q69=sQuery(id+"F0.wireOp",EDGE,"83a6329f-aab3-466c-9b30-dc960f796cd529.MirrorCS");
            var Q70;
            Q70=sQuery(id+"F0.wireOp",EDGE,"E179");
            var Q71;
            Q71=sQuery(id+"F0.wireOp",EDGE,"83a6329f-aab3-466c-9b30-dc960f796cd564.MirrorCS");
            var Q72;
            Q72=sQuery(id+"F0.wireOp",EDGE,"576c9210-4d5f-4eda-a998-4eb618526b88.0.15.2");
            var Q73;
            Q73=sQuery(id+"F0.wireOp",EDGE,"83a6329f-aab3-466c-9b30-dc960f796cd535.MirrorCS");
            var Q74;
            Q74=sQuery(id+"F0.wireOp",EDGE,"83a6329f-aab3-466c-9b30-dc960f796cd552.MirrorCS");
            var Q75;
            Q75=sQuery(id+"F0.wireOp",EDGE,"576c9210-4d5f-4eda-a998-4eb618526b88.0.2.2");
            var Q76;
            Q76=sQuery(id+"F0.wireOp",EDGE,"576c9210-4d5f-4eda-a998-4eb618526b88.0.5.0");
            var Q77;
            Q77=sQuery(id+"F0.wireOp",EDGE,"83a6329f-aab3-466c-9b30-dc960f796cd570.MirrorCS");
            var Q78;
            Q78=sQuery(id+"F0.wireOp",EDGE,"576c9210-4d5f-4eda-a998-4eb618526b88.0.7.2");
            var Q79;
            Q79=sQuery(id+"F0.wireOp",EDGE,"576c9210-4d5f-4eda-a998-4eb618526b88.0.2.0");
            var Q80;
            Q80=sQuery(id+"F0.wireOp",EDGE,"83a6329f-aab3-466c-9b30-dc960f796cd571.MirrorCS");
            var Q81;
            Q81=sQuery(id+"F0.wireOp",EDGE,"83a6329f-aab3-466c-9b30-dc960f796cd58.MirrorCS");
            var Q82;
            Q82=sQuery(id+"F0.wireOp",EDGE,"576c9210-4d5f-4eda-a998-4eb618526b88.0.11.1");
            var Q83;
            Q83=sQuery(id+"F0.wireOp",EDGE,"83a6329f-aab3-466c-9b30-dc960f796cd525.MirrorCS");
            var Q84;
            Q84=sQuery(id+"F0.wireOp",EDGE,"576c9210-4d5f-4eda-a998-4eb618526b88.0.10.0");
            var Q85;
            Q85=sQuery(id+"F0.wireOp",EDGE,"576c9210-4d5f-4eda-a998-4eb618526b88.0.20.1");
            var Q86;
            Q86=sQuery(id+"F0.wireOp",EDGE,"576c9210-4d5f-4eda-a998-4eb618526b88.0.18.2");
            var Q87;
            Q87=sQuery(id+"F0.wireOp",EDGE,"576c9210-4d5f-4eda-a998-4eb618526b88.0.4.0");
            var Q88;
            Q88=sQuery(id+"F0.wireOp",EDGE,"83a6329f-aab3-466c-9b30-dc960f796cd568.MirrorCS");
            var Q89;
            Q89=sQuery(id+"F0.wireOp",EDGE,"576c9210-4d5f-4eda-a998-4eb618526b88.0.17.2");
            var Q90;
            Q90=sQuery(id+"F0.wireOp",EDGE,"83a6329f-aab3-466c-9b30-dc960f796cd551.MirrorCS");
            var Q91;
            Q91=sQuery(id+"F0.wireOp",EDGE,"576c9210-4d5f-4eda-a998-4eb618526b88.0.13.0");
            var Q92;
            Q92=sQuery(id+"F0.wireOp",EDGE,"83a6329f-aab3-466c-9b30-dc960f796cd53.MirrorCS");
            var Q93;
            Q93=sQuery(id+"F0.wireOp",EDGE,"576c9210-4d5f-4eda-a998-4eb618526b88.0.6.2");
            var Q94;
            Q94=sQuery(id+"F0.wireOp",EDGE,"576c9210-4d5f-4eda-a998-4eb618526b88.0.13.2");
            var Q95;
            Q95=sQuery(id+"F0.wireOp",EDGE,"SCyXwFgt-ZhgV-vEtE-fQFI-wdybULJzMTnI");
            var Q96;
            Q96=sQuery(id+"F0.wireOp",EDGE,"576c9210-4d5f-4eda-a998-4eb618526b88.0.15.0");
            var Q97;
            Q97=sQuery(id+"F0.wireOp",EDGE,"576c9210-4d5f-4eda-a998-4eb618526b88.0.3.2");
            var Q98;
            Q98=sQuery(id+"F0.wireOp",EDGE,"576c9210-4d5f-4eda-a998-4eb618526b88.0.8.2");
            var Q99;
            Q99=sQuery(id+"F0.wireOp",EDGE,"83a6329f-aab3-466c-9b30-dc960f796cd556.MirrorCS");
            var Q100;
            Q100=sQuery(id+"F0.wireOp",EDGE,"83a6329f-aab3-466c-9b30-dc960f796cd524.MirrorCS");
            var Q101;
            Q101=sQuery(id+"F0.wireOp",EDGE,"83a6329f-aab3-466c-9b30-dc960f796cd554.MirrorCS");
            var Q102;
            Q102=sQuery(id+"F0.wireOp",EDGE,"83a6329f-aab3-466c-9b30-dc960f796cd523.MirrorCS");
            var Q103;
            Q103=sQuery(id+"F0.wireOp",EDGE,"83a6329f-aab3-466c-9b30-dc960f796cd563.MirrorCS");
            var Q104;
            Q104=sQuery(id+"F0.wireOp",EDGE,"83a6329f-aab3-466c-9b30-dc960f796cd57.MirrorCS");
            var Q105;
            Q105=sQuery(id+"F0.wireOp",EDGE,"83a6329f-aab3-466c-9b30-dc960f796cd522.MirrorCS");
            var Q106;
            Q106=sQuery(id+"F0.wireOp",EDGE,"576c9210-4d5f-4eda-a998-4eb618526b88.0.19.1");
            var Q107;
            Q107=sQuery(id+"F0.wireOp",EDGE,"576c9210-4d5f-4eda-a998-4eb618526b88.0.4.1");
            var Q108;
            Q108=sQuery(id+"F0.wireOp",EDGE,"E2796.MirrorCS");
            var Q109;
            Q109=sQuery(id+"F0.wireOp",EDGE,"83a6329f-aab3-466c-9b30-dc960f796cd534.MirrorCS");
            var Q110;
            Q110=sQuery(id+"F0.wireOp",EDGE,"576c9210-4d5f-4eda-a998-4eb618526b88.0.22.2");
            var Q111;
            Q111=sQuery(id+"F0.wireOp",EDGE,"576c9210-4d5f-4eda-a998-4eb618526b88.0.8.0");
            var Q112;
            Q112=sQuery(id+"F0.wireOp",EDGE,"E2797.MirrorCS");
            var Q113;
            Q113=sQuery(id+"F0.wireOp",EDGE,"83a6329f-aab3-466c-9b30-dc960f796cd549.MirrorCS");
            var Q114;
            Q114=sQuery(id+"F0.wireOp",EDGE,"83a6329f-aab3-466c-9b30-dc960f796cd569.MirrorCS");
            var Q115;
            Q115=sQuery(id+"F0.wireOp",EDGE,"83a6329f-aab3-466c-9b30-dc960f796cd530.MirrorCS");
            var Q116;
            Q116=sQuery(id+"F0.wireOp",EDGE,"83a6329f-aab3-466c-9b30-dc960f796cd536.MirrorCS");
            var Q117;
            Q117=sQuery(id+"F0.wireOp",EDGE,"83a6329f-aab3-466c-9b30-dc960f796cd52.MirrorCS");
            var Q118;
            Q118=sQuery(id+"F0.wireOp",EDGE,"83a6329f-aab3-466c-9b30-dc960f796cd539.MirrorCS");
            var Q119;
            Q119=sQuery(id+"F0.wireOp",EDGE,"576c9210-4d5f-4eda-a998-4eb618526b88.0.10.1");
            var Q120;
            Q120=sQuery(id+"F0.wireOp",EDGE,"576c9210-4d5f-4eda-a998-4eb618526b88.0.18.1");
            var Q121;
            Q121=sQuery(id+"F0.wireOp",EDGE,"576c9210-4d5f-4eda-a998-4eb618526b88.0.17.0");
            var Q122;
            Q122=sQuery(id+"F0.wireOp",EDGE,"576c9210-4d5f-4eda-a998-4eb618526b88.0.14.0");
            var Q123;
            Q123=sQuery(id+"F0.wireOp",EDGE,"83a6329f-aab3-466c-9b30-dc960f796cd547.MirrorCS");
            var Q124;
            Q124=sQuery(id+"F0.wireOp",EDGE,"E2791.MirrorCS");
            var Q125;
            Q125=sQuery(id+"F0.wireOp",EDGE,"576c9210-4d5f-4eda-a998-4eb618526b88.0.11.2");
            var Q126;
            Q126=sQuery(id+"F0.wireOp",EDGE,"pddLhlbR-nzr1-I6ys-tfYb-aMQ4UcdnWBb3");
            var Q127;
            Q127=sQuery(id+"F0.wireOp",EDGE,"83a6329f-aab3-466c-9b30-dc960f796cd533.MirrorCS");
            var Q128;
            Q128=sQuery(id+"F0.wireOp",EDGE,"83a6329f-aab3-466c-9b30-dc960f796cd558.MirrorCS");
            var Q129;
            Q129=sQuery(id+"F0.wireOp",EDGE,"E2794.MirrorCS");
            var Q130;
            Q130=sQuery(id+"F0.wireOp",EDGE,"576c9210-4d5f-4eda-a998-4eb618526b88.0.8.1");
            var Q131;
            Q131=sQuery(id+"F0.wireOp",EDGE,"576c9210-4d5f-4eda-a998-4eb618526b88.0.18.0");
            var Q132;
            Q132=sQuery(id+"F0.wireOp",EDGE,"576c9210-4d5f-4eda-a998-4eb618526b88.0.9.0");
            var Q133;
            Q133=sQuery(id+"F0.wireOp",EDGE,"576c9210-4d5f-4eda-a998-4eb618526b88.0.12.1");
            var Q134;
            Q134=sQuery(id+"F0.wireOp",EDGE,"576c9210-4d5f-4eda-a998-4eb618526b88.0.3.0");
            var Q135;
            Q135=sQuery(id+"F0.wireOp",EDGE,"83a6329f-aab3-466c-9b30-dc960f796cd541.MirrorCS");
            var Q136;
            Q136=sQuery(id+"F0.wireOp",EDGE,"576c9210-4d5f-4eda-a998-4eb618526b88.0.12.0");
            var Q137;
            Q137=sQuery(id+"F0.wireOp",EDGE,"E2799.MirrorCS");
            var Q138;
            Q138=sQuery(id+"F0.wireOp",EDGE,"83a6329f-aab3-466c-9b30-dc960f796cd526.MirrorCS");
            var Q139;
            Q139=sQuery(id+"F0.wireOp",EDGE,"576c9210-4d5f-4eda-a998-4eb618526b88.0.10.2");
            var Q140;
            Q140=sQuery(id+"F0.wireOp",EDGE,"576c9210-4d5f-4eda-a998-4eb618526b88.0.6.1");
            var Q141;
            Q141=sQuery(id+"F0.wireOp",EDGE,"83a6329f-aab3-466c-9b30-dc960f796cd546.MirrorCS");
            var Q142;
            Q142=sQuery(id+"F0.wireOp",EDGE,"83a6329f-aab3-466c-9b30-dc960f796cd574.MirrorCS");
            var Q143;
            Q143=sQuery(id+"F0.wireOp",EDGE,"83a6329f-aab3-466c-9b30-dc960f796cd520.MirrorCS");
            var Q144;
            Q144=sQuery(id+"F0.wireOp",EDGE,"576c9210-4d5f-4eda-a998-4eb618526b88.0.20.2");
            var Q145;
            Q145=sQuery(id+"F0.wireOp",EDGE,"E277");
            var Q146;
            Q146=sQuery(id+"F0.wireOp",EDGE,"E276");
            var Q147;
            Q147=sQuery(id+"F0.wireOp",EDGE,"E282.MirrorCS");
            extrude(context, id + "F15", {"bodyType" : ToolBodyType.SURFACE, "surfaceEntities" : qUnion([Q0, Q1, Q2, Q3, Q4, Q5, Q6, Q7, Q8, Q9, Q10, Q11, Q12, Q13, Q14, Q15, Q16, Q17, Q18, Q19, Q20, Q21, Q22, Q23, Q24, Q25, Q26, Q27, Q28, Q29, Q30, Q31, Q32, Q33, Q34, Q35, Q36, Q37, Q38, Q39, Q40, Q41, Q42, Q43, Q44, Q45, Q46, Q47, Q48, Q49, Q50, Q51, Q52, Q53, Q54, Q55, Q56, Q57, Q58, Q59, Q60, Q61, Q62, Q63, Q64, Q65, Q66, Q67, Q68, Q69, Q70, Q71, Q72, Q73, Q74, Q75, Q76, Q77, Q78, Q79, Q80, Q81, Q82, Q83, Q84, Q85, Q86, Q87, Q88, Q89, Q90, Q91, Q92, Q93, Q94, Q95, Q96, Q97, Q98, Q99, Q100, Q101, Q102, Q103, Q104, Q105, Q106, Q107, Q108, Q109, Q110, Q111, Q112, Q113, Q114, Q115, Q116, Q117, Q118, Q119, Q120, Q121, Q122, Q123, Q124, Q125, Q126, Q127, Q128, Q129, Q130, Q131, Q132, Q133, Q134, Q135, Q136, Q137, Q138, Q139, Q140, Q141, Q142, Q143, Q144, Q145, Q146, Q147]), "depth" : 25.4 * mm});
        }
        {
            var Q0;
            Q0=sQuery(id+"F0.wireOp",EDGE,"E281.MirrorCS");
            extrude(context, id + "F16", {"bodyType" : ToolBodyType.SURFACE, "surfaceEntities" : qUnion([Q0]), "depth" : 25.4 * mm});
        }
        {
            var Q0;
            Q0=sQuery(id+"F0.wireOp",EDGE,"E286");
            var Q1;
            Q1=sQuery(id+"F0.wireOp",EDGE,"E304.0.8.5");
            var Q2;
            Q2=sQuery(id+"F0.wireOp",EDGE,"E393.MirrorCS");
            var Q3;
            Q3=sQuery(id+"F0.wireOp",EDGE,"E304.0.11.4");
            var Q4;
            Q4=sQuery(id+"F0.wireOp",EDGE,"E304.0.10.9");
            var Q5;
            Q5=sQuery(id+"F0.wireOp",EDGE,"E304.0.6.0");
            var Q6;
            Q6=sQuery(id+"F0.wireOp",EDGE,"E304.0.9.8");
            var Q7;
            Q7=sQuery(id+"F0.wireOp",EDGE,"E304.0.13.1");
            var Q8;
            Q8=sQuery(id+"F0.wireOp",EDGE,"E304.0.6.8");
            var Q9;
            Q9=sQuery(id+"F0.wireOp",EDGE,"E429.MirrorCS");
            var Q10;
            Q10=sQuery(id+"F0.wireOp",EDGE,"E304.0.5.5");
            var Q11;
            Q11=sQuery(id+"F0.wireOp",EDGE,"E294");
            var Q12;
            Q12=sQuery(id+"F0.wireOp",EDGE,"E465.MirrorCS");
            var Q13;
            Q13=sQuery(id+"F0.wireOp",EDGE,"E420.MirrorCS");
            var Q14;
            Q14=sQuery(id+"F0.wireOp",EDGE,"E304.0.4.0");
            var Q15;
            Q15=sQuery(id+"F0.wireOp",EDGE,"E404.MirrorCS");
            var Q16;
            Q16=sQuery(id+"F0.wireOp",EDGE,"E304.0.3.1");
            var Q17;
            Q17=sQuery(id+"F0.wireOp",EDGE,"E456.MirrorCS");
            var Q18;
            Q18=sQuery(id+"F0.wireOp",EDGE,"E407.MirrorCS");
            var Q19;
            Q19=sQuery(id+"F0.wireOp",EDGE,"E439.MirrorCS");
            var Q20;
            Q20=sQuery(id+"F0.wireOp",EDGE,"E423.MirrorCS");
            var Q21;
            Q21=sQuery(id+"F0.wireOp",EDGE,"E491.MirrorCS");
            var Q22;
            Q22=sQuery(id+"F0.wireOp",EDGE,"E304.0.2.1");
            var Q23;
            Q23=sQuery(id+"F0.wireOp",EDGE,"E304.0.3.5");
            var Q24;
            Q24=sQuery(id+"F0.wireOp",EDGE,"E304.0.6.1");
            var Q25;
            Q25=sQuery(id+"F0.wireOp",EDGE,"E388.MirrorCS");
            var Q26;
            Q26=sQuery(id+"F0.wireOp",EDGE,"E304.0.8.9");
            var Q27;
            Q27=sQuery(id+"F0.wireOp",EDGE,"E304.0.11.5");
            var Q28;
            Q28=sQuery(id+"F0.wireOp",EDGE,"E304.0.10.1");
            var Q29;
            Q29=sQuery(id+"F0.wireOp",EDGE,"E304.0.12.9");
            var Q30;
            Q30=sQuery(id+"F0.wireOp",EDGE,"E440.MirrorCS");
            var Q31;
            Q31=sQuery(id+"F0.wireOp",EDGE,"E492.MirrorCS");
            var Q32;
            Q32=sQuery(id+"F0.wireOp",EDGE,"E436.MirrorCS");
            var Q33;
            Q33=sQuery(id+"F0.wireOp",EDGE,"E304.0.6.6");
            var Q34;
            Q34=sQuery(id+"F0.wireOp",EDGE,"E461.MirrorCS");
            var Q35;
            Q35=sQuery(id+"F0.wireOp",EDGE,"E383.MirrorCS");
            var Q36;
            Q36=sQuery(id+"F0.wireOp",EDGE,"E413.MirrorCS");
            var Q37;
            Q37=sQuery(id+"F0.wireOp",EDGE,"E441.MirrorCS");
            var Q38;
            Q38=sQuery(id+"F0.wireOp",EDGE,"E304.0.9.9");
            var Q39;
            Q39=sQuery(id+"F0.wireOp",EDGE,"E442.MirrorCS");
            var Q40;
            Q40=sQuery(id+"F0.wireOp",EDGE,"E304.0.10.7");
            var Q41;
            Q41=sQuery(id+"F0.wireOp",EDGE,"E304.0.4.9");
            var Q42;
            Q42=sQuery(id+"F0.wireOp",EDGE,"E304.0.5.4");
            var Q43;
            Q43=sQuery(id+"F0.wireOp",EDGE,"E304.0.12.8");
            var Q44;
            Q44=sQuery(id+"F0.wireOp",EDGE,"E428.MirrorCS");
            var Q45;
            Q45=sQuery(id+"F0.wireOp",EDGE,"E460.MirrorCS");
            var Q46;
            Q46=sQuery(id+"F0.wireOp",EDGE,"E304.0.6.5");
            var Q47;
            Q47=sQuery(id+"F0.wireOp",EDGE,"E304.0.11.1");
            var Q48;
            Q48=sQuery(id+"F0.wireOp",EDGE,"E304.0.8.8");
            var Q49;
            Q49=sQuery(id+"F0.wireOp",EDGE,"E443.MirrorCS");
            var Q50;
            Q50=sQuery(id+"F0.wireOp",EDGE,"E304.0.3.6");
            var Q51;
            Q51=sQuery(id+"F0.wireOp",EDGE,"E377.MirrorCS");
            var Q52;
            Q52=sQuery(id+"F0.wireOp",EDGE,"E392.MirrorCS");
            var Q53;
            Q53=sQuery(id+"F0.wireOp",EDGE,"E482.MirrorCS");
            var Q54;
            Q54=sQuery(id+"F0.wireOp",EDGE,"E304.0.10.5");
            var Q55;
            Q55=sQuery(id+"F0.wireOp",EDGE,"E425.MirrorCS");
            var Q56;
            Q56=sQuery(id+"F0.wireOp",EDGE,"E304.0.2.4");
            var Q57;
            Q57=sQuery(id+"F0.wireOp",EDGE,"E304.0.2.5");
            var Q58;
            Q58=sQuery(id+"F0.wireOp",EDGE,"E447.MirrorCS");
            var Q59;
            Q59=sQuery(id+"F0.wireOp",EDGE,"E469.MirrorCS");
            var Q60;
            Q60=sQuery(id+"F0.wireOp",EDGE,"E304.0.1.1");
            var Q61;
            Q61=sQuery(id+"F0.wireOp",EDGE,"E304.0.14.1");
            var Q62;
            Q62=sQuery(id+"F0.wireOp",EDGE,"E508");
            var Q63;
            Q63=sQuery(id+"F0.wireOp",EDGE,"E408.MirrorCS");
            var Q64;
            Q64=sQuery(id+"F0.wireOp",EDGE,"E424.MirrorCS");
            var Q65;
            Q65=sQuery(id+"F0.wireOp",EDGE,"E304.0.11.6");
            var Q66;
            Q66=sQuery(id+"F0.wireOp",EDGE,"E389.MirrorCS");
            var Q67;
            Q67=sQuery(id+"F0.wireOp",EDGE,"E418.MirrorCS");
            var Q68;
            Q68=sQuery(id+"F0.wireOp",EDGE,"E304.0.9.7");
            var Q69;
            Q69=sQuery(id+"F0.wireOp",EDGE,"E451.MirrorCS");
            var Q70;
            Q70=sQuery(id+"F0.wireOp",EDGE,"E468.MirrorCS");
            var Q71;
            Q71=sQuery(id+"F0.wireOp",EDGE,"E304.0.14.7");
            var Q72;
            Q72=sQuery(id+"F0.wireOp",EDGE,"E426.MirrorCS");
            var Q73;
            Q73=sQuery(id+"F0.wireOp",EDGE,"E480.MirrorCS");
            var Q74;
            Q74=sQuery(id+"F0.wireOp",EDGE,"E419.MirrorCS");
            var Q75;
            Q75=sQuery(id+"F0.wireOp",EDGE,"E304.0.4.1");
            var Q76;
            Q76=sQuery(id+"F0.wireOp",EDGE,"E374.MirrorCS");
            var Q77;
            Q77=sQuery(id+"F0.wireOp",EDGE,"E395.MirrorCS");
            var Q78;
            Q78=sQuery(id+"F0.wireOp",EDGE,"E304.0.2.0");
            var Q79;
            Q79=sQuery(id+"F0.wireOp",EDGE,"E304.0.14.8");
            var Q80;
            Q80=sQuery(id+"F0.wireOp",EDGE,"E304.0.12.4");
            var Q81;
            Q81=sQuery(id+"F0.wireOp",EDGE,"E434.MirrorCS");
            var Q82;
            Q82=sQuery(id+"F0.wireOp",EDGE,"E304.0.12.5");
            var Q83;
            Q83=sQuery(id+"F0.wireOp",EDGE,"E453.MirrorCS");
            var Q84;
            Q84=sQuery(id+"F0.wireOp",EDGE,"E304.0.3.9");
            var Q85;
            Q85=sQuery(id+"F0.wireOp",EDGE,"E304.0.9.0");
            var Q86;
            Q86=sQuery(id+"F0.wireOp",EDGE,"E481.MirrorCS");
            var Q87;
            Q87=sQuery(id+"F0.wireOp",EDGE,"E304.0.14.0");
            var Q88;
            Q88=sQuery(id+"F0.wireOp",EDGE,"E470.MirrorCS");
            var Q89;
            Q89=sQuery(id+"F0.wireOp",EDGE,"E304.0.11.7");
            var Q90;
            Q90=sQuery(id+"F0.wireOp",EDGE,"E444.MirrorCS");
            var Q91;
            Q91=sQuery(id+"F0.wireOp",EDGE,"E304.0.6.7");
            var Q92;
            Q92=sQuery(id+"F0.wireOp",EDGE,"E304.0.8.6");
            var Q93;
            Q93=sQuery(id+"F0.wireOp",EDGE,"E386.MirrorCS");
            var Q94;
            Q94=sQuery(id+"F0.wireOp",EDGE,"E304.0.7.1");
            var Q95;
            Q95=sQuery(id+"F0.wireOp",EDGE,"E304.0.1.4");
            var Q96;
            Q96=sQuery(id+"F0.wireOp",EDGE,"E379.MirrorCS");
            var Q97;
            Q97=sQuery(id+"F0.wireOp",EDGE,"E304.0.7.4");
            var Q98;
            Q98=sQuery(id+"F0.wireOp",EDGE,"E483.MirrorCS");
            var Q99;
            Q99=sQuery(id+"F0.wireOp",EDGE,"E398.MirrorCS");
            var Q100;
            Q100=sQuery(id+"F0.wireOp",EDGE,"E304.0.14.6");
            var Q101;
            Q101=sQuery(id+"F0.wireOp",EDGE,"E498.MirrorCS");
            var Q102;
            Q102=sQuery(id+"F0.wireOp",EDGE,"E409.MirrorCS");
            var Q103;
            Q103=sQuery(id+"F0.wireOp",EDGE,"E391.MirrorCS");
            var Q104;
            Q104=sQuery(id+"F0.wireOp",EDGE,"E304.0.13.9");
            var Q105;
            Q105=sQuery(id+"F0.wireOp",EDGE,"E396.MirrorCS");
            var Q106;
            Q106=sQuery(id+"F0.wireOp",EDGE,"E304.0.3.8");
            var Q107;
            Q107=sQuery(id+"F0.wireOp",EDGE,"E496.MirrorCS");
            var Q108;
            Q108=sQuery(id+"F0.wireOp",EDGE,"E380.MirrorCS");
            var Q109;
            Q109=sQuery(id+"F0.wireOp",EDGE,"E304.0.7.7");
            var Q110;
            Q110=sQuery(id+"F0.wireOp",EDGE,"E446.MirrorCS");
            var Q111;
            Q111=sQuery(id+"F0.wireOp",EDGE,"E432.MirrorCS");
            var Q112;
            Q112=sQuery(id+"F0.wireOp",EDGE,"E382.MirrorCS");
            var Q113;
            Q113=sQuery(id+"F0.wireOp",EDGE,"E304.0.4.5");
            var Q114;
            Q114=sQuery(id+"F0.wireOp",EDGE,"E490.MirrorCS");
            var Q115;
            Q115=sQuery(id+"F0.wireOp",EDGE,"E462.MirrorCS");
            var Q116;
            Q116=sQuery(id+"F0.wireOp",EDGE,"E304.0.11.0");
            var Q117;
            Q117=sQuery(id+"F0.wireOp",EDGE,"E304.0.8.0");
            var Q118;
            Q118=sQuery(id+"F0.wireOp",EDGE,"E304.0.4.8");
            var Q119;
            Q119=sQuery(id+"F0.wireOp",EDGE,"E454.MirrorCS");
            var Q120;
            Q120=sQuery(id+"F0.wireOp",EDGE,"E304.0.11.9");
            var Q121;
            Q121=sQuery(id+"F0.wireOp",EDGE,"E431.MirrorCS");
            var Q122;
            Q122=sQuery(id+"F0.wireOp",EDGE,"E304.0.1.9");
            var Q123;
            Q123=sQuery(id+"F0.wireOp",EDGE,"E304.0.2.6");
            var Q124;
            Q124=sQuery(id+"F0.wireOp",EDGE,"E304.0.13.8");
            var Q125;
            Q125=sQuery(id+"F0.wireOp",EDGE,"E304.0.14.9");
            var Q126;
            Q126=sQuery(id+"F0.wireOp",EDGE,"E304.0.10.0");
            var Q127;
            Q127=sQuery(id+"F0.wireOp",EDGE,"E284");
            var Q128;
            Q128=sQuery(id+"F0.wireOp",EDGE,"E421.MirrorCS");
            var Q129;
            Q129=sQuery(id+"F0.wireOp",EDGE,"E385.MirrorCS");
            var Q130;
            Q130=sQuery(id+"F0.wireOp",EDGE,"E437.MirrorCS");
            var Q131;
            Q131=sQuery(id+"F0.wireOp",EDGE,"E505.MirrorCS");
            var Q132;
            Q132=sQuery(id+"F0.wireOp",EDGE,"E464.MirrorCS");
            var Q133;
            Q133=sQuery(id+"F0.wireOp",EDGE,"E500.MirrorCS");
            var Q134;
            Q134=sQuery(id+"F0.wireOp",EDGE,"E484.MirrorCS");
            var Q135;
            Q135=sQuery(id+"F0.wireOp",EDGE,"E304.0.12.6");
            var Q136;
            Q136=sQuery(id+"F0.wireOp",EDGE,"E455.MirrorCS");
            var Q137;
            Q137=sQuery(id+"F0.wireOp",EDGE,"E297");
            var Q138;
            Q138=sQuery(id+"F0.wireOp",EDGE,"E488.MirrorCS");
            var Q139;
            Q139=sQuery(id+"F0.wireOp",EDGE,"E304.0.13.5");
            var Q140;
            Q140=sQuery(id+"F0.wireOp",EDGE,"E304.0.1.5");
            var Q141;
            Q141=sQuery(id+"F0.wireOp",EDGE,"E403.MirrorCS");
            var Q142;
            Q142=sQuery(id+"F0.wireOp",EDGE,"E304.0.3.0");
            var Q143;
            Q143=sQuery(id+"F0.wireOp",EDGE,"E478.MirrorCS");
            var Q144;
            Q144=sQuery(id+"F0.wireOp",EDGE,"E494.MirrorCS");
            var Q145;
            Q145=sQuery(id+"F0.wireOp",EDGE,"E459.MirrorCS");
            var Q146;
            Q146=sQuery(id+"F0.wireOp",EDGE,"E375.MirrorCS");
            var Q147;
            Q147=sQuery(id+"F0.wireOp",EDGE,"E495.MirrorCS");
            var Q148;
            Q148=sQuery(id+"F0.wireOp",EDGE,"E479.MirrorCS");
            var Q149;
            Q149=sQuery(id+"F0.wireOp",EDGE,"E304.0.8.7");
            var Q150;
            Q150=sQuery(id+"F0.wireOp",EDGE,"E304.0.4.7");
            var Q151;
            Q151=sQuery(id+"F0.wireOp",EDGE,"E304.0.12.7");
            var Q152;
            Q152=sQuery(id+"F0.wireOp",EDGE,"E405.MirrorCS");
            var Q153;
            Q153=sQuery(id+"F0.wireOp",EDGE,"E411.MirrorCS");
            var Q154;
            Q154=sQuery(id+"F0.wireOp",EDGE,"E427.MirrorCS");
            var Q155;
            Q155=sQuery(id+"F0.wireOp",EDGE,"E384.MirrorCS");
            var Q156;
            Q156=sQuery(id+"F0.wireOp",EDGE,"E445.MirrorCS");
            var Q157;
            Q157=sQuery(id+"F0.wireOp",EDGE,"E304.0.5.8");
            var Q158;
            Q158=sQuery(id+"F0.wireOp",EDGE,"E472.MirrorCS");
            var Q159;
            Q159=sQuery(id+"F0.wireOp",EDGE,"E435.MirrorCS");
            var Q160;
            Q160=sQuery(id+"F0.wireOp",EDGE,"E487.MirrorCS");
            var Q161;
            Q161=sQuery(id+"F0.wireOp",EDGE,"E304.0.7.0");
            var Q162;
            Q162=sQuery(id+"F0.wireOp",EDGE,"E304.0.1.0");
            var Q163;
            Q163=sQuery(id+"F0.wireOp",EDGE,"E304.0.7.8");
            var Q164;
            Q164=sQuery(id+"F0.wireOp",EDGE,"E293");
            var Q165;
            Q165=sQuery(id+"F0.wireOp",EDGE,"E304.0.1.8");
            var Q166;
            Q166=sQuery(id+"F0.wireOp",EDGE,"E304.0.4.4");
            var Q167;
            Q167=sQuery(id+"F0.wireOp",EDGE,"E304.0.7.5");
            var Q168;
            Q168=sQuery(id+"F0.wireOp",EDGE,"E506.MirrorCS");
            var Q169;
            Q169=sQuery(id+"F0.wireOp",EDGE,"E304.0.14.4");
            var Q170;
            Q170=sQuery(id+"F0.wireOp",EDGE,"E304.0.1.7");
            var Q171;
            Q171=sQuery(id+"F0.wireOp",EDGE,"E415.MirrorCS");
            var Q172;
            Q172=sQuery(id+"F0.wireOp",EDGE,"E422.MirrorCS");
            var Q173;
            Q173=sQuery(id+"F0.wireOp",EDGE,"E304.0.5.0");
            var Q174;
            Q174=sQuery(id+"F0.wireOp",EDGE,"E304.0.2.8");
            var Q175;
            Q175=sQuery(id+"F0.wireOp",EDGE,"E304.0.4.6");
            var Q176;
            Q176=sQuery(id+"F0.wireOp",EDGE,"E471.MirrorCS");
            var Q177;
            Q177=sQuery(id+"F0.wireOp",EDGE,"E304.0.3.4");
            var Q178;
            Q178=sQuery(id+"F0.wireOp",EDGE,"E304.0.10.4");
            var Q179;
            Q179=sQuery(id+"F0.wireOp",EDGE,"E304.0.6.9");
            var Q180;
            Q180=sQuery(id+"F0.wireOp",EDGE,"E304.0.9.4");
            var Q181;
            Q181=sQuery(id+"F0.wireOp",EDGE,"E497.MirrorCS");
            var Q182;
            Q182=sQuery(id+"F0.wireOp",EDGE,"E304.0.8.4");
            var Q183;
            Q183=sQuery(id+"F0.wireOp",EDGE,"E304.0.8.1");
            var Q184;
            Q184=sQuery(id+"F0.wireOp",EDGE,"E475.MirrorCS");
            var Q185;
            Q185=sQuery(id+"F0.wireOp",EDGE,"E304.0.10.6");
            var Q186;
            Q186=sQuery(id+"F0.wireOp",EDGE,"E463.MirrorCS");
            var Q187;
            Q187=sQuery(id+"F0.wireOp",EDGE,"E304.0.3.7");
            var Q188;
            Q188=sQuery(id+"F0.wireOp",EDGE,"E304.0.13.4");
            var Q189;
            Q189=sQuery(id+"F0.wireOp",EDGE,"E304.0.7.6");
            var Q190;
            Q190=sQuery(id+"F0.wireOp",EDGE,"E503.MirrorCS");
            var Q191;
            Q191=sQuery(id+"F0.wireOp",EDGE,"E304.0.12.0");
            var Q192;
            Q192=sQuery(id+"F0.wireOp",EDGE,"E406.MirrorCS");
            var Q193;
            Q193=sQuery(id+"F0.wireOp",EDGE,"E458.MirrorCS");
            var Q194;
            Q194=sQuery(id+"F0.wireOp",EDGE,"E410.MirrorCS");
            var Q195;
            Q195=sQuery(id+"F0.wireOp",EDGE,"E304.0.6.4");
            var Q196;
            Q196=sQuery(id+"F0.wireOp",EDGE,"E304.0.9.1");
            var Q197;
            Q197=sQuery(id+"F0.wireOp",EDGE,"E304.0.7.9");
            var Q198;
            Q198=sQuery(id+"F0.wireOp",EDGE,"E412.MirrorCS");
            var Q199;
            Q199=sQuery(id+"F0.wireOp",EDGE,"E304.0.14.5");
            var Q200;
            Q200=sQuery(id+"F0.wireOp",EDGE,"E304.0.9.5");
            var Q201;
            Q201=sQuery(id+"F0.wireOp",EDGE,"E499.MirrorCS");
            var Q202;
            Q202=sQuery(id+"F0.wireOp",EDGE,"E304.0.2.7");
            var Q203;
            Q203=sQuery(id+"F0.wireOp",EDGE,"E304.0.10.8");
            var Q204;
            Q204=sQuery(id+"F0.wireOp",EDGE,"E438.MirrorCS");
            var Q205;
            Q205=sQuery(id+"F0.wireOp",EDGE,"E304.0.13.0");
            var Q206;
            Q206=sQuery(id+"F0.wireOp",EDGE,"E416.MirrorCS");
            var Q207;
            Q207=sQuery(id+"F0.wireOp",EDGE,"E304.0.2.9");
            var Q208;
            Q208=sQuery(id+"F0.wireOp",EDGE,"E304.0.12.1");
            var Q209;
            Q209=sQuery(id+"F0.wireOp",EDGE,"E493.MirrorCS");
            var Q210;
            Q210=sQuery(id+"F0.wireOp",EDGE,"E448.MirrorCS");
            var Q211;
            Q211=sQuery(id+"F0.wireOp",EDGE,"E304.0.5.9");
            var Q212;
            Q212=sQuery(id+"F0.wireOp",EDGE,"E430.MirrorCS");
            var Q213;
            Q213=sQuery(id+"F0.wireOp",EDGE,"E304.0.11.8");
            var Q214;
            Q214=sQuery(id+"F0.wireOp",EDGE,"E376.MirrorCS");
            var Q215;
            Q215=sQuery(id+"F0.wireOp",EDGE,"E414.MirrorCS");
            var Q216;
            Q216=sQuery(id+"F0.wireOp",EDGE,"E304.0.5.1");
            var Q217;
            Q217=sQuery(id+"F0.wireOp",EDGE,"E394.MirrorCS");
            var Q218;
            Q218=sQuery(id+"F0.wireOp",EDGE,"E296");
            var Q219;
            Q219=sQuery(id+"F0.wireOp",EDGE,"E485.MirrorCS");
            var Q220;
            Q220=sQuery(id+"F0.wireOp",EDGE,"E417.MirrorCS");
            var Q221;
            Q221=sQuery(id+"F0.wireOp",EDGE,"E433.MirrorCS");
            var Q222;
            Q222=sQuery(id+"F0.wireOp",EDGE,"E381.MirrorCS");
            var Q223;
            Q223=sQuery(id+"F0.wireOp",EDGE,"E304.0.9.6");
            var Q224;
            Q224=sQuery(id+"F0.wireOp",EDGE,"E304.0.13.6");
            var Q225;
            Q225=sQuery(id+"F0.wireOp",EDGE,"E502.MirrorCS");
            var Q226;
            Q226=sQuery(id+"F0.wireOp",EDGE,"E467.MirrorCS");
            var Q227;
            Q227=sQuery(id+"F0.wireOp",EDGE,"E304.0.13.7");
            var Q228;
            Q228=sQuery(id+"F0.wireOp",EDGE,"E466.MirrorCS");
            var Q229;
            Q229=sQuery(id+"F0.wireOp",EDGE,"E450.MirrorCS");
            var Q230;
            Q230=sQuery(id+"F0.wireOp",EDGE,"E304.0.5.6");
            var Q231;
            Q231=sQuery(id+"F0.wireOp",EDGE,"E304.0.1.6");
            var Q232;
            Q232=sQuery(id+"F0.wireOp",EDGE,"E501.MirrorCS");
            var Q233;
            Q233=sQuery(id+"F0.wireOp",EDGE,"E397.MirrorCS");
            var Q234;
            Q234=sQuery(id+"F0.wireOp",EDGE,"E304.0.5.7");
            var Q235;
            Q235=sQuery(id+"F0.wireOp",EDGE,"E486.MirrorCS");
            var Q236;
            Q236=sQuery(id+"F0.wireOp",EDGE,"E321.MirrorCS");
            var Q237;
            Q237=sQuery(id+"F0.wireOp",EDGE,"E358.MirrorCS");
            var Q238;
            Q238=sQuery(id+"F0.wireOp",EDGE,"E298");
            var Q239;
            Q239=sQuery(id+"F0.wireOp",EDGE,"E304.0.14.3");
            var Q240;
            Q240=sQuery(id+"F0.wireOp",EDGE,"E310.MirrorCS");
            var Q241;
            Q241=sQuery(id+"F0.wireOp",EDGE,"E344.MirrorCS");
            var Q242;
            Q242=sQuery(id+"F0.wireOp",EDGE,"E304.0.9.2");
            var Q243;
            Q243=sQuery(id+"F0.wireOp",EDGE,"E360.MirrorCS");
            var Q244;
            Q244=sQuery(id+"F0.wireOp",EDGE,"E304.0.8.10");
            var Q245;
            Q245=sQuery(id+"F0.wireOp",EDGE,"E304.0.1.10");
            var Q246;
            Q246=sQuery(id+"F0.wireOp",EDGE,"E304.0.5.10");
            var Q247;
            Q247=sQuery(id+"F0.wireOp",EDGE,"E304.0.13.10");
            var Q248;
            Q248=sQuery(id+"F0.wireOp",EDGE,"E304.0.9.3");
            var Q249;
            Q249=sQuery(id+"F0.wireOp",EDGE,"E304.0.9.10");
            var Q250;
            Q250=sQuery(id+"F0.wireOp",EDGE,"E304.0.5.11");
            var Q251;
            Q251=sQuery(id+"F0.wireOp",EDGE,"E329.MirrorCS");
            var Q252;
            Q252=sQuery(id+"F0.wireOp",EDGE,"E304.0.14.2");
            var Q253;
            Q253=sQuery(id+"F0.wireOp",EDGE,"E368.MirrorCS");
            var Q254;
            Q254=sQuery(id+"F0.wireOp",EDGE,"E304.0.7.10");
            var Q255;
            Q255=sQuery(id+"F0.wireOp",EDGE,"E357.MirrorCS");
            var Q256;
            Q256=sQuery(id+"F0.wireOp",EDGE,"E353.MirrorCS");
            var Q257;
            Q257=sQuery(id+"F0.wireOp",EDGE,"E327.MirrorCS");
            var Q258;
            Q258=sQuery(id+"F0.wireOp",EDGE,"E338.MirrorCS");
            var Q259;
            Q259=sQuery(id+"F0.wireOp",EDGE,"E319.MirrorCS");
            var Q260;
            Q260=sQuery(id+"F0.wireOp",EDGE,"E347.MirrorCS");
            var Q261;
            Q261=sQuery(id+"F0.wireOp",EDGE,"E342.MirrorCS");
            var Q262;
            Q262=sQuery(id+"F0.wireOp",EDGE,"E304.0.14.10");
            var Q263;
            Q263=sQuery(id+"F0.wireOp",EDGE,"E304.0.2.10");
            var Q264;
            Q264=sQuery(id+"F0.wireOp",EDGE,"E366.MirrorCS");
            var Q265;
            Q265=sQuery(id+"F0.wireOp",EDGE,"E365.MirrorCS");
            var Q266;
            Q266=sQuery(id+"F0.wireOp",EDGE,"E350.MirrorCS");
            var Q267;
            Q267=sQuery(id+"F0.wireOp",EDGE,"E304.0.6.10");
            var Q268;
            Q268=sQuery(id+"F0.wireOp",EDGE,"E328.MirrorCS");
            var Q269;
            Q269=sQuery(id+"F0.wireOp",EDGE,"E335.MirrorCS");
            var Q270;
            Q270=sQuery(id+"F0.wireOp",EDGE,"E507");
            var Q271;
            Q271=sQuery(id+"F0.wireOp",EDGE,"E340.MirrorCS");
            var Q272;
            Q272=sQuery(id+"F0.wireOp",EDGE,"E295");
            var Q273;
            Q273=sQuery(id+"F0.wireOp",EDGE,"E304.0.5.3");
            var Q274;
            Q274=sQuery(id+"F0.wireOp",EDGE,"E304.0.10.2");
            var Q275;
            Q275=sQuery(id+"F0.wireOp",EDGE,"E304.0.11.2");
            var Q276;
            Q276=sQuery(id+"F0.wireOp",EDGE,"E304.0.12.3");
            var Q277;
            Q277=sQuery(id+"F0.wireOp",EDGE,"E304.0.6.3");
            var Q278;
            Q278=sQuery(id+"F0.wireOp",EDGE,"E304.0.10.3");
            var Q279;
            Q279=sQuery(id+"F0.wireOp",EDGE,"E370.MirrorCS");
            var Q280;
            Q280=sQuery(id+"F0.wireOp",EDGE,"E337.MirrorCS");
            var Q281;
            Q281=sQuery(id+"F0.wireOp",EDGE,"E304.0.11.3");
            var Q282;
            Q282=sQuery(id+"F0.wireOp",EDGE,"E364.MirrorCS");
            var Q283;
            Q283=sQuery(id+"F0.wireOp",EDGE,"E304.0.2.3");
            var Q284;
            Q284=sQuery(id+"F0.wireOp",EDGE,"E304.0.3.3");
            var Q285;
            Q285=sQuery(id+"F0.wireOp",EDGE,"E304.0.5.2");
            var Q286;
            Q286=sQuery(id+"F0.wireOp",EDGE,"E304.0.8.11");
            var Q287;
            Q287=sQuery(id+"F0.wireOp",EDGE,"E304.0.13.3");
            var Q288;
            Q288=sQuery(id+"F0.wireOp",EDGE,"E363.MirrorCS");
            var Q289;
            Q289=sQuery(id+"F0.wireOp",EDGE,"E322.MirrorCS");
            var Q290;
            Q290=sQuery(id+"F0.wireOp",EDGE,"E304.0.2.2");
            var Q291;
            Q291=sQuery(id+"F0.wireOp",EDGE,"E311.MirrorCS");
            var Q292;
            Q292=sQuery(id+"F0.wireOp",EDGE,"E343.MirrorCS");
            var Q293;
            Q293=sQuery(id+"F0.wireOp",EDGE,"E304.0.1.11");
            var Q294;
            Q294=sQuery(id+"F0.wireOp",EDGE,"E304.0.9.11");
            var Q295;
            Q295=sQuery(id+"F0.wireOp",EDGE,"E313.MirrorCS");
            var Q296;
            Q296=sQuery(id+"F0.wireOp",EDGE,"E304.0.6.2");
            var Q297;
            Q297=sQuery(id+"F0.wireOp",EDGE,"E304.0.3.2");
            var Q298;
            Q298=sQuery(id+"F0.wireOp",EDGE,"E367.MirrorCS");
            var Q299;
            Q299=sQuery(id+"F0.wireOp",EDGE,"E345.MirrorCS");
            var Q300;
            Q300=sQuery(id+"F0.wireOp",EDGE,"E348.MirrorCS");
            var Q301;
            Q301=sQuery(id+"F0.wireOp",EDGE,"E304.0.13.2");
            var Q302;
            Q302=sQuery(id+"F0.wireOp",EDGE,"E331.MirrorCS");
            var Q303;
            Q303=sQuery(id+"F0.wireOp",EDGE,"E351.MirrorCS");
            var Q304;
            Q304=sQuery(id+"F0.wireOp",EDGE,"E304.0.7.11");
            var Q305;
            Q305=sQuery(id+"F0.wireOp",EDGE,"E330.MirrorCS");
            var Q306;
            Q306=sQuery(id+"F0.wireOp",EDGE,"E304.0.13.11");
            var Q307;
            Q307=sQuery(id+"F0.wireOp",EDGE,"E349.MirrorCS");
            var Q308;
            Q308=sQuery(id+"F0.wireOp",EDGE,"E304.0.12.2");
            var Q309;
            Q309=sQuery(id+"F0.wireOp",EDGE,"E317.MirrorCS");
            var Q310;
            Q310=sQuery(id+"F0.wireOp",EDGE,"E304.0.14.11");
            var Q311;
            Q311=sQuery(id+"F0.wireOp",EDGE,"E304.0.6.11");
            var Q312;
            Q312=sQuery(id+"F0.wireOp",EDGE,"E346.MirrorCS");
            var Q313;
            Q313=sQuery(id+"F0.wireOp",EDGE,"E352.MirrorCS");
            var Q314;
            Q314=sQuery(id+"F0.wireOp",EDGE,"E324.MirrorCS");
            var Q315;
            Q315=sQuery(id+"F0.wireOp",EDGE,"E355.MirrorCS");
            var Q316;
            Q316=sQuery(id+"F0.wireOp",EDGE,"E304.0.3.11");
            var Q317;
            Q317=sQuery(id+"F0.wireOp",EDGE,"E304.0.4.11");
            var Q318;
            Q318=sQuery(id+"F0.wireOp",EDGE,"E304.0.2.11");
            var Q319;
            Q319=sQuery(id+"F0.wireOp",EDGE,"E341.MirrorCS");
            var Q320;
            Q320=sQuery(id+"F0.wireOp",EDGE,"E309.MirrorCS");
            var Q321;
            Q321=sQuery(id+"F0.wireOp",EDGE,"E304.0.7.2");
            var Q322;
            Q322=sQuery(id+"F0.wireOp",EDGE,"E332.MirrorCS");
            var Q323;
            Q323=sQuery(id+"F0.wireOp",EDGE,"E304.0.11.11");
            var Q324;
            Q324=sQuery(id+"F0.wireOp",EDGE,"E314.MirrorCS");
            var Q325;
            Q325=sQuery(id+"F0.wireOp",EDGE,"E336.MirrorCS");
            var Q326;
            Q326=sQuery(id+"F0.wireOp",EDGE,"E318.MirrorCS");
            var Q327;
            Q327=sQuery(id+"F0.wireOp",EDGE,"E304.0.3.10");
            var Q328;
            Q328=sQuery(id+"F0.wireOp",EDGE,"E334.MirrorCS");
            var Q329;
            Q329=sQuery(id+"F0.wireOp",EDGE,"E304.0.1.2");
            var Q330;
            Q330=sQuery(id+"F0.wireOp",EDGE,"E369.MirrorCS");
            var Q331;
            Q331=sQuery(id+"F0.wireOp",EDGE,"E304.0.4.10");
            var Q332;
            Q332=sQuery(id+"F0.wireOp",EDGE,"E359.MirrorCS");
            var Q333;
            Q333=sQuery(id+"F0.wireOp",EDGE,"E320.MirrorCS");
            var Q334;
            Q334=sQuery(id+"F0.wireOp",EDGE,"E304.0.11.10");
            var Q335;
            Q335=sQuery(id+"F0.wireOp",EDGE,"E304.0.12.11");
            var Q336;
            Q336=sQuery(id+"F0.wireOp",EDGE,"E354.MirrorCS");
            var Q337;
            Q337=sQuery(id+"F0.wireOp",EDGE,"E304.0.1.3");
            var Q338;
            Q338=sQuery(id+"F0.wireOp",EDGE,"E312.MirrorCS");
            var Q339;
            Q339=sQuery(id+"F0.wireOp",EDGE,"E316.MirrorCS");
            var Q340;
            Q340=sQuery(id+"F0.wireOp",EDGE,"E304.0.12.10");
            var Q341;
            Q341=sQuery(id+"F0.wireOp",EDGE,"E323.MirrorCS");
            var Q342;
            Q342=sQuery(id+"F0.wireOp",EDGE,"E326.MirrorCS");
            var Q343;
            Q343=sQuery(id+"F0.wireOp",EDGE,"E304.0.7.3");
            var Q344;
            Q344=sQuery(id+"F0.wireOp",EDGE,"E361.MirrorCS");
            var Q345;
            Q345=sQuery(id+"F0.wireOp",EDGE,"E304.0.8.2");
            var Q346;
            Q346=sQuery(id+"F0.wireOp",EDGE,"E304.0.10.10");
            var Q347;
            Q347=sQuery(id+"F0.wireOp",EDGE,"E304.0.4.3");
            var Q348;
            Q348=sQuery(id+"F0.wireOp",EDGE,"E304.0.4.2");
            var Q349;
            Q349=sQuery(id+"F0.wireOp",EDGE,"E304.0.8.3");
            var Q350;
            Q350=sQuery(id+"F0.wireOp",EDGE,"E304.0.10.11");
            var Q351;
            Q351=sQuery(id+"F0.wireOp",EDGE,"E290");
            var Q352;
            Q352=sQuery(id+"F0.wireOp",EDGE,"E315.MirrorCS");
            var Q353;
            Q353=sQuery(id+"F0.wireOp",EDGE,"E333.MirrorCS");
            var Q354;
            Q354=sQuery(id+"F0.wireOp",EDGE,"E325.MirrorCS");
            var Q355;
            Q355=sQuery(id+"F0.wireOp",EDGE,"E291");
            var Q356;
            Q356=sQuery(id+"F0.wireOp",EDGE,"E285");
            var Q357;
            Q357=sQuery(id+"F0.wireOp",EDGE,"E390.MirrorCS");
            var Q358;
            Q358=sQuery(id+"F0.wireOp",EDGE,"E371.MirrorCS");
            var Q359;
            Q359=sQuery(id+"F0.wireOp",EDGE,"E283");
            var Q360;
            Q360=sQuery(id+"F0.wireOp",EDGE,"E372.MirrorCS");
            var Q361;
            Q361=sQuery(id+"F0.wireOp",EDGE,"E373.MirrorCS");
            var Q362;
            Q362=sQuery(id+"F0.wireOp",EDGE,"E287");
            var Q363;
            Q363=sQuery(id+"F0.wireOp",EDGE,"E362.MirrorCS");
            var Q364;
            Q364=sQuery(id+"F0.wireOp",EDGE,"E274");
            var Q365;
            Q365=sQuery(id+"F0.wireOp",EDGE,"E288");
            var Q366;
            Q366=sQuery(id+"F0.wireOp",EDGE,"E457.MirrorCS");
            var Q367;
            Q367=sQuery(id+"F0.wireOp",EDGE,"E489.MirrorCS");
            var Q368;
            Q368=sQuery(id+"F0.wireOp",EDGE,"E307");
            var Q369;
            Q369=sQuery(id+"F0.wireOp",EDGE,"E306");
            var Q370;
            Q370=sQuery(id+"F0.wireOp",EDGE,"E308");
            var Q371;
            Q371=sQuery(id+"F0.wireOp",EDGE,"E473.MirrorCS");
            var Q372;
            Q372=sQuery(id+"F0.wireOp",EDGE,"E305");
            var Q373;
            Q373=sQuery(id+"F0.wireOp",EDGE,"E452.MirrorCS");
            extrude(context, id + "F17", {"bodyType" : ToolBodyType.SURFACE, "surfaceEntities" : qUnion([Q0, Q1, Q2, Q3, Q4, Q5, Q6, Q7, Q8, Q9, Q10, Q11, Q12, Q13, Q14, Q15, Q16, Q17, Q18, Q19, Q20, Q21, Q22, Q23, Q24, Q25, Q26, Q27, Q28, Q29, Q30, Q31, Q32, Q33, Q34, Q35, Q36, Q37, Q38, Q39, Q40, Q41, Q42, Q43, Q44, Q45, Q46, Q47, Q48, Q49, Q50, Q51, Q52, Q53, Q54, Q55, Q56, Q57, Q58, Q59, Q60, Q61, Q62, Q63, Q64, Q65, Q66, Q67, Q68, Q69, Q70, Q71, Q72, Q73, Q74, Q75, Q76, Q77, Q78, Q79, Q80, Q81, Q82, Q83, Q84, Q85, Q86, Q87, Q88, Q89, Q90, Q91, Q92, Q93, Q94, Q95, Q96, Q97, Q98, Q99, Q100, Q101, Q102, Q103, Q104, Q105, Q106, Q107, Q108, Q109, Q110, Q111, Q112, Q113, Q114, Q115, Q116, Q117, Q118, Q119, Q120, Q121, Q122, Q123, Q124, Q125, Q126, Q127, Q128, Q129, Q130, Q131, Q132, Q133, Q134, Q135, Q136, Q137, Q138, Q139, Q140, Q141, Q142, Q143, Q144, Q145, Q146, Q147, Q148, Q149, Q150, Q151, Q152, Q153, Q154, Q155, Q156, Q157, Q158, Q159, Q160, Q161, Q162, Q163, Q164, Q165, Q166, Q167, Q168, Q169, Q170, Q171, Q172, Q173, Q174, Q175, Q176, Q177, Q178, Q179, Q180, Q181, Q182, Q183, Q184, Q185, Q186, Q187, Q188, Q189, Q190, Q191, Q192, Q193, Q194, Q195, Q196, Q197, Q198, Q199, Q200, Q201, Q202, Q203, Q204, Q205, Q206, Q207, Q208, Q209, Q210, Q211, Q212, Q213, Q214, Q215, Q216, Q217, Q218, Q219, Q220, Q221, Q222, Q223, Q224, Q225, Q226, Q227, Q228, Q229, Q230, Q231, Q232, Q233, Q234, Q235, Q236, Q237, Q238, Q239, Q240, Q241, Q242, Q243, Q244, Q245, Q246, Q247, Q248, Q249, Q250, Q251, Q252, Q253, Q254, Q255, Q256, Q257, Q258, Q259, Q260, Q261, Q262, Q263, Q264, Q265, Q266, Q267, Q268, Q269, Q270, Q271, Q272, Q273, Q274, Q275, Q276, Q277, Q278, Q279, Q280, Q281, Q282, Q283, Q284, Q285, Q286, Q287, Q288, Q289, Q290, Q291, Q292, Q293, Q294, Q295, Q296, Q297, Q298, Q299, Q300, Q301, Q302, Q303, Q304, Q305, Q306, Q307, Q308, Q309, Q310, Q311, Q312, Q313, Q314, Q315, Q316, Q317, Q318, Q319, Q320, Q321, Q322, Q323, Q324, Q325, Q326, Q327, Q328, Q329, Q330, Q331, Q332, Q333, Q334, Q335, Q336, Q337, Q338, Q339, Q340, Q341, Q342, Q343, Q344, Q345, Q346, Q347, Q348, Q349, Q350, Q351, Q352, Q353, Q354, Q355, Q356, Q357, Q358, Q359, Q360, Q361, Q362, Q363, Q364, Q365, Q366, Q367, Q368, Q369, Q370, Q371, Q372, Q373]), "depth" : 25.4 * mm});
        }
    });
